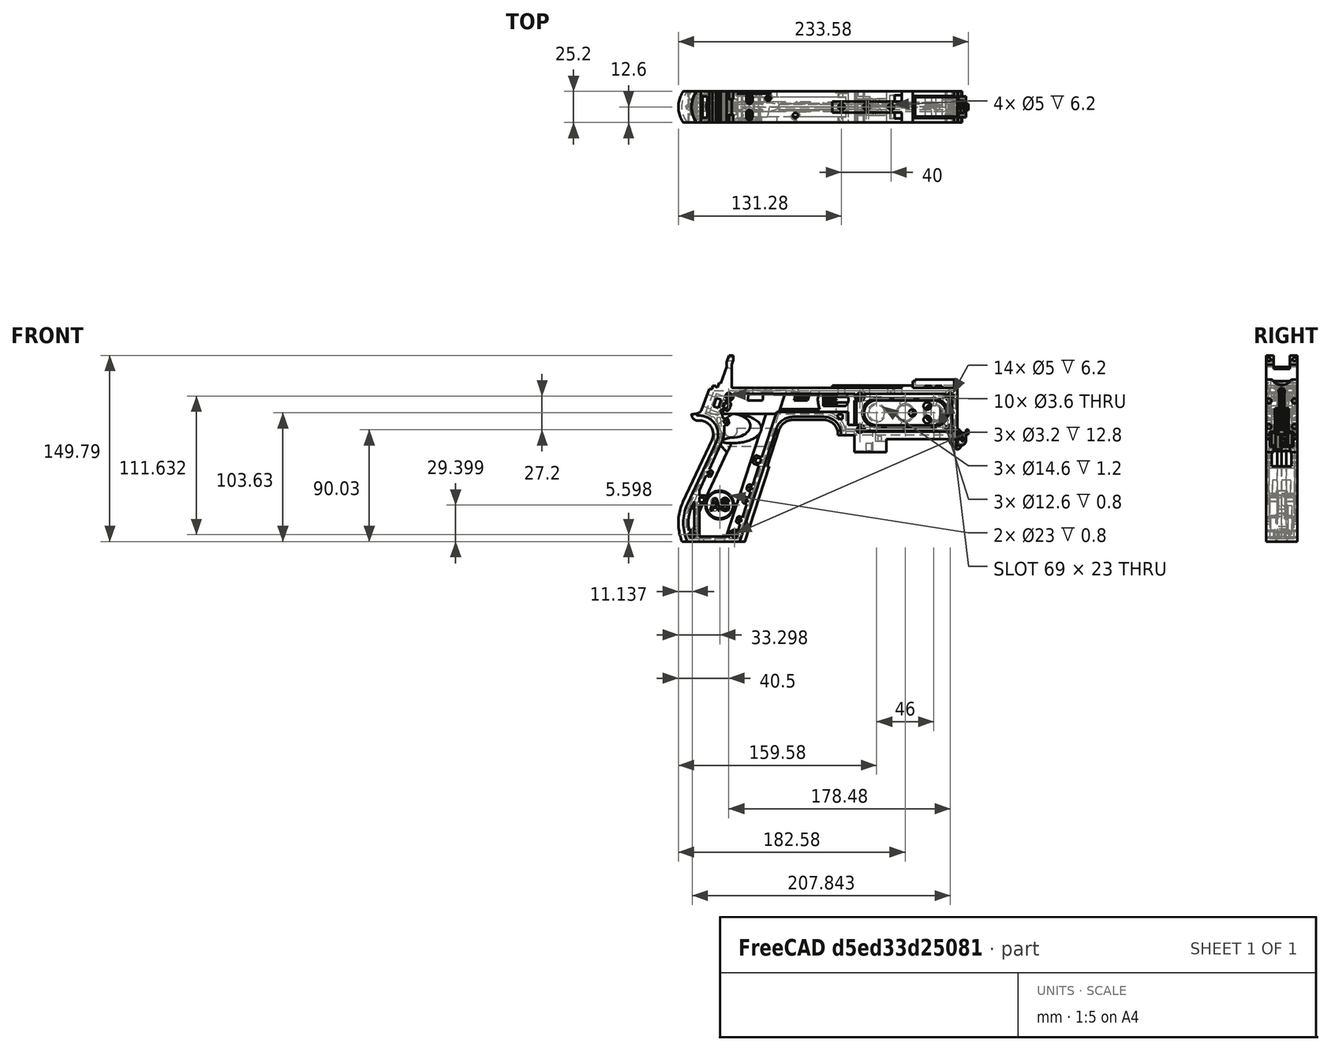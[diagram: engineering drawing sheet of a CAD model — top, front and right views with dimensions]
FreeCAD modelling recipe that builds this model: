
FCSTD DOCUMENT  (FreeCAD 1.0R39319 (Git))
Label: PICON-OF_ver_48
License: All rights reserved
LicenseURL: https://en.wikipedia.org/wiki/All_rights_reserved
objects: Sketcher::SketchObject×119, Part::Extrusion×62, Part::Cut×48, PartDesign::Pad×29, PartDesign::Pocket×18, PartDesign::Chamfer×15, PartDesign::Body×10, PartDesign::Fillet×6, Part::MultiFuse×4, Part::Part2DObjectPython×4, PartDesign::SubtractivePipe×4, PartDesign::SubtractiveLoft×4, PartDesign::Plane×2, PartDesign::SubShapeBinder×2, Part::Sweep×1, PartDesign::ShapeBinder×1, Mesh::Feature×1
note: 600 computed .brp shape members not serialized (recipe doc carries the construction recipe); baked Part::Feature solids carry a one-line shape summary decoded from their .brp

FEATURE [Sketcher::SketchObject] Sketch  label="corpo principale"
  ArcFitTolerance = 1e-06
  AttacherType = Attacher::AttachEngine3D
  AttachmentSupport = -> [XZ_Plane]
  FullyConstrained = true
  MakeInternals = false
  MapMode = 5
  Placement = pos=(0,0,0) rot=(1,0,0;1.5708rad)
  sketch-geometry (65):
    g0: LineSegment StartX=0 StartY=0 StartZ=0 EndX=-57.2 EndY=0 EndZ=0
    g1: LineSegment StartX=-57.2 StartY=0 StartZ=0 EndX=-57.2 EndY=-10.4 EndZ=0
    g2: LineSegment StartX=-57.2 StartY=-10.4 StartZ=0 EndX=-82.8 EndY=-10.4 EndZ=0
    g3: LineSegment StartX=-82.8 StartY=-10.4 StartZ=0 EndX=-82.8 EndY=3.2 EndZ=0
    g4: LineSegment StartX=-82.8 StartY=3.2 StartZ=0 EndX=-93.6 EndY=3.2 EndZ=0
    g5: LineSegment StartX=-93.6 StartY=3.2 StartZ=0 EndX=-93.6 EndY=4 EndZ=0
    g6: LineSegment StartX=-107.6 StartY=18 StartZ=0 EndX=-132.428 EndY=18 EndZ=0
    g7: LineSegment StartX=-145.743 StartY=8.32624 StartZ=0 EndX=-175.232 EndY=-82.4316 EndZ=0
    g8: LineSegment StartX=-175.232 StartY=-82.4316 StartZ=0 EndX=-217.232 EndY=-82.4316 EndZ=0
    g9: LineSegment StartX=-217.232 StartY=-52.1862 StartZ=0 EndX=-193.988 EndY=-2.33927 EndZ=0
    g10: LineSegment StartX=-206.196 StartY=23.0857 StartZ=0 EndX=-199.861 EndY=40.4914 EndZ=0
    g11: LineSegment StartX=-199.861 StartY=40.4914 StartZ=0 EndX=-197.061 EndY=40.4914 EndZ=0
    g12: LineSegment StartX=-197.061 StartY=40.4914 StartZ=0 EndX=-197.061 EndY=42.8914 EndZ=0
    g13: LineSegment StartX=-197.061 StartY=42.8914 StartZ=0 EndX=-194.261 EndY=42.8914 EndZ=0
    g14: LineSegment StartX=-194.261 StartY=42.8914 StartZ=0 EndX=-194.535 EndY=42.1397 EndZ=0
    g15: LineSegment StartX=-194.535 StartY=42.1397 StartZ=0 EndX=-193.031 EndY=41.5924 EndZ=0
    g16: LineSegment StartX=-193.031 StartY=41.5924 StartZ=0 EndX=-191.663 EndY=45.3512 EndZ=0
    g17: LineSegment StartX=-191.663 StartY=45.3512 StartZ=0 EndX=-190.536 EndY=44.9408 EndZ=0
    g18: LineSegment StartX=-190.536 StartY=44.9408 StartZ=0 EndX=-185.747 EndY=58.0965 EndZ=0
    g19: LineSegment StartX=-185.747 StartY=58.0965 StartZ=0 EndX=-185.747 EndY=62.0965 EndZ=0
    g20: LineSegment StartX=-185.747 StartY=62.0965 StartZ=0 EndX=-183.832 EndY=67.3588 EndZ=0
    g21: LineSegment StartX=-183.832 StartY=67.3588 StartZ=0 EndX=-180.232 EndY=67.3588 EndZ=0
    g22: LineSegment StartX=-180.232 StartY=67.3588 StartZ=0 EndX=-180.232 EndY=63.7588 EndZ=0
    g23: LineSegment StartX=-180.232 StartY=63.7588 StartZ=0 EndX=-181.6 EndY=60 EndZ=0
    g24: LineSegment StartX=-181.6 StartY=60 StartZ=0 EndX=-181.6 EndY=41.2 EndZ=0
    g25: LineSegment StartX=-181.6 StartY=41.2 StartZ=0 EndX=-100.8 EndY=41.2 EndZ=0
    g26: LineSegment StartX=-36 StartY=43.2 StartZ=0 EndX=-36 EndY=41.2 EndZ=0
    g27: LineSegment StartX=0 StartY=48 StartZ=0 EndX=0 EndY=0 EndZ=0
    g28: LineSegment StartX=-209.901 StartY=19.85 StartZ=0 EndX=-209.901 EndY=20.1 EndZ=0
    g29: LineSegment StartX=-208.001 StartY=22 StartZ=0 EndX=-207.747 EndY=22 EndZ=0
    g30: LineSegment StartX=-207.583 StartY=19 StartZ=0 EndX=-209.051 EndY=19 EndZ=0
    g31: ArcOfCircle CenterX=-208.001 CenterY=20.1 CenterZ=0 NormalX=0 NormalY=0 NormalZ=1 AngleXU=0 Radius=1.9 StartAngle=1.5708 EndAngle=3.14159
    g32: GeomPoint [constr] X=-209.901 Y=22 Z=0
    g33: ArcOfCircle CenterX=-209.051 CenterY=19.85 CenterZ=0 NormalX=0 NormalY=0 NormalZ=1 AngleXU=0 Radius=0.85 StartAngle=3.14159 EndAngle=4.71239
    g34: GeomPoint [constr] X=-209.901 Y=19 Z=0
    g35: ArcOfCircle CenterX=-207.747 CenterY=23.65 CenterZ=0 NormalX=0 NormalY=0 NormalZ=1 AngleXU=0 Radius=1.65 StartAngle=4.71239 EndAngle=5.93412
    g36: GeomPoint [constr] X=-206.591 Y=22 Z=0
    g37: LineSegment StartX=-4 StartY=6 StartZ=0 EndX=-4 EndY=36.4 EndZ=0
    g38: LineSegment StartX=-4 StartY=36.4 StartZ=0 EndX=-185.2 EndY=36.4 EndZ=0
    g39: LineSegment StartX=-185.2 StartY=36.4 StartZ=0 EndX=-190.441 EndY=22 EndZ=0
    g40: LineSegment StartX=-214.575 StartY=-78.4316 StartZ=0 EndX=-178.142 EndY=-78.4316 EndZ=0
    g41: LineSegment StartX=-178.142 StartY=-78.4316 StartZ=0 EndX=-145.51 EndY=22 EndZ=0
    g42: LineSegment StartX=-145.51 StartY=22 StartZ=0 EndX=-87.91 EndY=22 EndZ=0
    g43: LineSegment StartX=-87.91 StartY=22 StartZ=0 EndX=-87.91 EndY=11.6 EndZ=0
    g44: LineSegment StartX=-87.91 StartY=11.6 StartZ=0 EndX=-80.11 EndY=11.6 EndZ=0
    g45: LineSegment StartX=-80.11 StartY=11.6 StartZ=0 EndX=-80.11 EndY=6 EndZ=0
    g46: LineSegment StartX=-80.11 StartY=6 StartZ=0 EndX=-4 EndY=6 EndZ=0
    g47: LineSegment StartX=-190.363 StartY=-4.02975 StartZ=0 EndX=-213.607 EndY=-53.8767 EndZ=0
    g48: ArcOfCircle CenterX=-132.428 CenterY=4 CenterZ=0 NormalX=0 NormalY=0 NormalZ=1 AngleXU=0 Radius=14 StartAngle=1.5708 EndAngle=2.82743
    g49: GeomPoint [constr] X=-142.6 Y=18 Z=0
    g50: ArcOfCircle CenterX=-107.6 CenterY=4 CenterZ=0 NormalX=0 NormalY=0 NormalZ=1 AngleXU=0 Radius=14 StartAngle=0 EndAngle=1.5708
    g51: GeomPoint [constr] X=-93.6 Y=18 Z=0
    g52: ArcOfCircle CenterX=-184.801 CenterY=-67.3089 CenterZ=0 NormalX=0 NormalY=0 NormalZ=1 AngleXU=0 Radius=35.7833 StartAngle=2.70526 EndAngle=3.57792
    g53: ArcOfCircle CenterX=-207.583 CenterY=4 CenterZ=0 NormalX=0 NormalY=0 NormalZ=1 AngleXU=0 Radius=15 StartAngle=5.84685 EndAngle=7.85398
    g54: LineSegment [constr] StartX=-213.607 StartY=-53.8767 StartZ=0 EndX=-217.232 EndY=-52.1862 EndZ=0
    g55: ArcOfCircle CenterX=-184.801 CenterY=-67.3089 CenterZ=0 NormalX=0 NormalY=0 NormalZ=1 AngleXU=0 Radius=31.7833 StartAngle=2.70526 EndAngle=3.49911
    g56: ArcOfCircle CenterX=-218.095 CenterY=8.90192 CenterZ=0 NormalX=0 NormalY=0 NormalZ=1 AngleXU=0 Radius=30.5989 StartAngle=5.84685 EndAngle=6.72553
    g57: LineSegment StartX=-44.6 StartY=43.2 StartZ=0 EndX=-36 EndY=43.2 EndZ=0
    g58: LineSegment StartX=-100.8 StartY=41.2 StartZ=0 EndX=-44.6 EndY=41.2 EndZ=0
    g59: LineSegment StartX=-44.6 StartY=41.2 StartZ=0 EndX=-44.6 EndY=43.2 EndZ=0
    g60: LineSegment StartX=-2.4 StartY=48 StartZ=0 EndX=0 EndY=48 EndZ=0
    g61: LineSegment StartX=-36 StartY=41.2 StartZ=0 EndX=-2.4 EndY=41.2 EndZ=0
    g62: LineSegment StartX=-2.4 StartY=41.2 StartZ=0 EndX=-2.4 EndY=48 EndZ=0
    g63: LineSegment [constr] StartX=-181.6 StartY=36.4 StartZ=0 EndX=-152.209 EndY=36.4 EndZ=0
    g64: LineSegment [constr] StartX=-181.6 StartY=36.4 StartZ=0 EndX=-130.41 EndY=36.4 EndZ=0
  constraints (183):
    c: Coincident(g-1,g0)
    c: PointOnObject(g0,g-1)
    c: Coincident(g0,g1)
    c: Vertical(g1)
    c: Coincident(g1,g2)
    c: Horizontal(g2)
    c: Coincident(g2,g3)
    c: Vertical(g3)
    c: Coincident(g3,g4)
    c: Coincident(g4,g5)
    c: Vertical(g5)
    c: Horizontal(g6)
    c: Coincident(g7,g8)
    c: Horizontal(g8)
    c: Coincident(g10,g11)
    c: Horizontal(g11)
    c: Coincident(g11,g12)
    c: Vertical(g12)
    c: Coincident(g12,g13)
    c: Horizontal(g13)
    c: Coincident(g13,g14)
    c: Coincident(g14,g15)
    c: Coincident(g15,g16)
    c: Coincident(g16,g17)
    c: Coincident(g17,g18)
    c: Coincident(g18,g19)
    c: Vertical(g19)
    c: Coincident(g19,g20)
    c: Coincident(g20,g21)
    c: Horizontal(g21)
    c: Coincident(g21,g22)
    c: Vertical(g22)
    c: Coincident(g22,g23)
    c: Coincident(g23,g24)
    c: Vertical(g24)
    c: Coincident(g24,g25)
    c: Horizontal(g25)
    c: Coincident(g57,g26)
    c: Vertical(g26)
    c: Coincident(g26,g61)
    c: PointOnObject(g60,g-2)
    c: Coincident(g60,g27)
    c: Coincident(g27,g0)
    c: DistanceY(g27,g27) = 48
    c: DistanceY(g1,g1) = 10.4
    c: DistanceX(g0,g0) = 57.2
    c: DistanceX(g2,g2) = 25.6
    c: Horizontal(g4)
    c: DistanceY(g3,g3) = 13.6
    c: DistanceX(g4,g4) = 10.8
    c: DistanceY(g5,g51) = 14.8
    c: DistanceX(g49,g51) = 49
    c: Distance(g7,g49) = 105.6
    c: DistanceX(g61,g60) = 36
    c: DistanceX(g25,g25) = 80.8
    c: DistanceY(g24,g24) = 18.8
    c: DistanceY(g22,g22) = 3.6
    c: Distance(g23) = 4
    c: Angle(g-1,g23) = 1.22173
    c: DistanceX(g21,g21) = 3.6
    c: Distance(g20) = 5.6
    c: Angle(g-1,g20) = 1.22173
    c: DistanceY(g19,g19) = 4
    c: Distance(g18) = 14
    c: Angle(g-1,g18) = 1.22173
    c: Distance(g17) = 1.2
    c: Distance(g16) = 4
    c: Angle(g16) = 1.22173
    c: Perpendicular(g18,g17)
    c: Distance(g15) = 1.6
    c: Perpendicular(g16,g15)
    c: Distance(g14) = 0.8
    c: DistanceX(g13,g13) = 2.8
    c: Perpendicular(g15,g14)
    c: DistanceY(g12,g12) = 2.4
    c: DistanceX(g11,g11) = 2.8
    c: Distance(g9) = 55
    c: Angle(g9,g-1) = 2.00713
    c: Horizontal(g29)
    c: Vertical(g28)
    c: Horizontal(g30)
    c: PointOnObject(g32,g29)
    c: PointOnObject(g32,g28)
    c: Tangent(g29,g31) = 1.5708
    c: Tangent(g28,g31) = 1.5708
    c: PointOnObject(g34,g28)
    c: PointOnObject(g34,g30)
    c: Tangent(g28,g33) = 1.5708
    c: Tangent(g30,g33) = 1.5708
    c: PointOnObject(g36,g29)
    c: PointOnObject(g36,g10)
    c: Tangent(g29,g35) = -1.5708
    c: Tangent(g10,g35) = -1.5708
    c: Angle(g-1,g10) = 1.22173
    c: Radius(g35) = 1.65
    c: Vertical(g37)
    c: Coincident(g37,g38)
    c: Horizontal(g38)
    c: Coincident(g38,g39)
    c: Horizontal(g40)
    c: Coincident(g40,g41)
    c: Coincident(g41,g42)
    c: Horizontal(g42)
    c: Coincident(g42,g43)
    c: Vertical(g43)
    c: Coincident(g43,g44)
    c: Horizontal(g44)
    c: Coincident(g44,g45)
    c: Vertical(g45)
    c: Coincident(g45,g46)
    c: Coincident(g46,g37)
    c: Horizontal(g46)
    c: DistanceY(g0,g37) = 6
    c: DistanceX(g37,g0) = 4
    c: DistanceY(g37,g25) = 4.8
    c: DistanceX(g38,g38) = 181.2
    c: DistanceX(g42,g42) = 57.6
    c: DistanceY(g49,g41) = 4
    c: DistanceX(g41,g49) = 2.91
    c: DistanceY(g43,g43) = 10.4
    c: DistanceX(g44,g44) = 7.8
    c: DistanceY(g7,g40) = 4
    c: Distance(g47) = 55
    c: Angle(g-1,g39) = 1.22173
    c: PointOnObject(g49,g7)
    c: PointOnObject(g49,g6)
    c: Tangent(g7,g48) = -1.5708
    c: Tangent(g6,g48) = -1.5708
    c: PointOnObject(g51,g5)
    c: PointOnObject(g51,g6)
    c: Tangent(g5,g50) = -1.5708
    c: Tangent(g6,g50) = -1.5708
    c: Radius(g50) = 14
    c: Radius(g48) = 14
    c: DistanceX(g8,g8) = 42
    c: Angle(g7,g-1) = 1.88496
    c: Parallel(g41,g7)
    c: Parallel(g47,g9)
    c: Coincident(g52,g8)
    c: Tangent(g52,g9) = 1.5708
    c: DistanceX(g9,g8) = 0
    c: Tangent(g53,g9) = -1.5708
    c: Tangent(g53,g30) = -1.5708
    c: Diameter(g53) = 30
    c: DistanceY(g53,g0) = -4
    c: Coincident(g54,g47)
    c: Distance(g54) = 4
    c: Coincident(g54,g9)
    c: Coincident(g55,g40)
    c: Tangent(g55,g47) = -1.5708
    c: Coincident(g52,g55)
    c: Coincident(g56,g39)
    c: Tangent(g56,g47) = 1.5708
    c: Horizontal(g57)
    c: DistanceX(g57,g57) = 8.6
    c: Coincident(g58,g25)
    c: Horizontal(g58)
    c: Coincident(g59,g58)
    c: Vertical(g59)
    c: DistanceY(g58,g57) = 2
    c: DistanceX(g58,g58) = 56.2
    c: Coincident(g59,g57)
    c: DistanceY(g41,g36) = 0
    c: DistanceY(g36,g39) = 0
    c: DistanceY(g28,g28) = 0.25
    c: DistanceX(g30,g36) = 2.46
    c: DistanceX(g28,g29) = 1.9
    c: Coincident(g62,g60)
    c: Horizontal(g60)
    c: DistanceX(g62,g27) = 2.4
    c: Coincident(g61,g62)
    c: DistanceY(g26,g26) = 2
    c: Vertical(g62)
    c: DistanceY(g61,g60) = 6.8
    c: Horizontal(g61)
    c: Distance(g63) = 29.391
    c: PointOnObject(g63,g38)
    c: PointOnObject(g63,g38)
    c: Distance(g64) = 51.19
    c: PointOnObject(g64,g38)
    c: PointOnObject(g64,g38)
    c: DistanceX(g24,g63) = 0
    c: DistanceX(g24,g64) = 0
FEATURE [Part::Extrusion] Extrude  label="Extrude corpo principale"
  Base = -> Sketch
  Dir = (0,-1,2e-16)
  DirMode = 2
  FaceMakerClass = Part::FaceMakerBullseye
  FaceMakerMode = 3
  LengthFwd = 25.2
  LengthRev = 12.6
  Solid = true
  Symmetric = true
FEATURE [Sketcher::SketchObject] Sketch002  label="scavo grilletto"
  ArcFitTolerance = 1e-06
  AttachmentSupport = -> [XZ_Plane]
  ExternalGeometry = -> [Sketch]
  FullyConstrained = true
  MakeInternals = false
  MapMode = 5
  Placement = pos=(0,0,0) rot=(1,0,0;1.5708rad)
  sketch-geometry (4):
    g0: LineSegment StartX=-89.51 StartY=22 StartZ=0 EndX=-152.71 EndY=22 EndZ=0
    g1: LineSegment StartX=-152.71 StartY=22 StartZ=0 EndX=-167.006 EndY=-22 EndZ=0
    g2: LineSegment StartX=-167.006 StartY=-22 StartZ=0 EndX=-89.51 EndY=-22 EndZ=0
    g3: LineSegment StartX=-89.51 StartY=-22 StartZ=0 EndX=-89.51 EndY=22 EndZ=0
  constraints (12):
    c: Horizontal(g0)
    c: Coincident(g0,g1)
    c: Coincident(g1,g2)
    c: Horizontal(g2)
    c: Coincident(g2,g3)
    c: Coincident(g3,g0)
    c: Vertical(g3)
    c: Angle(g1,g0) = 1.88496
    c: DistanceY(g3,g3) = 44
    c: DistanceX(g0,g0) = 63.2
    c: DistanceX(g0,g-3) = 1.6
    c: DistanceY(g-3,g0) = 0
FEATURE [Sketcher::SketchObject] Sketch004  label="traiettoria arrotondamento impugnatura anteriore"
  ArcFitTolerance = 1e-06
  AttachmentSupport = -> [XZ_Plane]
  ExternalGeometry = -> [Sketch]
  FullyConstrained = true
  MakeInternals = false
  MapMode = 5
  Placement = pos=(0,0,0) rot=(1,0,0;1.5708rad)
  sketch-geometry (13):
    g0: LineSegment StartX=-175.232 StartY=-82.4316 StartZ=0 EndX=-145.743 EndY=8.32624 EndZ=0
    g1: LineSegment StartX=-93.6 StartY=3.2 StartZ=0 EndX=-93.6 EndY=4 EndZ=0
    g2: LineSegment StartX=-132.428 StartY=18 StartZ=0 EndX=-107.6 EndY=18 EndZ=0
    g3: ArcOfCircle CenterX=-132.428 CenterY=4 CenterZ=0 NormalX=0 NormalY=0 NormalZ=1 AngleXU=0 Radius=14 StartAngle=1.5708 EndAngle=2.82743
    g4: ArcOfCircle CenterX=-107.6 CenterY=4 CenterZ=0 NormalX=0 NormalY=0 NormalZ=1 AngleXU=0 Radius=14 StartAngle=0 EndAngle=1.5708
    g5: LineSegment StartX=-175.232 StartY=-82.4316 StartZ=0 EndX=-217.232 EndY=-82.4316 EndZ=0
    g6: LineSegment StartX=-217.232 StartY=-52.1862 StartZ=0 EndX=-193.988 EndY=-2.33927 EndZ=0
    g7: LineSegment StartX=-209.051 StartY=19 StartZ=0 EndX=-207.583 EndY=19 EndZ=0
    g8: LineSegment StartX=-209.901 StartY=20.1 StartZ=0 EndX=-209.901 EndY=19.85 EndZ=0
    g9: ArcOfCircle CenterX=-184.801 CenterY=-67.3089 CenterZ=0 NormalX=0 NormalY=0 NormalZ=1 AngleXU=0 Radius=35.7833 StartAngle=2.70526 EndAngle=3.57792
    g10: ArcOfCircle CenterX=-207.583 CenterY=4 CenterZ=0 NormalX=0 NormalY=0 NormalZ=1 AngleXU=0 Radius=15 StartAngle=5.84685 EndAngle=7.85398
    g11: ArcOfCircle CenterX=-209.051 CenterY=19.85 CenterZ=0 NormalX=0 NormalY=0 NormalZ=1 AngleXU=0 Radius=0.85 StartAngle=3.14159 EndAngle=4.71239
    g12: ArcOfCircle CenterX=-208.001 CenterY=20.1 CenterZ=0 NormalX=0 NormalY=0 NormalZ=1 AngleXU=0 Radius=1.9 StartAngle=1.5708 EndAngle=3.14159
  constraints (26):
    c: Coincident(g0,g-3)
    c: Coincident(g0,g-6)
    c: Coincident(g1,g-8)
    c: Coincident(g1,g-7)
    c: Coincident(g2,g-5)
    c: Coincident(g2,g-4)
    c: Coincident(g3,g2)
    c: Tangent(g3,g0) = 1.5708
    c: Coincident(g4,g1)
    c: Tangent(g4,g2) = 1.5708
    c: Coincident(g5,g0)
    c: Coincident(g5,g-9)
    c: Coincident(g6,g-12)
    c: Coincident(g6,g-11)
    c: Coincident(g7,g-15)
    c: Coincident(g7,g-14)
    c: Coincident(g8,g-16)
    c: Coincident(g8,g-17)
    c: Tangent(g9,g6) = 1.5708
    c: Coincident(g9,g5)
    c: Coincident(g10,g7)
    c: Tangent(g10,g6) = -1.5708
    c: Tangent(g11,g7) = -1.5708
    c: Coincident(g11,g8)
    c: Tangent(g12,g8) = -1.5708
    c: Coincident(g12,g-17)
FEATURE [PartDesign::Plane] DatumPlane  label="Piano per disegno arrotondamento impugnatura"
  AttachmentSupport = -> [Sketch]
  Length = 73.6581
  MapMode = 7
  Placement = pos=(-145.743,1.8e-15,8.32624) rot=(0.154555,0.154555,0.97582;1.59527rad)
  ResizeMode = 0
  Width = 303.511
FEATURE [Sketcher::SketchObject] Sketch005  label="forma arrotondamento impugnatura anteriore"
  ArcFitTolerance = 1e-06
  AttachmentSupport = -> [DatumPlane]
  FullyConstrained = true
  MakeInternals = false
  MapMode = 5
  Placement = pos=(-145.743,1.8e-15,8.32624) rot=(0.154555,0.154555,0.97582;1.59527rad)
  sketch-geometry (5):
    g0: GeomPoint [constr] X=0 Y=-4 Z=0
    g1: GeomPoint [constr] X=-12.6 Y=7.1e-15 Z=0
    g2: GeomPoint [constr] X=12.6 Y=4.97e-14 Z=0
    g3: LineSegment StartX=-12.6 StartY=7.1e-15 StartZ=0 EndX=12.6 EndY=4.97e-14 EndZ=0
    g4: ArcOfCircle CenterX=-3.88e-14 CenterY=17.845 CenterZ=0 NormalX=0 NormalY=0 NormalZ=1 AngleXU=0 Radius=21.845 StartAngle=4.09759 EndAngle=5.32718
  constraints (11):
    c: DistanceY(g0,g-1) = 4
    c: DistanceX(g-1,g0) = 0
    c: DistanceX(g1,g-1) = 12.6
    c: DistanceX(g-1,g2) = 12.6
    c: DistanceY(g-1,g2) = 0
    c: DistanceY(g-1,g1) = 0
    c: Coincident(g3,g1)
    c: Coincident(g3,g2)
    c: Coincident(g4,g1)
    c: Coincident(g4,g2)
    c: PointOnObject(g0,g4)
FEATURE [Part::Sweep] Sweep  label="Sweep impugnatura"
  Frenet = true
  Sections = -> [Sketch005]
  Solid = true
  Spine = -> Sketch [Edge32,Edge33,Edge34,Edge35,Edge36,Edge37,Edge38,Edge39,Edge40,Edge41,Edge42,Edge43,Edge44]
  Transition = 1
FEATURE [Sketcher::SketchObject] Sketch008  label="buchi e pulizie varie"
  ArcFitTolerance = 1e-06
  AttachmentSupport = -> [XZ_Plane]
  ExternalGeometry = -> [Sketch]
  FullyConstrained = true
  MakeInternals = false
  MapMode = 5
  Placement = pos=(0,0,0) rot=(1,0,0;1.5708rad)
  sketch-geometry (26):
    g0: LineSegment StartX=-96.278 StartY=20.155 StartZ=0 EndX=-92.278 EndY=20.155 EndZ=0
    g1: LineSegment StartX=-92.278 StartY=20.155 StartZ=0 EndX=-92.278 EndY=16.155 EndZ=0
    g2: LineSegment StartX=-92.278 StartY=16.155 StartZ=0 EndX=-96.278 EndY=16.155 EndZ=0
    g3: LineSegment StartX=-96.278 StartY=16.155 StartZ=0 EndX=-96.278 EndY=20.155 EndZ=0
    g4: LineSegment StartX=-222.232 StartY=-82.4316 StartZ=0 EndX=-170.232 EndY=-82.4316 EndZ=0
    g5: LineSegment StartX=-170.232 StartY=-82.4316 StartZ=0 EndX=-170.232 EndY=-86.4316 EndZ=0
    g6: LineSegment StartX=-170.232 StartY=-86.4316 StartZ=0 EndX=-222.232 EndY=-86.4316 EndZ=0
    g7: LineSegment StartX=-222.232 StartY=-86.4316 StartZ=0 EndX=-222.232 EndY=-82.4316 EndZ=0
    g8: LineSegment StartX=-213.901 StartY=20.1 StartZ=0 EndX=-213.901 EndY=26 EndZ=0
    g9: LineSegment StartX=-213.901 StartY=26 StartZ=0 EndX=-206.196 EndY=26 EndZ=0
    g10: LineSegment StartX=-17.4 StartY=42.8 StartZ=0 EndX=-12.4 EndY=42.8 EndZ=0
    g11: LineSegment StartX=-12.4 StartY=42.8 StartZ=0 EndX=-12.4 EndY=41.2 EndZ=0
    g12: LineSegment StartX=-12.4 StartY=41.2 StartZ=0 EndX=-17.4 EndY=41.2 EndZ=0
    g13: LineSegment StartX=-17.4 StartY=41.2 StartZ=0 EndX=-17.4 EndY=42.8 EndZ=0
    g14: LineSegment StartX=-25.9 StartY=42.8 StartZ=0 EndX=-20.9 EndY=42.8 EndZ=0
    g15: LineSegment StartX=-20.9 StartY=42.8 StartZ=0 EndX=-20.9 EndY=41.2 EndZ=0
    g16: LineSegment StartX=-20.9 StartY=41.2 StartZ=0 EndX=-25.9 EndY=41.2 EndZ=0
    g17: LineSegment StartX=-25.9 StartY=41.2 StartZ=0 EndX=-25.9 EndY=42.8 EndZ=0
    g18: GeomPoint [constr] X=-206.196 Y=23.0857 Z=0
    g19: GeomPoint [constr] X=-213.901 Y=20.1 Z=0
    g20: BSplineCurve PolesCount=4 KnotsCount=2 Degree=3 IsPeriodic=0
    g21-g24: Circle [constr] x4 (B-spline internal-alignment scaffolding for g20; pole/knot coordinates omitted)
    g25: LineSegment StartX=-206.196 StartY=26 StartZ=0 EndX=-206.196 EndY=23.0857 EndZ=0
  constraints (73):
    c: Horizontal(g0)
    c: Coincident(g1,g0)
    c: Vertical(g1)
    c: Coincident(g2,g1)
    c: Horizontal(g2)
    c: Coincident(g3,g2)
    c: Coincident(g3,g0)
    c: Vertical(g3)
    c: DistanceX(g0,g-4) = 4.368
    c: DistanceY(g0,g-4) = 1.845
    c: DistanceY(g1,g1) = 4
    c: DistanceX(g2,g2) = 4
    c: Horizontal(g4)
    c: Coincident(g5,g4)
    c: Vertical(g5)
    c: Coincident(g6,g5)
    c: Horizontal(g6)
    c: Coincident(g7,g6)
    c: Coincident(g7,g4)
    c: Vertical(g7)
    c: DistanceY(g7,g7) = 4
    c: DistanceX(g4,g-5) = 5
    c: DistanceX(g-5,g4) = 5
    c: DistanceY(g4,g-5) = 0
    c: Coincident(g9,g8)
    c: Parallel(g9,g-6)
    c: DistanceX(g8,g-8) = 4
    c: Horizontal(g10)
    c: Coincident(g11,g10)
    c: Vertical(g11)
    c: Coincident(g12,g11)
    c: Horizontal(g12)
    c: Coincident(g13,g12)
    c: Coincident(g13,g10)
    c: Vertical(g13)
    c: Horizontal(g14)
    c: Coincident(g15,g14)
    c: Vertical(g15)
    c: Coincident(g16,g15)
    c: Horizontal(g16)
    c: Coincident(g17,g16)
    c: Coincident(g17,g14)
    c: Vertical(g17)
    c: DistanceY(g11,g10) = 1.6
    c: DistanceX(g10,g10) = 5
    c: DistanceY(g15,g14) = 1.6
    c: DistanceX(g14,g14) = 5
    c: DistanceX(g15,g12) = 3.5
    c: DistanceX(g11,g-9) = 10
    c: DistanceY(g-9,g11) = 0
    c: DistanceY(g-9,g15) = 0
    c: Perpendicular(g8,g9)
    c: DistanceY(g-7,g9) = 4
    c: DistanceY(g8,g-8) = 0
    c: InternalAlignment(g18,g20)
    c: InternalAlignment(g19,g20)
    c: InternalAlignment(g21,g20)
    c: Weight(g21) = 1
    c: InternalAlignment(g22,g20)
    c: Equal(g22,g21)
    c: InternalAlignment(g23,g20)
    c: Equal(g23,g21)
    c: InternalAlignment(g24,g20)
    c: Equal(g24,g21)
    c: Coincident(g18,g-12)
    c: Coincident(g19,g8)
    c: Coincident(g25,g9)
    c: Coincident(g25,g20)
    c: Vertical(g25)
    c: DistanceY(g20,g23) = 0
    c: DistanceY(g22,g18) = 2.26
    c: DistanceX(g22,g18) = 0.93
    c: DistanceX(g20,g23) = 2.9
FEATURE [Part::Extrusion] Extrude004  label="Extrude Buchi e pulizie varie"
  Base = -> Sketch008
  Dir = (0,-1,2e-16)
  DirMode = 2
  FaceMakerClass = Part::FaceMakerBullseye
  FaceMakerMode = 3
  LengthFwd = 25.2
  LengthRev = 0
  Solid = true
  Symmetric = true
FEATURE [Sketcher::SketchObject] Sketch009  label="rinforzi"
  ArcFitTolerance = 1e-06
  AttachmentSupport = -> [XZ_Plane]
  ExternalGeometry = -> [Sketch]
  FullyConstrained = true
  MakeInternals = false
  MapMode = 5
  Placement = pos=(0,0,0) rot=(1,0,0;1.5708rad)
  sketch-geometry (9):
    g0: LineSegment StartX=-87.91 StartY=22 StartZ=0 EndX=-87.91 EndY=36.4 EndZ=0
    g1: LineSegment StartX=-87.91 StartY=36.4 StartZ=0 EndX=-97.91 EndY=36.4 EndZ=0
    g2: LineSegment StartX=-97.91 StartY=36.4 StartZ=0 EndX=-97.91 EndY=22 EndZ=0
    g3: LineSegment StartX=-97.91 StartY=22 StartZ=0 EndX=-87.91 EndY=22 EndZ=0
    g4: LineSegment StartX=-149.713 StartY=9.06563 StartZ=0 EndX=-154.586 EndY=-5.93437 EndZ=0
    g5: LineSegment StartX=-154.586 StartY=-5.93437 StartZ=0 EndX=-191.863 EndY=-5.93437 EndZ=0
    g6: LineSegment StartX=-191.863 StartY=-5.93437 StartZ=0 EndX=-191.863 EndY=9.06563 EndZ=0
    g7: LineSegment StartX=-191.863 StartY=9.06563 StartZ=0 EndX=-149.713 EndY=9.06563 EndZ=0
    g8: LineSegment [constr] StartX=-145.51 StartY=22 StartZ=0 EndX=-149.713 EndY=9.06563 EndZ=0
  constraints (25):
    c: Vertical(g0)
    c: Coincident(g1,g0)
    c: Horizontal(g1)
    c: Coincident(g2,g1)
    c: Vertical(g2)
    c: Coincident(g3,g2)
    c: Coincident(g3,g0)
    c: Horizontal(g3)
    c: Coincident(g0,g-4)
    c: DistanceX(g3,g3) = 10
    c: DistanceY(g0,g-3) = 0
    c: Coincident(g5,g4)
    c: Horizontal(g5)
    c: Coincident(g6,g5)
    c: Vertical(g6)
    c: Coincident(g7,g6)
    c: Coincident(g7,g4)
    c: Horizontal(g7)
    c: Distance(g8) = 13.6
    c: Parallel(g-6,g8)
    c: Coincident(g-6,g8)
    c: Parallel(g4,g-6)
    c: DistanceY(g4,g4) = 15
    c: Coincident(g4,g8)
    c: DistanceX(g-5,g5) = -1.5
FEATURE [Part::Extrusion] Extrude001  label="Extrude scavo grilletto"
  Base = -> Sketch002
  Dir = (0,-1,2e-16)
  DirMode = 2
  FaceMakerClass = Part::FaceMakerBullseye
  FaceMakerMode = 3
  LengthFwd = 16
  LengthRev = 0
  Solid = true
  Symmetric = true
FEATURE [Part::Extrusion] Extrude005  label="Extrude Rinforzi"
  Base = -> Sketch009
  Dir = (0,-1,2e-16)
  DirMode = 2
  FaceMakerClass = Part::FaceMakerBullseye
  FaceMakerMode = 3
  LengthFwd = 2
  LengthRev = 0
  Placement = pos=(0,12.6,0) rot=(0,0,1;0rad)
  Solid = true
  Symmetric = false
FEATURE [PartDesign::ShapeBinder] CopyCut
  TraceSupport = false
FEATURE [PartDesign::Plane] DatumPlane001
  AttachmentSupport = -> [CopyCut]
  Length = 283.944
  MapMode = 5
  Placement = pos=(0,12.6,0) rot=(0,0.707107,0.707107;3.14159rad)
  ResizeMode = 0
  Width = 188.15
FEATURE [Sketcher::SketchObject] Sketch010  label="buco neopixel"
  ArcFitTolerance = 1e-06
  AttachmentSupport = -> [XZ_Plane]
  ExternalGeometry = -> [Sketch]
  FullyConstrained = true
  MakeInternals = false
  MapMode = 5
  Placement = pos=(0,0,0) rot=(1,0,0;1.5708rad)
  sketch-geometry (5):
    g0: LineSegment [constr] StartX=-199.861 StartY=40.4914 StartZ=0 EndX=-201.368 EndY=36.3521 EndZ=0
    g1: LineSegment StartX=-201.368 StartY=36.3521 StartZ=0 EndX=-204.932 EndY=26.5605 EndZ=0
    g2: LineSegment StartX=-201.368 StartY=36.3521 StartZ=0 EndX=-180.2 EndY=28.6477 EndZ=0
    g3: LineSegment StartX=-180.2 StartY=28.6477 StartZ=0 EndX=-183.764 EndY=18.8561 EndZ=0
    g4: LineSegment StartX=-183.764 StartY=18.8561 StartZ=0 EndX=-204.932 EndY=26.5605 EndZ=0
  constraints (14):
    c: Parallel(g0,g-3)
    c: Distance(g0) = 4.405
    c: Coincident(g0,g-3)
    c: Coincident(g2,g1)
    c: Coincident(g3,g2)
    c: Coincident(g4,g3)
    c: Coincident(g4,g1)
    c: Parallel(g1,g-3)
    c: Distance(g1) = 10.42
    c: Coincident(g1,g0)
    c: Parallel(g2,g4)
    c: Perpendicular(g1,g2)
    c: DistanceX(g-4,g2) = 5
    c: Parallel(g3,g1)
FEATURE [Part::Extrusion] Extrude006  label="Extrude buco neopixel"
  Base = -> Sketch010
  Dir = (0,-1,2e-16)
  DirMode = 2
  FaceMakerClass = Part::FaceMakerBullseye
  FaceMakerMode = 3
  LengthFwd = 17.2
  LengthRev = 0
  Solid = true
  Symmetric = true
FEATURE [Sketcher::SketchObject] Sketch011  label="fermo grilletto"
  ArcFitTolerance = 1e-06
  AttachmentSupport = -> [XZ_Plane]
  ExternalGeometry = -> [Sketch]
  FullyConstrained = true
  MakeInternals = false
  MapMode = 5
  Placement = pos=(0,0,0) rot=(1,0,0;1.5708rad)
  sketch-geometry (18):
    g0: LineSegment [constr] StartX=-145.51 StartY=22 StartZ=0 EndX=-157.347 EndY=-14.4293 EndZ=0
    g1: LineSegment [constr] StartX=-157.347 StartY=-14.4293 StartZ=0 EndX=-157.841 EndY=-15.951 EndZ=0
    g2: LineSegment StartX=-161.151 StartY=-13.1932 StartZ=0 EndX=-155.825 EndY=-14.9237 EndZ=0
    g3: LineSegment StartX=-163.167 StartY=-14.2205 StartZ=0 EndX=-164.403 EndY=-18.0247 EndZ=0
    g4: LineSegment StartX=-163.376 StartY=-20.0408 StartZ=0 EndX=-158.05 EndY=-21.7713 EndZ=0
    g5: LineSegment StartX=-158.05 StartY=-21.7713 StartZ=0 EndX=-155.825 EndY=-14.9237 EndZ=0
    g6: LineSegment StartX=-161.645 StartY=-14.7149 StartZ=0 EndX=-157.841 EndY=-15.951 EndZ=0
    g7: LineSegment StartX=-157.841 StartY=-15.951 StartZ=0 EndX=-159.077 EndY=-19.7552 EndZ=0
    g8: LineSegment StartX=-159.077 StartY=-19.7552 StartZ=0 EndX=-162.881 EndY=-18.5191 EndZ=0
    g9: LineSegment StartX=-162.881 StartY=-18.5191 StartZ=0 EndX=-161.645 EndY=-14.7149 EndZ=0
    g10: LineSegment [constr] StartX=-161.645 StartY=-14.7149 StartZ=0 EndX=-161.151 EndY=-13.1932 EndZ=0
    g11: LineSegment [constr] StartX=-159.077 StartY=-19.7552 StartZ=0 EndX=-157.555 EndY=-20.2496 EndZ=0
    g12: LineSegment [constr] StartX=-159.077 StartY=-19.7552 StartZ=0 EndX=-159.572 EndY=-21.2769 EndZ=0
    g13: LineSegment [constr] StartX=-161.645 StartY=-14.7149 StartZ=0 EndX=-163.167 EndY=-14.2205 EndZ=0
    g14: ArcOfCircle CenterX=-161.645 CenterY=-14.7149 CenterZ=0 NormalX=0 NormalY=0 NormalZ=1 AngleXU=0 Radius=1.6 StartAngle=1.25664 EndAngle=2.82743
    g15: GeomPoint [constr] X=-162.673 Y=-12.6988 Z=0
    g16: ArcOfCircle CenterX=-162.881 CenterY=-18.5191 CenterZ=0 NormalX=0 NormalY=0 NormalZ=1 AngleXU=0 Radius=1.6 StartAngle=2.82743 EndAngle=4.39823
    g17: GeomPoint [constr] X=-164.897 Y=-19.5464 Z=0
  constraints (48):
    c: Parallel(g0,g-3)
    c: Distance(g0) = 38.304
    c: Coincident(g0,g-3)
    c: Parallel(g1,g-3)
    c: Distance(g1) = 1.6
    c: Coincident(g1,g0)
    c: Coincident(g5,g4)
    c: Coincident(g5,g2)
    c: Coincident(g7,g6)
    c: Coincident(g8,g7)
    c: Coincident(g9,g8)
    c: Coincident(g9,g6)
    c: Parallel(g7,g-3)
    c: Parallel(g9,g7)
    c: Perpendicular(g6,g7)
    c: Parallel(g6,g8)
    c: Distance(g6) = 4
    c: Distance(g9) = 4
    c: Parallel(g5,g7)
    c: Parallel(g9,g3)
    c: Parallel(g2,g6)
    c: Parallel(g4,g8)
    c: Parallel(g13,g6)
    c: Parallel(g10,g9)
    c: Parallel(g11,g8)
    c: Parallel(g12,g7)
    c: Distance(g10) = 1.6
    c: Distance(g13) = 1.6
    c: Distance(g12) = 1.6
    c: Distance(g11) = 1.6
    c: Coincident(g10,g6)
    c: Coincident(g13,g6)
    c: Coincident(g12,g7)
    c: Coincident(g11,g7)
    c: Distance(g10,g15) = 1.6
    c: Distance(g15,g13) = 1.6
    c: Distance(g4,g12) = 1.6
    c: Distance(g4,g11) = 1.6
    c: PointOnObject(g15,g2)
    c: Tangent(g3,g14) = -1.5708
    c: Tangent(g2,g14) = 1.5708
    c: PointOnObject(g17,g4)
    c: PointOnObject(g17,g3)
    c: Tangent(g4,g16) = -1.5708
    c: Tangent(g3,g16) = -1.5708
    c: Equal(g16,g14)
    c: Coincident(g16,g8)
    c: Coincident(g6,g1)
FEATURE [Part::Extrusion] Extrude007  label="Extrude fermo grilletto"
  Base = -> Sketch011
  Dir = (0,-1,2e-16)
  DirMode = 2
  FaceMakerClass = Part::FaceMakerBullseye
  FaceMakerMode = 3
  LengthFwd = 25.2
  LengthRev = 0
  Solid = true
  Symmetric = true
FEATURE [Sketcher::SketchObject] Sketch012  label="buco oled"
  ArcFitTolerance = 1e-06
  AttachmentSupport = -> [XZ_Plane]
  ExternalGeometry = -> [Sketch]
  FullyConstrained = true
  MakeInternals = false
  MapMode = 5
  Placement = pos=(0,0,0) rot=(1,0,0;1.5708rad)
  sketch-geometry (4):
    g0: LineSegment StartX=-185.747 StartY=58.0965 StartZ=0 EndX=-180.232 EndY=56.0891 EndZ=0
    g1: LineSegment StartX=-185.747 StartY=58.0965 StartZ=0 EndX=-185.747 EndY=67.3588 EndZ=0
    g2: LineSegment StartX=-185.747 StartY=67.3588 StartZ=0 EndX=-180.232 EndY=67.3588 EndZ=0
    g3: LineSegment StartX=-180.232 StartY=67.3588 StartZ=0 EndX=-180.232 EndY=56.0891 EndZ=0
  constraints (10):
    c: Coincident(g1,g0)
    c: Coincident(g2,g1)
    c: Coincident(g3,g2)
    c: Coincident(g3,g0)
    c: Parallel(g1,g-5)
    c: Perpendicular(g-3,g0)
    c: Parallel(g2,g-6)
    c: Parallel(g3,g-4)
    c: Coincident(g0,g-5)
    c: Coincident(g2,g-6)
FEATURE [Part::Extrusion] Extrude008  label="Extrude buco oled"
  Base = -> Sketch012
  Dir = (0,-1,2e-16)
  DirMode = 2
  FaceMakerClass = Part::FaceMakerBullseye
  FaceMakerMode = 3
  LengthFwd = 12.8
  LengthRev = 0
  Solid = true
  Symmetric = true
FEATURE [Sketcher::SketchObject] Sketch013  label="buco pompa"
  ArcFitTolerance = 1e-06
  AttachmentSupport = -> [XZ_Plane]
  ExternalGeometry = -> [Sketch]
  FullyConstrained = true
  MakeInternals = false
  MapMode = 5
  Placement = pos=(0,0,0) rot=(1,0,0;1.5708rad)
  sketch-geometry (8):
    g0: LineSegment StartX=-82.8 StartY=-10.4 StartZ=0 EndX=-82.8 EndY=-9.6 EndZ=0
    g1: LineSegment StartX=-82.8 StartY=-9.6 StartZ=0 EndX=-67.9 EndY=-9.6 EndZ=0
    g2: LineSegment StartX=-67.9 StartY=-9.6 StartZ=0 EndX=-67.9 EndY=6 EndZ=0
    g3: LineSegment StartX=-67.9 StartY=6 StartZ=0 EndX=-65.9 EndY=6 EndZ=0
    g4: LineSegment StartX=-65.9 StartY=6 StartZ=0 EndX=-65.9 EndY=-1.7 EndZ=0
    g5: LineSegment StartX=-65.9 StartY=-1.7 StartZ=0 EndX=-57.2 EndY=-1.7 EndZ=0
    g6: LineSegment StartX=-57.2 StartY=-1.7 StartZ=0 EndX=-57.2 EndY=-10.4 EndZ=0
    g7: LineSegment StartX=-57.2 StartY=-10.4 StartZ=0 EndX=-82.8 EndY=-10.4 EndZ=0
  constraints (22):
    c: Vertical(g0)
    c: Coincident(g1,g0)
    c: Horizontal(g1)
    c: Coincident(g2,g1)
    c: Vertical(g2)
    c: Coincident(g3,g2)
    c: Horizontal(g3)
    c: Coincident(g4,g3)
    c: Vertical(g4)
    c: Coincident(g5,g4)
    c: Horizontal(g5)
    c: Coincident(g6,g5)
    c: Vertical(g6)
    c: Coincident(g7,g6)
    c: Coincident(g7,g0)
    c: DistanceY(g0,g0) = 0.8
    c: DistanceY(g6,g6) = 8.7
    c: DistanceX(g1,g1) = 14.9
    c: DistanceX(g3,g3) = 2
    c: Coincident(g0,g-4)
    c: DistanceY(g2,g-6) = 0
    c: Coincident(g6,g-5)
FEATURE [Part::Extrusion] Extrude009  label="Extrude buco pompa"
  Base = -> Sketch013
  Dir = (0,-1,2e-16)
  DirMode = 2
  FaceMakerClass = Part::FaceMakerBullseye
  FaceMakerMode = 3
  LengthFwd = 13.2
  LengthRev = 0
  Solid = true
  Symmetric = true
FEATURE [Sketcher::SketchObject] Sketch014  label="buco frontale"
  ArcFitTolerance = 1e-06
  AttachmentSupport = -> [XZ_Plane]
  ExternalGeometry = -> [Sketch]
  FullyConstrained = true
  MakeInternals = false
  MapMode = 5
  Placement = pos=(0,0,0) rot=(1,0,0;1.5708rad)
  sketch-geometry (10):
    g0: LineSegment StartX=0 StartY=0 StartZ=0 EndX=0 EndY=24.671 EndZ=0
    g1: LineSegment StartX=0 StartY=24.671 StartZ=0 EndX=-4 EndY=24.671 EndZ=0
    g2: LineSegment StartX=-4 StartY=24.671 StartZ=0 EndX=-4 EndY=16 EndZ=0
    g3: LineSegment StartX=-4 StartY=16 StartZ=0 EndX=-2.4 EndY=16 EndZ=0
    g4: LineSegment StartX=-2.4 StartY=16 StartZ=0 EndX=-2.4 EndY=10 EndZ=0
    g5: LineSegment StartX=-2.4 StartY=10 StartZ=0 EndX=-12 EndY=10 EndZ=0
    g6: LineSegment StartX=-12 StartY=10 StartZ=0 EndX=-12 EndY=6 EndZ=0
    g7: LineSegment StartX=-12 StartY=6 StartZ=0 EndX=-2.4 EndY=6 EndZ=0
    g8: LineSegment StartX=-2.4 StartY=6 StartZ=0 EndX=-2.4 EndY=0 EndZ=0
    g9: LineSegment StartX=-2.4 StartY=0 StartZ=0 EndX=0 EndY=0 EndZ=0
  constraints (29):
    c: Vertical(g0)
    c: Coincident(g1,g0)
    c: Horizontal(g1)
    c: Coincident(g2,g1)
    c: Vertical(g2)
    c: Coincident(g3,g2)
    c: Horizontal(g3)
    c: Coincident(g4,g3)
    c: Vertical(g4)
    c: Coincident(g5,g4)
    c: Horizontal(g5)
    c: Coincident(g6,g5)
    c: Vertical(g6)
    c: Coincident(g7,g6)
    c: Coincident(g8,g7)
    c: Vertical(g8)
    c: Coincident(g9,g8)
    c: Coincident(g9,g0)
    c: Horizontal(g9)
    c: DistanceY(g0,g0) = 24.671
    c: Horizontal(g7)
    c: DistanceY(g6,g6) = 4
    c: DistanceY(g4,g4) = 6
    c: DistanceX(g9,g9) = 2.4
    c: Coincident(g0,g-1)
    c: DistanceY(g-3,g7) = 0
    c: DistanceX(g8,g4) = 0
    c: DistanceX(g-3,g1) = 0
    c: DistanceX(g6,g-3) = 8
FEATURE [Part::Extrusion] Extrude010  label="Extrude buco frontale"
  Base = -> Sketch014
  Dir = (0,-1,2e-16)
  DirMode = 2
  FaceMakerClass = Part::FaceMakerBullseye
  FaceMakerMode = 3
  LengthFwd = 11.2
  LengthRev = 0
  Solid = true
  Symmetric = true
FEATURE [Sketcher::SketchObject] Sketch015  label="guida rail"
  ArcFitTolerance = 1e-06
  AttachmentSupport = -> [XZ_Plane]
  ExternalGeometry = -> [Sketch]
  FullyConstrained = true
  MakeInternals = false
  MapMode = 5
  Placement = pos=(0,0,0) rot=(1,0,0;1.5708rad)
  sketch-geometry (4):
    g0: LineSegment StartX=-100.8 StartY=43.2 StartZ=0 EndX=-44.6 EndY=43.2 EndZ=0
    g1: LineSegment StartX=-44.6 StartY=43.2 StartZ=0 EndX=-44.6 EndY=41.2 EndZ=0
    g2: LineSegment StartX=-44.6 StartY=41.2 StartZ=0 EndX=-100.8 EndY=41.2 EndZ=0
    g3: LineSegment StartX=-100.8 StartY=41.2 StartZ=0 EndX=-100.8 EndY=43.2 EndZ=0
  constraints (9):
    c: Horizontal(g0)
    c: Coincident(g1,g0)
    c: Coincident(g2,g1)
    c: Coincident(g3,g2)
    c: Coincident(g3,g0)
    c: Vertical(g3)
    c: Coincident(g2,g-3)
    c: Coincident(g1,g-3)
    c: Coincident(g0,g-4)
FEATURE [Part::Extrusion] Extrude011  label="Extrude guida rail"
  Base = -> Sketch015
  Dir = (0,-1,2e-16)
  DirMode = 2
  FaceMakerClass = Part::FaceMakerBullseye
  FaceMakerMode = 3
  LengthFwd = 9
  LengthRev = 0
  Solid = true
  Symmetric = true
FEATURE [Sketcher::SketchObject] Sketch016  label="guide per coperture laterali"
  ArcFitTolerance = 1e-06
  AttachmentSupport = -> [XZ_Plane]
  ExternalGeometry = -> [Sketch]
  FullyConstrained = true
  MakeInternals = false
  MapMode = 5
  Placement = pos=(0,0,0) rot=(1,0,0;1.5708rad)
  sketch-geometry (14):
    g0: Circle CenterX=-5.6 CenterY=7.6 CenterZ=0 NormalX=0 NormalY=0 NormalZ=1 AngleXU=0 Radius=1.6
    g1: Circle CenterX=-5.6 CenterY=7.6 CenterZ=0 NormalX=0 NormalY=0 NormalZ=1 AngleXU=0 Radius=4
    g2: Circle CenterX=-5.6 CenterY=34.8 CenterZ=0 NormalX=0 NormalY=0 NormalZ=1 AngleXU=0 Radius=1.6
    g3: Circle CenterX=-5.6 CenterY=34.8 CenterZ=0 NormalX=0 NormalY=0 NormalZ=1 AngleXU=0 Radius=4
    g4: Circle CenterX=-184.08 CenterY=34.8 CenterZ=0 NormalX=0 NormalY=0 NormalZ=1 AngleXU=0 Radius=1.6
    g5: Circle CenterX=-184.08 CenterY=34.8 CenterZ=0 NormalX=0 NormalY=0 NormalZ=1 AngleXU=0 Radius=4
    g6: Circle CenterX=-179.305 CenterY=-76.8316 CenterZ=0 NormalX=0 NormalY=0 NormalZ=1 AngleXU=0 Radius=1.6
    g7: Circle CenterX=-179.305 CenterY=-76.8316 CenterZ=0 NormalX=0 NormalY=0 NormalZ=1 AngleXU=0 Radius=4
    g8: Circle CenterX=-213.443 CenterY=-76.8316 CenterZ=0 NormalX=0 NormalY=0 NormalZ=1 AngleXU=0 Radius=1.6
    g9: Circle CenterX=-213.443 CenterY=-76.8316 CenterZ=0 NormalX=0 NormalY=0 NormalZ=1 AngleXU=0 Radius=4
    g10: Circle CenterX=-78.51 CenterY=7.6 CenterZ=0 NormalX=0 NormalY=0 NormalZ=1 AngleXU=0 Radius=1.6
    g11: Circle CenterX=-78.51 CenterY=7.6 CenterZ=0 NormalX=0 NormalY=0 NormalZ=1 AngleXU=0 Radius=4
    g12: Circle CenterX=-78.51 CenterY=34.8 CenterZ=0 NormalX=0 NormalY=0 NormalZ=1 AngleXU=0 Radius=1.6
    g13: Circle CenterX=-78.51 CenterY=34.8 CenterZ=0 NormalX=0 NormalY=0 NormalZ=1 AngleXU=0 Radius=4
  constraints (35):
    c: Diameter(g0) = 3.2
    c: Diameter(g1) = 8
    c: Coincident(g0,g1)
    c: Diameter(g2) = 3.2
    c: Diameter(g3) = 8
    c: Coincident(g3,g2)
    c: Tangent(g2,g-7)
    c: Diameter(g4) = 3.2
    c: Diameter(g5) = 8
    c: Coincident(g5,g4)
    c: Tangent(g4,g-7)
    c: Tangent(g4,g-8)
    c: Diameter(g6) = 3.2
    c: Diameter(g7) = 8
    c: Coincident(g7,g6)
    c: Tangent(g6,g-9)
    c: Tangent(g6,g-10)
    c: Diameter(g8) = 3.2
    c: Diameter(g9) = 8
    c: Coincident(g9,g8)
    c: Tangent(g8,g-10)
    c: Tangent(g8,g-11)
    c: Diameter(g10) = 3.2
    c: Diameter(g11) = 8
    c: Diameter(g12) = 3.2
    c: Diameter(g13) = 8
    c: Coincident(g12,g13)
    c: Coincident(g10,g11)
    c: Tangent(g12,g-7)
    c: DistanceX(g12,g10) = 0
    c: Tangent(g2,g-6)
    c: Tangent(g0,g-6)
    c: Tangent(g0,g-3)
    c: Tangent(g10,g-3)
    c: Tangent(g10,g-4)
FEATURE [Part::Extrusion] Extrude012  label="extrude guide per coperture laterali"
  Base = -> Sketch016
  Dir = (0,-1,2e-16)
  DirMode = 2
  FaceMakerClass = Part::FaceMakerBullseye
  FaceMakerMode = 3
  LengthFwd = 25.2
  LengthRev = 0
  Solid = true
  Symmetric = true
FEATURE [Sketcher::SketchObject] Sketch017  label="supporto CAM"
  ArcFitTolerance = 1e-06
  AttachmentSupport = -> [XZ_Plane]
  ExternalGeometry = -> [Sketch]
  FullyConstrained = true
  MakeInternals = false
  MapMode = 5
  Placement = pos=(0,0,0) rot=(1,0,0;1.5708rad)
  sketch-geometry (6):
    g0: LineSegment StartX=-2.4 StartY=48 StartZ=0 EndX=-2.4 EndY=41.2 EndZ=0
    g1: LineSegment StartX=-2.4 StartY=48 StartZ=0 EndX=-34 EndY=48 EndZ=0
    g2: LineSegment StartX=-34 StartY=48 StartZ=0 EndX=-34 EndY=46.72 EndZ=0
    g3: LineSegment StartX=-34 StartY=46.72 StartZ=0 EndX=-36 EndY=46.72 EndZ=0
    g4: LineSegment StartX=-36 StartY=46.72 StartZ=0 EndX=-36 EndY=41.2 EndZ=0
    g5: LineSegment StartX=-36 StartY=41.2 StartZ=0 EndX=-2.4 EndY=41.2 EndZ=0
  constraints (15):
    c: Coincident(g1,g0)
    c: Horizontal(g1)
    c: Coincident(g2,g1)
    c: Vertical(g2)
    c: Coincident(g3,g2)
    c: Horizontal(g3)
    c: Coincident(g4,g3)
    c: Coincident(g5,g4)
    c: DistanceX(g1,g0) = 31.6
    c: Coincident(g5,g0)
    c: Vertical(g4)
    c: DistanceY(g2,g1) = 1.28
    c: Coincident(g0,g-3)
    c: Coincident(g0,g-3)
    c: Coincident(g4,g-4)
FEATURE [Part::Extrusion] Extrude013  label="Extrude supporto CAM"
  Base = -> Sketch017
  Dir = (0,-1,2e-16)
  DirMode = 2
  FaceMakerClass = Part::FaceMakerBullseye
  FaceMakerMode = 3
  LengthFwd = 17.8
  LengthRev = 0
  Solid = true
  Symmetric = true
FEATURE [Sketcher::SketchObject] Sketch018  label="Scavo CAM"
  ArcFitTolerance = 1e-06
  AttachmentSupport = -> [YZ_Plane]
  ExternalGeometry = -> [Sketch]
  FullyConstrained = true
  MakeInternals = false
  MapMode = 5
  Placement = pos=(0,0,0) rot=(0.57735,0.57735,0.57735;2.0944rad)
  sketch-geometry (4):
    g0: LineSegment StartX=-7.73 StartY=48 StartZ=0 EndX=7.73 EndY=48 EndZ=0
    g1: LineSegment [constr] StartX=1.07e-14 StartY=48 StartZ=0 EndX=0 EndY=43.5155 EndZ=0
    g2: ArcOfCircle CenterX=9e-15 CenterY=52.42 CenterZ=0 NormalX=0 NormalY=0 NormalZ=1 AngleXU=0 Radius=8.90445 StartAngle=3.66102 EndAngle=5.76376
    g3: Circle [constr] CenterX=9e-15 CenterY=52.42 CenterZ=0 NormalX=0 NormalY=0 NormalZ=1 AngleXU=0 Radius=8.9
  constraints (13):
    c: Horizontal(g0)
    c: DistanceY(g-3,g0) = 0
    c: DistanceX(g0,g0) = 15.46
    c: DistanceX(g0,g-3) = 7.73
    c: DistanceX(g-3) = 0
    c: Coincident(g1,g-3)
    c: PointOnObject(g1,g-2)
    c: Coincident(g2,g0)
    c: Coincident(g2,g0)
    c: PointOnObject(g1,g2)
    c: Diameter(g3) = 17.8
    c: DistanceY(g1,g3) = 4.42
    c: Coincident(g2,g3)
FEATURE [Part::Extrusion] Extrude014  label="Extrude Scavo CAM"
  Base = -> Sketch018
  Dir = (1,0,0)
  DirMode = 2
  FaceMakerClass = Part::FaceMakerBullseye
  FaceMakerMode = 3
  LengthFwd = -34
  LengthRev = 0
  Solid = true
  Symmetric = false
FEATURE [Sketcher::SketchObject] Sketch019  label="scavo rumble"
  ArcFitTolerance = 1e-06
  AttachmentSupport = -> [XZ_Plane]
  ExternalGeometry = -> [Sketch]
  FullyConstrained = true
  MakeInternals = false
  MapMode = 5
  Placement = pos=(0,0,0) rot=(1,0,0;1.5708rad)
  sketch-geometry (6):
    g0: LineSegment StartX=-163.771 StartY=-21.9058 StartZ=0 EndX=-158.636 EndY=-23.5745 EndZ=0
    g1: LineSegment StartX=-158.636 StartY=-23.5745 StartZ=0 EndX=-165.743 EndY=-45.4488 EndZ=0
    g2: LineSegment StartX=-165.743 StartY=-45.4488 StartZ=0 EndX=-170.879 EndY=-43.7801 EndZ=0
    g3: LineSegment StartX=-170.879 StartY=-43.7801 StartZ=0 EndX=-163.771 EndY=-21.9058 EndZ=0
    g4: LineSegment [constr] StartX=-145.51 StartY=22 StartZ=0 EndX=-160.157 EndY=-23.0801 EndZ=0
    g5: LineSegment [constr] StartX=-158.636 StartY=-23.5745 StartZ=0 EndX=-160.157 EndY=-23.0801 EndZ=0
  constraints (17):
    c: Coincident(g1,g0)
    c: Coincident(g2,g1)
    c: Coincident(g3,g2)
    c: Coincident(g3,g0)
    c: Parallel(g3,g-3)
    c: Parallel(g3,g1)
    c: Perpendicular(g3,g0)
    c: Perpendicular(g2,g3)
    c: Distance(g2,g0) = 23
    c: Parallel(g4,g-3)
    c: Distance(g4) = 47.4
    c: Coincident(g4,g-3)
    c: Parallel(g5,g0)
    c: Distance(g5) = 1.6
    c: Coincident(g5,g0)
    c: Distance(g5,g0) = 3.8
    c: Coincident(g5,g4)
FEATURE [Part::Extrusion] Extrude015  label="scavo rumble001"
  Base = -> Sketch019
  Dir = (0,-1,2e-16)
  DirMode = 2
  FaceMakerClass = Part::FaceMakerBullseye
  FaceMakerMode = 3
  LengthFwd = 21
  LengthRev = 0
  Solid = true
  Symmetric = true
FEATURE [Sketcher::SketchObject] Sketch020  label="fermo rumble"
  ArcFitTolerance = 1e-06
  AttachmentSupport = -> [XZ_Plane]
  ExternalGeometry = -> [Sketch019,Sketch]
  FullyConstrained = true
  MakeInternals = false
  MapMode = 5
  Placement = pos=(0,0,0) rot=(1,0,0;1.5708rad)
  sketch-geometry (16):
    g0: LineSegment [constr] StartX=-165.905 StartY=-40.7697 StartZ=0 EndX=-167.265 EndY=-44.9544 EndZ=0
    g1: LineSegment [constr] StartX=-167.265 StartY=-44.9544 StartZ=0 EndX=-165.743 EndY=-45.4488 EndZ=0
    g2: LineSegment StartX=-167.318 StartY=-37.9976 StartZ=0 EndX=-165.225 EndY=-38.6774 EndZ=0
    g3: LineSegment StartX=-165.225 StartY=-38.6774 StartZ=0 EndX=-165.905 EndY=-40.7697 EndZ=0
    g4: LineSegment StartX=-165.905 StartY=-40.7697 StartZ=0 EndX=-167.997 EndY=-40.0899 EndZ=0
    g5: LineSegment StartX=-167.997 StartY=-40.0899 StartZ=0 EndX=-167.318 EndY=-37.9976 EndZ=0
    g6: LineSegment StartX=-166.823 StartY=-36.4759 StartZ=0 EndX=-163.399 EndY=-37.5883 EndZ=0
    g7: LineSegment StartX=-163.399 StartY=-37.5883 StartZ=0 EndX=-165.006 EndY=-42.5338 EndZ=0
    g8: LineSegment StartX=-165.006 StartY=-42.5338 StartZ=0 EndX=-168.43 EndY=-41.4214 EndZ=0
    g9: LineSegment StartX=-169.457 StartY=-39.4053 StartZ=0 EndX=-168.839 EndY=-37.5031 EndZ=0
    g10: LineSegment [constr] StartX=-168.839 StartY=-37.5031 StartZ=0 EndX=-168.345 EndY=-35.9815 EndZ=0
    g11: LineSegment [constr] StartX=-168.345 StartY=-35.9815 StartZ=0 EndX=-166.823 EndY=-36.4759 EndZ=0
    g12: ArcOfCircle CenterX=-167.936 CenterY=-39.8997 CenterZ=0 NormalX=0 NormalY=0 NormalZ=1 AngleXU=0 Radius=1.6 StartAngle=2.82743 EndAngle=4.39823
    g13: GeomPoint [constr] X=-169.952 Y=-40.9269 Z=0
    g14: ArcOfCircle CenterX=-167.318 CenterY=-37.9976 CenterZ=0 NormalX=0 NormalY=0 NormalZ=1 AngleXU=0 Radius=1.6 StartAngle=1.25664 EndAngle=2.82743
    g15: GeomPoint [constr] X=-168.345 Y=-35.9815 Z=0
  constraints (42):
    c: Parallel(g0,g-4)
    c: Distance(g0) = 4.4
    c: Coincident(g1,g0)
    c: Perpendicular(g0,g1)
    c: Distance(g1) = 1.6
    c: Coincident(g1,g-5)
    c: Coincident(g3,g2)
    c: Coincident(g4,g3)
    c: Coincident(g5,g4)
    c: Coincident(g5,g2)
    c: Parallel(g3,g-4)
    c: Parallel(g3,g5)
    c: Perpendicular(g2,g3)
    c: Parallel(g4,g2)
    c: Distance(g2) = 2.2
    c: Distance(g3) = 2.2
    c: Coincident(g7,g6)
    c: Coincident(g8,g7)
    c: Parallel(g7,g-4)
    c: Parallel(g7,g9)
    c: Perpendicular(g6,g7)
    c: Parallel(g6,g8)
    c: Distance(g6,g15) = 5.2
    c: Distance(g7) = 5.2
    c: Coincident(g11,g10)
    c: Parallel(g10,g9)
    c: Parallel(g11,g6)
    c: Distance(g10) = 1.6
    c: Distance(g11) = 1.6
    c: Coincident(g10,g15)
    c: Distance(g11,g2) = 1.6
    c: Distance(g2,g10) = 1.6
    c: PointOnObject(g13,g8)
    c: PointOnObject(g13,g9)
    c: Tangent(g8,g12) = 1.5708
    c: Tangent(g9,g12) = 1.5708
    c: PointOnObject(g15,g9)
    c: Tangent(g6,g14) = 1.5708
    c: Tangent(g9,g14) = 1.5708
    c: Equal(g12,g14)
    c: Coincident(g6,g11)
    c: Coincident(g3,g0)
FEATURE [Part::Extrusion] Extrude016  label="Extrude fermo rumble"
  Base = -> Sketch020
  Dir = (0,-1,2e-16)
  DirMode = 2
  FaceMakerClass = Part::FaceMakerBullseye
  FaceMakerMode = 3
  LengthFwd = 25.2
  LengthRev = 0
  Solid = true
  Symmetric = true
FEATURE [Sketcher::SketchObject] Sketch021  label="perno fermo rumble001"
  ArcFitTolerance = 1e-06
  AttachmentSupport = -> [XZ_Plane001]
  FullyConstrained = true
  MakeInternals = false
  MapMode = 5
  Placement = pos=(0,0,0) rot=(1,0,0;1.5708rad)
  sketch-geometry (16):
    g0: LineSegment StartX=0 StartY=0.45 StartZ=0 EndX=0 EndY=1.55 EndZ=0
    g1: LineSegment StartX=0.45 StartY=2 StartZ=0 EndX=1.55 EndY=2 EndZ=0
    g2: LineSegment StartX=2 StartY=1.55 StartZ=0 EndX=2 EndY=0.45 EndZ=0
    g3: LineSegment StartX=1.55 StartY=0 StartZ=0 EndX=0.45 EndY=0 EndZ=0
    g4: ArcOfCircle [constr] CenterX=0.45 CenterY=1.55 CenterZ=0 NormalX=0 NormalY=0 NormalZ=1 AngleXU=0 Radius=0.45 StartAngle=1.5708 EndAngle=3.14159
    g5: GeomPoint [constr] X=0 Y=2 Z=0
    g6: LineSegment StartX=0.45 StartY=2 StartZ=0 EndX=0 EndY=1.55 EndZ=0
    g7: ArcOfCircle [constr] CenterX=1.55 CenterY=1.55 CenterZ=0 NormalX=0 NormalY=0 NormalZ=1 AngleXU=0 Radius=0.45 StartAngle=0 EndAngle=1.5708
    g8: GeomPoint [constr] X=2 Y=2 Z=0
    g9: LineSegment StartX=2 StartY=1.55 StartZ=0 EndX=1.55 EndY=2 EndZ=0
    g10: ArcOfCircle [constr] CenterX=1.55 CenterY=0.45 CenterZ=0 NormalX=0 NormalY=0 NormalZ=1 AngleXU=0 Radius=0.45 StartAngle=4.71239 EndAngle=6.28319
    g11: GeomPoint [constr] X=2 Y=0 Z=0
    g12: LineSegment StartX=1.55 StartY=0 StartZ=0 EndX=2 EndY=0.45 EndZ=0
    g13: ArcOfCircle [constr] CenterX=0.45 CenterY=0.45 CenterZ=0 NormalX=0 NormalY=0 NormalZ=1 AngleXU=0 Radius=0.45 StartAngle=3.14159 EndAngle=4.71239
    g14: GeomPoint [constr] X=0 Y=0 Z=0
    g15: LineSegment StartX=0 StartY=0.45 StartZ=0 EndX=0.45 EndY=0 EndZ=0
  constraints (35):
    c: Coincident(g14,g-1)
    c: PointOnObject(g5,g-2)
    c: Horizontal(g1)
    c: Vertical(g2)
    c: Horizontal(g3)
    c: DistanceX(g5,g8) = 2
    c: DistanceY(g11,g8) = 2
    c: PointOnObject(g5,g0)
    c: PointOnObject(g5,g1)
    c: Tangent(g0,g4) = 1.5708
    c: Tangent(g1,g4) = 1.5708
    c: Coincident(g6,g0)
    c: Coincident(g6,g1)
    c: PointOnObject(g8,g2)
    c: PointOnObject(g8,g1)
    c: Tangent(g2,g7) = 1.5708
    c: Tangent(g1,g7) = 1.5708
    c: Coincident(g9,g2)
    c: Coincident(g9,g1)
    c: PointOnObject(g11,g2)
    c: PointOnObject(g11,g3)
    c: Tangent(g2,g10) = 1.5708
    c: Tangent(g3,g10) = 1.5708
    c: Coincident(g12,g2)
    c: Coincident(g12,g3)
    c: PointOnObject(g14,g0)
    c: PointOnObject(g14,g3)
    c: Tangent(g0,g13) = 1.5708
    c: Tangent(g3,g13) = 1.5708
    c: Coincident(g15,g0)
    c: Coincident(g15,g3)
    c: Equal(g6,g9)
    c: Equal(g9,g12)
    c: Equal(g12,g15)
    c: DistanceX(g14,g3) = 0.45
FEATURE [Sketcher::SketchObject] Sketch022  label="fori per M3x5(OD)x6(L)"
  ArcFitTolerance = 1e-06
  AttachmentSupport = -> [XZ_Plane]
  ExternalGeometry = -> [Sketch016]
  FullyConstrained = true
  MakeInternals = false
  MapMode = 5
  Placement = pos=(0,0,0) rot=(1,0,0;1.5708rad)
  sketch-geometry (7):
    g0: Circle CenterX=-5.6 CenterY=34.8 CenterZ=0 NormalX=0 NormalY=0 NormalZ=1 AngleXU=0 Radius=2.5
    g1: Circle CenterX=-5.6 CenterY=7.6 CenterZ=0 NormalX=0 NormalY=0 NormalZ=1 AngleXU=0 Radius=2.5
    g2: Circle CenterX=-78.51 CenterY=34.8 CenterZ=0 NormalX=0 NormalY=0 NormalZ=1 AngleXU=0 Radius=2.5
    g3: Circle CenterX=-78.51 CenterY=7.6 CenterZ=0 NormalX=0 NormalY=0 NormalZ=1 AngleXU=0 Radius=2.5
    g4: Circle CenterX=-184.08 CenterY=34.8 CenterZ=0 NormalX=0 NormalY=0 NormalZ=1 AngleXU=0 Radius=2.5
    g5: Circle CenterX=-179.305 CenterY=-76.8316 CenterZ=0 NormalX=0 NormalY=0 NormalZ=1 AngleXU=0 Radius=2.5
    g6: Circle CenterX=-213.443 CenterY=-76.8316 CenterZ=0 NormalX=0 NormalY=0 NormalZ=1 AngleXU=0 Radius=2.5
  constraints (14):
    c: Diameter(g0) = 5
    c: Diameter(g1) = 5
    c: Diameter(g2) = 5
    c: Diameter(g3) = 5
    c: Diameter(g4) = 5
    c: Diameter(g5) = 5
    c: Diameter(g6) = 5
    c: Coincident(g0,g-8)
    c: Coincident(g1,g-9)
    c: Coincident(g2,g-6)
    c: Coincident(g3,g-7)
    c: Coincident(g4,g-5)
    c: Coincident(g5,g-4)
    c: Coincident(g6,g-3)
FEATURE [Part::Extrusion] Extrude018  label="Extrude fori M3x5x6 - dx"
  Base = -> Sketch022
  Dir = (0,-1,2e-16)
  DirMode = 2
  FaceMakerClass = Part::FaceMakerBullseye
  FaceMakerMode = 3
  LengthFwd = 6.2
  LengthRev = 0
  Placement = pos=(0,-9.5,0) rot=(0,0,1;0rad)
  Solid = true
  Symmetric = true
FEATURE [Part::Extrusion] Extrude019  label="Extrude fori M3x5x6 - sx"
  Base = -> Sketch022
  Dir = (0,-1,2e-16)
  DirMode = 2
  FaceMakerClass = Part::FaceMakerBullseye
  FaceMakerMode = 3
  LengthFwd = 6.2
  LengthRev = 0
  Placement = pos=(0,9.5,0) rot=(0,0,1;0rad)
  Solid = true
  Symmetric = true
FEATURE [Sketcher::SketchObject] Sketch023  label="foro anteriore M3x5x6"
  ArcFitTolerance = 1e-06
  AttachmentSupport = -> [YZ_Plane]
  FullyConstrained = true
  MakeInternals = false
  MapMode = 5
  Placement = pos=(0,0,0) rot=(0.57735,0.57735,0.57735;2.0944rad)
  sketch-geometry (2):
    g0: LineSegment [constr] StartX=0 StartY=0 StartZ=0 EndX=0 EndY=38.6 EndZ=0
    g1: Circle CenterX=0 CenterY=38.6 CenterZ=0 NormalX=0 NormalY=0 NormalZ=1 AngleXU=0 Radius=2.5
  constraints (5):
    c: Coincident(g0,g-1)
    c: PointOnObject(g0,g-2)
    c: DistanceY(g0,g0) = 38.6
    c: Diameter(g1) = 5
    c: Coincident(g1,g0)
FEATURE [Part::Extrusion] Extrude020  label="Extrude foro anteriore M3x5x6"
  Base = -> Sketch023
  Dir = (1,0,0)
  DirMode = 2
  FaceMakerClass = Part::FaceMakerBullseye
  FaceMakerMode = 3
  LengthFwd = -6.2
  LengthRev = 0
  Solid = true
  Symmetric = false
FEATURE [Sketcher::SketchObject] Sketch024  label="fori per viti frontale"
  ArcFitTolerance = 1e-06
  AttachmentSupport = -> [YZ_Plane]
  FullyConstrained = true
  MakeInternals = false
  MapMode = 5
  Placement = pos=(0,0,0) rot=(0.57735,0.57735,0.57735;2.0944rad)
  sketch-geometry (9):
    g0: LineSegment [constr] StartX=-10.3 StartY=30.721 StartZ=0 EndX=10.3 EndY=30.721 EndZ=0
    g1: LineSegment [constr] StartX=10.3 StartY=30.721 StartZ=0 EndX=10.3 EndY=10.121 EndZ=0
    g2: LineSegment [constr] StartX=10.3 StartY=10.121 StartZ=0 EndX=-10.3 EndY=10.121 EndZ=0
    g3: LineSegment [constr] StartX=-10.3 StartY=10.121 StartZ=0 EndX=-10.3 EndY=30.721 EndZ=0
    g4: LineSegment [constr] StartX=0 StartY=0 StartZ=0 EndX=0 EndY=10.121 EndZ=0
    g5: Circle CenterX=-10.3 CenterY=30.721 CenterZ=0 NormalX=0 NormalY=0 NormalZ=1 AngleXU=0 Radius=2
    g6: Circle CenterX=10.3 CenterY=30.721 CenterZ=0 NormalX=0 NormalY=0 NormalZ=1 AngleXU=0 Radius=2
    g7: Circle CenterX=-10.3 CenterY=10.121 CenterZ=0 NormalX=0 NormalY=0 NormalZ=1 AngleXU=0 Radius=2
    g8: Circle CenterX=10.3 CenterY=10.121 CenterZ=0 NormalX=0 NormalY=0 NormalZ=1 AngleXU=0 Radius=2
  constraints (22):
    c: Horizontal(g0)
    c: Coincident(g1,g0)
    c: Vertical(g1)
    c: Coincident(g2,g1)
    c: Horizontal(g2)
    c: Coincident(g3,g2)
    c: Coincident(g3,g0)
    c: Vertical(g3)
    c: DistanceX(g0,g0) = 20.6
    c: DistanceY(g3,g3) = 20.6
    c: Coincident(g4,g-1)
    c: PointOnObject(g4,g-2)
    c: DistanceY(g4,g4) = 10.121
    c: Symmetric(g2,g2,g4)
    c: Diameter(g5) = 4
    c: Diameter(g6) = 4
    c: Diameter(g7) = 4
    c: Diameter(g8) = 4
    c: Coincident(g5,g0)
    c: Coincident(g6,g0)
    c: Coincident(g7,g2)
    c: Coincident(g8,g1)
FEATURE [Part::Extrusion] Extrude021  label="Extrude fori per viti frontale"
  Base = -> Sketch024
  Dir = (1,0,0)
  DirMode = 2
  FaceMakerClass = Part::FaceMakerBullseye
  FaceMakerMode = 3
  LengthFwd = -2.4
  LengthRev = 0
  Solid = true
  Symmetric = false
FEATURE [Sketcher::SketchObject] Sketch025  label="foro per filo CAM"
  ArcFitTolerance = 1e-06
  AttachmentSupport = -> [XZ_Plane]
  ExternalGeometry = -> [Sketch]
  FullyConstrained = true
  MakeInternals = false
  MapMode = 5
  Placement = pos=(0,0,0) rot=(1,0,0;1.5708rad)
  sketch-geometry (4):
    g0: LineSegment StartX=-44.6 StartY=41.2 StartZ=0 EndX=-44.6 EndY=36.4 EndZ=0
    g1: LineSegment StartX=-44.6 StartY=36.4 StartZ=0 EndX=-54.6 EndY=36.4 EndZ=0
    g2: LineSegment StartX=-54.6 StartY=36.4 StartZ=0 EndX=-50.4 EndY=41.2 EndZ=0
    g3: LineSegment StartX=-50.4 StartY=41.2 StartZ=0 EndX=-44.6 EndY=41.2 EndZ=0
  constraints (11):
    c: Vertical(g0)
    c: Coincident(g1,g0)
    c: Horizontal(g1)
    c: Coincident(g2,g1)
    c: Coincident(g3,g2)
    c: Coincident(g3,g0)
    c: Horizontal(g3)
    c: Coincident(g0,g-3)
    c: DistanceY(g0,g-4) = 0
    c: DistanceX(g3,g3) = 5.8
    c: DistanceX(g1,g1) = 10
FEATURE [Part::Extrusion] Extrude022  label="Extrude foro per filo CAM dx"
  Base = -> Sketch025
  Dir = (0,-1,2e-16)
  DirMode = 2
  FaceMakerClass = Part::FaceMakerBullseye
  FaceMakerMode = 3
  LengthFwd = 4.9
  LengthRev = 0
  Placement = pos=(0,6.95,0) rot=(0,0,1;0rad)
  Solid = true
  Symmetric = true
FEATURE [Part::Extrusion] Extrude023  label="Extrude foro per filo CAM sx"
  Base = -> Sketch025
  Dir = (0,-1,2e-16)
  DirMode = 2
  FaceMakerClass = Part::FaceMakerBullseye
  FaceMakerMode = 3
  LengthFwd = 4.9
  LengthRev = 0
  Placement = pos=(0,-6.95,0) rot=(0,0,1;0rad)
  Solid = true
  Symmetric = true
FEATURE [Sketcher::SketchObject] Sketch026  label="foro sotto anteriore M3x5x6"
  ArcFitTolerance = 1e-06
  AttachmentSupport = -> [XY_Plane]
  FullyConstrained = true
  MakeInternals = false
  MapMode = 5
  sketch-geometry (2):
    g0: LineSegment [constr] StartX=0 StartY=0 StartZ=0 EndX=-16.5 EndY=0 EndZ=0
    g1: Circle CenterX=-16.5 CenterY=0 CenterZ=0 NormalX=0 NormalY=0 NormalZ=1 AngleXU=0 Radius=2.5
  constraints (5):
    c: Distance(g0) = 16.5
    c: Coincident(g0,g-1)
    c: PointOnObject(g0,g-1)
    c: Diameter(g1) = 5
    c: Coincident(g0,g1)
FEATURE [Sketcher::SketchObject] Sketch027  label="foro sotto posteriore M3x5x6"
  ArcFitTolerance = 1e-06
  AttachmentSupport = -> [XY_Plane]
  ExternalGeometry = -> [Sketch]
  FullyConstrained = true
  MakeInternals = false
  MapMode = 5
  sketch-geometry (2):
    g0: LineSegment [constr] StartX=-82.8 StartY=2e-16 StartZ=0 EndX=-71.3 EndY=2e-16 EndZ=0
    g1: Circle CenterX=-71.3 CenterY=2e-16 CenterZ=0 NormalX=0 NormalY=0 NormalZ=1 AngleXU=0 Radius=2.5
  constraints (5):
    c: Distance(g0) = 11.5
    c: Coincident(g0,g-3)
    c: PointOnObject(g0,g-3)
    c: Diameter(g1) = 5
    c: Coincident(g1,g0)
FEATURE [Sketcher::SketchObject] Sketch029  label="fori sotto impugnatura"
  ArcFitTolerance = 1e-06
  AttachmentSupport = -> [XY_Plane]
  ExternalGeometry = -> [Sketch]
  FullyConstrained = true
  MakeInternals = false
  MapMode = 5
  sketch-geometry (15):
    g0: LineSegment [constr] StartX=-175.232 StartY=-1.83e-14 StartZ=0 EndX=-191.232 EndY=0 EndZ=0
    g1: Circle CenterX=-191.232 CenterY=0 CenterZ=0 NormalX=0 NormalY=0 NormalZ=1 AngleXU=0 Radius=3.95
    g2: LineSegment [constr] StartX=-175.232 StartY=-1.83e-14 StartZ=0 EndX=-204.275 EndY=0 EndZ=0
    g3: LineSegment StartX=-204.275 StartY=3.525 StartZ=0 EndX=-204.275 EndY=-3.525 EndZ=0
    g4: LineSegment StartX=-205.4 StartY=-4.65 StartZ=0 EndX=-206.65 EndY=-4.65 EndZ=0
    g5: LineSegment StartX=-207.775 StartY=-3.525 StartZ=0 EndX=-207.775 EndY=3.525 EndZ=0
    g6: LineSegment StartX=-206.65 StartY=4.65 StartZ=0 EndX=-205.4 EndY=4.65 EndZ=0
    g7: ArcOfCircle CenterX=-206.65 CenterY=3.525 CenterZ=0 NormalX=0 NormalY=0 NormalZ=1 AngleXU=0 Radius=1.125 StartAngle=1.5708 EndAngle=3.14159
    g8: GeomPoint [constr] X=-207.775 Y=4.65 Z=0
    g9: ArcOfCircle CenterX=-205.4 CenterY=3.525 CenterZ=0 NormalX=0 NormalY=0 NormalZ=1 AngleXU=0 Radius=1.125 StartAngle=0 EndAngle=1.5708
    g10: GeomPoint [constr] X=-204.275 Y=4.65 Z=0
    g11: ArcOfCircle CenterX=-205.4 CenterY=-3.525 CenterZ=0 NormalX=0 NormalY=0 NormalZ=1 AngleXU=0 Radius=1.125 StartAngle=4.71239 EndAngle=6.28319
    g12: GeomPoint [constr] X=-204.275 Y=-4.65 Z=0
    g13: ArcOfCircle CenterX=-206.65 CenterY=-3.525 CenterZ=0 NormalX=0 NormalY=0 NormalZ=1 AngleXU=0 Radius=1.125 StartAngle=3.14159 EndAngle=4.71239
    g14: GeomPoint [constr] X=-207.775 Y=-4.65 Z=0
  constraints (35):
    c: Distance(g0) = 16
    c: Coincident(g0,g-3)
    c: PointOnObject(g0,g-1)
    c: Diameter(g1) = 7.9
    c: Coincident(g1,g0)
    c: Coincident(g2,g0)
    c: PointOnObject(g2,g-1)
    c: Vertical(g3)
    c: Horizontal(g4)
    c: Vertical(g5)
    c: Horizontal(g6)
    c: DistanceY(g12,g10) = 9.3
    c: DistanceX(g8,g10) = 3.5
    c: Symmetric(g10,g12,g2)
    c: PointOnObject(g8,g5)
    c: PointOnObject(g8,g6)
    c: Tangent(g5,g7) = 1.5708
    c: Tangent(g6,g7) = 1.5708
    c: PointOnObject(g10,g3)
    c: PointOnObject(g10,g6)
    c: Tangent(g3,g9) = 1.5708
    c: Tangent(g6,g9) = 1.5708
    c: PointOnObject(g12,g3)
    c: PointOnObject(g12,g4)
    c: Tangent(g3,g11) = 1.5708
    c: Tangent(g4,g11) = 1.5708
    c: PointOnObject(g14,g4)
    c: PointOnObject(g14,g5)
    c: Tangent(g4,g13) = 1.5708
    c: Tangent(g5,g13) = 1.5708
    c: Equal(g7,g9)
    c: Equal(g9,g11)
    c: Equal(g11,g13)
    c: DistanceX(g6,g6) = 1.25
    c: DistanceX(g-5,g5) = 6.8
FEATURE [Sketcher::SketchObject] Sketch030  label="fori superiori per solenoide e oled"
  ArcFitTolerance = 1e-06
  AttachmentSupport = -> [XY_Plane]
  ExternalGeometry = -> [Sketch]
  FullyConstrained = true
  MakeInternals = false
  MapMode = 5
  sketch-geometry (33):
    g0: LineSegment [constr] StartX=-181.6 StartY=1.12e-14 StartZ=0 EndX=-169.91 EndY=0 EndZ=0
    g1: LineSegment [constr] StartX=-169.91 StartY=0 StartZ=0 EndX=-169.91 EndY=-2.6 EndZ=0
    g2: LineSegment [constr] StartX=-169.91 StartY=0 StartZ=0 EndX=-169.91 EndY=2.6 EndZ=0
    g3: LineSegment StartX=-169.91 StartY=4.975 StartZ=0 EndX=-169.91 EndY=8.225 EndZ=0
    g4: LineSegment StartX=-167.535 StartY=10.6 StartZ=0 EndX=-167.285 EndY=10.6 EndZ=0
    g5: LineSegment StartX=-164.91 StartY=8.225 StartZ=0 EndX=-164.91 EndY=4.975 EndZ=0
    g6: LineSegment StartX=-167.285 StartY=2.6 StartZ=0 EndX=-167.535 EndY=2.6 EndZ=0
    g7: LineSegment StartX=-169.91 StartY=-4.975 StartZ=0 EndX=-169.91 EndY=-8.225 EndZ=0
    g8: LineSegment StartX=-167.535 StartY=-10.6 StartZ=0 EndX=-167.285 EndY=-10.6 EndZ=0
    g9: LineSegment StartX=-164.91 StartY=-8.225 StartZ=0 EndX=-164.91 EndY=-4.975 EndZ=0
    g10: LineSegment StartX=-167.285 StartY=-2.6 StartZ=0 EndX=-167.535 EndY=-2.6 EndZ=0
    g11: ArcOfCircle CenterX=-167.535 CenterY=8.225 CenterZ=0 NormalX=0 NormalY=0 NormalZ=1 AngleXU=0 Radius=2.375 StartAngle=1.5708 EndAngle=3.14159
    g12: GeomPoint [constr] X=-169.91 Y=10.6 Z=0
    g13: ArcOfCircle CenterX=-167.285 CenterY=8.225 CenterZ=0 NormalX=0 NormalY=0 NormalZ=1 AngleXU=0 Radius=2.375 StartAngle=0 EndAngle=1.5708
    g14: GeomPoint [constr] X=-164.91 Y=10.6 Z=0
    g15: ArcOfCircle CenterX=-167.285 CenterY=4.975 CenterZ=0 NormalX=0 NormalY=0 NormalZ=1 AngleXU=0 Radius=2.375 StartAngle=4.71239 EndAngle=6.28319
    g16: GeomPoint [constr] X=-164.91 Y=2.6 Z=0
    g17: ArcOfCircle CenterX=-167.535 CenterY=4.975 CenterZ=0 NormalX=0 NormalY=0 NormalZ=1 AngleXU=0 Radius=2.375 StartAngle=3.14159 EndAngle=4.71239
    g18: GeomPoint [constr] X=-169.91 Y=2.6 Z=0
    g19: ArcOfCircle CenterX=-167.535 CenterY=-4.975 CenterZ=0 NormalX=0 NormalY=0 NormalZ=1 AngleXU=0 Radius=2.375 StartAngle=1.5708 EndAngle=3.14159
    g20: GeomPoint [constr] X=-169.91 Y=-2.6 Z=0
    g21: ArcOfCircle CenterX=-167.285 CenterY=-4.975 CenterZ=0 NormalX=0 NormalY=0 NormalZ=1 AngleXU=0 Radius=2.375 StartAngle=0 EndAngle=1.5708
    g22: GeomPoint [constr] X=-164.91 Y=-2.6 Z=0
    g23: ArcOfCircle CenterX=-167.285 CenterY=-8.225 CenterZ=0 NormalX=0 NormalY=0 NormalZ=1 AngleXU=0 Radius=2.375 StartAngle=4.71239 EndAngle=6.28319
    g24: GeomPoint [constr] X=-164.91 Y=-10.6 Z=0
    g25: ArcOfCircle CenterX=-167.535 CenterY=-8.225 CenterZ=0 NormalX=0 NormalY=0 NormalZ=1 AngleXU=0 Radius=2.375 StartAngle=3.14159 EndAngle=4.71239
    g26: GeomPoint [constr] X=-169.91 Y=-10.6 Z=0
    g27: LineSegment [constr] StartX=-181.6 StartY=1.12e-14 StartZ=0 EndX=-152.209 EndY=0 EndZ=0
    g28: LineSegment [constr] StartX=-181.6 StartY=1.12e-14 StartZ=0 EndX=-130.41 EndY=0 EndZ=0
    g29: LineSegment [constr] StartX=-152.209 StartY=0 StartZ=0 EndX=-152.209 EndY=6.95 EndZ=0
    g30: LineSegment [constr] StartX=-130.41 StartY=0 StartZ=0 EndX=-130.41 EndY=-6.95 EndZ=0
    g31: Circle CenterX=-152.209 CenterY=6.95 CenterZ=0 NormalX=0 NormalY=0 NormalZ=1 AngleXU=0 Radius=2.1
    g32: Circle CenterX=-130.41 CenterY=-6.95 CenterZ=0 NormalX=0 NormalY=0 NormalZ=1 AngleXU=0 Radius=2.1
  constraints (79):
    c: Distance(g0) = 11.69
    c: PointOnObject(g0,g-1)
    c: Coincident(g-4,g0)
    c: Distance(g1) = 2.6
    c: Coincident(g1,g0)
    c: Vertical(g1)
    c: Distance(g2) = 2.6
    c: Coincident(g2,g0)
    c: Vertical(g2)
    c: Distance(g18,g12) = 8
    c: Coincident(g18,g2)
    c: Vertical(g3)
    c: Distance(g14,g12) = 5
    c: Horizontal(g4)
    c: Distance(g16,g14) = 8
    c: Vertical(g5)
    c: Distance(g26,g20) = 8
    c: Coincident(g20,g1)
    c: Vertical(g7)
    c: Distance(g26,g24) = 5
    c: Horizontal(g8)
    c: Distance(g24,g22) = 8
    c: Vertical(g9)
    c: PointOnObject(g12,g3)
    c: PointOnObject(g12,g4)
    c: Tangent(g3,g11) = 1.5708
    c: Tangent(g4,g11) = 1.5708
    c: PointOnObject(g14,g5)
    c: PointOnObject(g14,g4)
    c: Tangent(g5,g13) = 1.5708
    c: Tangent(g4,g13) = 1.5708
    c: PointOnObject(g16,g5)
    c: PointOnObject(g16,g6)
    c: Tangent(g5,g15) = 1.5708
    c: Tangent(g6,g15) = 1.5708
    c: PointOnObject(g18,g3)
    c: PointOnObject(g18,g6)
    c: Tangent(g3,g17) = 1.5708
    c: Tangent(g6,g17) = 1.5708
    c: Equal(g11,g13)
    c: Equal(g13,g15)
    c: Equal(g15,g17)
    c: DistanceX(g4,g4) = 0.25
    c: PointOnObject(g20,g7)
    c: PointOnObject(g20,g10)
    c: Tangent(g7,g19) = -1.5708
    c: Tangent(g10,g19) = -1.5708
    c: PointOnObject(g22,g9)
    c: PointOnObject(g22,g10)
    c: Tangent(g9,g21) = -1.5708
    c: Tangent(g10,g21) = -1.5708
    c: PointOnObject(g24,g9)
    c: PointOnObject(g24,g8)
    c: Tangent(g9,g23) = -1.5708
    c: Tangent(g8,g23) = -1.5708
    c: PointOnObject(g26,g8)
    c: PointOnObject(g26,g7)
    c: Tangent(g8,g25) = -1.5708
    c: Tangent(g7,g25) = -1.5708
    c: Equal(g19,g21)
    c: Equal(g21,g23)
    c: Equal(g23,g25)
    c: DistanceX(g10,g10) = 0.25
    c: Distance(g27) = 29.391
    c: Coincident(g27,g0)
    c: PointOnObject(g27,g-1)
    c: Distance(g28) = 51.19
    c: Coincident(g28,g0)
    c: PointOnObject(g28,g-1)
    c: Distance(g29) = 6.95
    c: Coincident(g29,g27)
    c: Vertical(g29)
    c: Distance(g30) = 6.95
    c: Coincident(g30,g28)
    c: Vertical(g30)
    c: Diameter(g31) = 4.2
    c: Diameter(g32) = 4.2
    c: Coincident(g32,g30)
    c: Coincident(g31,g29)
FEATURE [Sketcher::SketchObject] Sketch031  label="fori inferiori switch pompa"
  ArcFitTolerance = 1e-06
  AttachmentSupport = -> [XY_Plane]
  ExternalGeometry = -> [Sketch]
  FullyConstrained = true
  MakeInternals = false
  MapMode = 5
  sketch-geometry (4):
    g0: LineSegment [constr] StartX=-57.2 StartY=1.9e-15 StartZ=0 EndX=-62.45 EndY=1.9e-15 EndZ=0
    g1: LineSegment [constr] StartX=-62.45 StartY=3.25 StartZ=0 EndX=-62.45 EndY=-3.25 EndZ=0
    g2: Circle CenterX=-62.45 CenterY=3.25 CenterZ=0 NormalX=0 NormalY=0 NormalZ=1 AngleXU=0 Radius=1.6
    g3: Circle CenterX=-62.45 CenterY=-3.25 CenterZ=0 NormalX=0 NormalY=0 NormalZ=1 AngleXU=0 Radius=1.6
  constraints (10):
    c: Distance(g0) = 5.25
    c: Coincident(g0,g-3)
    c: PointOnObject(g0,g-3)
    c: Vertical(g1)
    c: DistanceY(g1,g1) = 6.5
    c: Symmetric(g1,g1,g0)
    c: Diameter(g2) = 3.2
    c: Diameter(g3) = 3.2
    c: Coincident(g2,g1)
    c: Coincident(g3,g1)
FEATURE [Sketcher::SketchObject] Sketch032  label="spazio per PILA 18650"
  ArcFitTolerance = 1e-06
  AttachmentSupport = -> [XY_Plane]
  ExternalGeometry = -> [Sketch]
  FullyConstrained = true
  MakeInternals = false
  MapMode = 5
  sketch-geometry (2):
    g0: LineSegment [constr] StartX=-178.142 StartY=-1.74e-14 StartZ=0 EndX=-191.142 EndY=-1.83e-14 EndZ=0
    g1: Circle CenterX=-191.142 CenterY=-1.83e-14 CenterZ=0 NormalX=0 NormalY=0 NormalZ=1 AngleXU=0 Radius=10.5
  constraints (5):
    c: Distance(g0) = 13
    c: Coincident(g0,g-3)
    c: PointOnObject(g0,g-4)
    c: Diameter(g1) = 21
    c: Coincident(g1,g0)
FEATURE [Part::Extrusion] Extrude030  label="Extrude spazio per PILA 18650"
  Base = -> Sketch032
  Dir = (0,0,1)
  DirLink = -> Sketch [Edge45]
  DirMode = 2
  FaceMakerClass = Part::FaceMakerBullseye
  FaceMakerMode = 3
  LengthFwd = 76
  LengthRev = 0
  Placement = pos=(6,0,-72) rot=(0,0,1;0rad)
  Solid = true
  Symmetric = false
FEATURE [Sketcher::SketchObject] Sketch033  label="fermo per scheda micro"
  ArcFitTolerance = 1e-06
  AttachmentSupport = -> [XZ_Plane]
  ExternalGeometry = -> [Sketch]
  FullyConstrained = true
  MakeInternals = false
  MapMode = 5
  Placement = pos=(0,0,0) rot=(1,0,0;1.5708rad)
  sketch-geometry (12):
    g0: LineSegment StartX=-11.6 StartY=6 StartZ=0 EndX=-4 EndY=6 EndZ=0
    g1: LineSegment StartX=-4 StartY=6 StartZ=0 EndX=-4 EndY=36.4 EndZ=0
    g2: LineSegment StartX=-4 StartY=36.4 StartZ=0 EndX=-11.6 EndY=36.4 EndZ=0
    g3: LineSegment StartX=-11.6 StartY=36.4 StartZ=0 EndX=-11.6 EndY=6 EndZ=0
    g4: LineSegment StartX=-80.11 StartY=11.6 StartZ=0 EndX=-70.51 EndY=11.6 EndZ=0
    g5: LineSegment StartX=-70.51 StartY=11.6 StartZ=0 EndX=-70.51 EndY=6 EndZ=0
    g6: LineSegment StartX=-70.51 StartY=6 StartZ=0 EndX=-80.11 EndY=6 EndZ=0
    g7: LineSegment StartX=-80.11 StartY=6 StartZ=0 EndX=-80.11 EndY=11.6 EndZ=0
    g8: LineSegment StartX=-78.51 StartY=36.4 StartZ=0 EndX=-70.51 EndY=36.4 EndZ=0
    g9: LineSegment StartX=-70.51 StartY=36.4 StartZ=0 EndX=-70.51 EndY=30.8 EndZ=0
    g10: LineSegment StartX=-70.51 StartY=30.8 StartZ=0 EndX=-78.51 EndY=30.8 EndZ=0
    g11: LineSegment StartX=-78.51 StartY=30.8 StartZ=0 EndX=-78.51 EndY=36.4 EndZ=0
  constraints (33):
    c: Horizontal(g0)
    c: Coincident(g1,g0)
    c: Coincident(g2,g1)
    c: Horizontal(g2)
    c: Coincident(g3,g2)
    c: Coincident(g3,g0)
    c: Vertical(g3)
    c: DistanceX(g2,g2) = 7.6
    c: Coincident(g1,g-3)
    c: Coincident(g0,g-3)
    c: Horizontal(g4)
    c: Coincident(g5,g4)
    c: Vertical(g5)
    c: Coincident(g6,g5)
    c: Horizontal(g6)
    c: Coincident(g7,g6)
    c: Coincident(g7,g4)
    c: Vertical(g7)
    c: DistanceY(g5,g5) = 5.6
    c: DistanceX(g4,g4) = 9.6
    c: Coincident(g9,g8)
    c: Vertical(g9)
    c: Coincident(g10,g9)
    c: Horizontal(g10)
    c: Coincident(g11,g10)
    c: Coincident(g11,g8)
    c: Vertical(g11)
    c: DistanceY(g9,g9) = 5.6
    c: DistanceX(g10,g10) = 8
    c: Coincident(g4,g-4)
    c: DistanceX(g4,g10) = 1.6
    c: Horizontal(g8)
    c: DistanceY(g8,g1) = 0
FEATURE [Sketcher::SketchObject] Sketch034  label="buchi guida rail"
  ArcFitTolerance = 1e-06
  AttachmentSupport = -> [XY_Plane]
  ExternalGeometry = -> [Sketch]
  FullyConstrained = true
  MakeInternals = false
  MapMode = 5
  sketch-geometry (6):
    g0: LineSegment [constr] StartX=-100.8 StartY=9.1e-15 StartZ=0 EndX=-93.3 EndY=0 EndZ=0
    g1: LineSegment [constr] StartX=-93.3 StartY=0 StartZ=0 EndX=-73.3 EndY=0 EndZ=0
    g2: LineSegment [constr] StartX=-73.3 StartY=0 StartZ=0 EndX=-53.3 EndY=0 EndZ=0
    g3: Circle CenterX=-93.3 CenterY=0 CenterZ=0 NormalX=0 NormalY=0 NormalZ=1 AngleXU=0 Radius=2.5
    g4: Circle CenterX=-73.3 CenterY=0 CenterZ=0 NormalX=0 NormalY=0 NormalZ=1 AngleXU=0 Radius=2.5
    g5: Circle CenterX=-53.3 CenterY=0 CenterZ=0 NormalX=0 NormalY=0 NormalZ=1 AngleXU=0 Radius=2.5
  constraints (15):
    c: Distance(g0) = 7.5
    c: Coincident(g0,g-3)
    c: PointOnObject(g0,g-1)
    c: Distance(g1) = 20
    c: Coincident(g1,g0)
    c: PointOnObject(g1,g-1)
    c: Distance(g2) = 20
    c: Coincident(g2,g1)
    c: PointOnObject(g2,g-1)
    c: Diameter(g3) = 5
    c: Diameter(g4) = 5
    c: Diameter(g5) = 5
    c: Coincident(g3,g0)
    c: Coincident(g4,g1)
    c: Coincident(g5,g2)
FEATURE [Part::Extrusion] Extrude032  label="Extrude buchi guida rail"
  Base = -> Sketch034
  Dir = (0,0,1)
  DirMode = 2
  FaceMakerClass = Part::FaceMakerBullseye
  FaceMakerMode = 3
  LengthFwd = -6.2
  LengthRev = 0
  Placement = pos=(0,0,43.2) rot=(0,0,1;0rad)
  Solid = true
  Symmetric = false
FEATURE [Part::Extrusion] Extrude033  label="Extrude fori superiori per solenoide e oled001"
  Base = -> Sketch030
  Dir = (0,0,1)
  DirMode = 2
  FaceMakerClass = Part::FaceMakerBullseye
  FaceMakerMode = 3
  LengthFwd = -4.8
  LengthRev = 0
  Placement = pos=(0,0,41.2) rot=(0,0,1;0rad)
  Solid = true
  Symmetric = false
FEATURE [Part::Extrusion] Extrude034  label="Extrude fori sotto impugnatura001"
  Base = -> Sketch029
  Dir = (0,0,1)
  DirMode = 2
  FaceMakerClass = Part::FaceMakerBullseye
  FaceMakerMode = 3
  LengthFwd = 5
  LengthRev = 0
  Placement = pos=(0,0,-83) rot=(0,0,1;0rad)
  Solid = true
  Symmetric = false
FEATURE [Part::Extrusion] Extrude035  label="Extrude fori inferiori switch pompa001"
  Base = -> Sketch031
  Dir = (0,0,1)
  DirMode = 2
  FaceMakerClass = Part::FaceMakerBullseye
  FaceMakerMode = 3
  LengthFwd = 4
  LengthRev = 0
  Placement = pos=(0,0,-1.7) rot=(0,0,1;0rad)
  Solid = true
  Symmetric = false
FEATURE [Part::Extrusion] Extrude036  label="Extrude foro sotto posteriore M3x5x007"
  Base = -> Sketch027
  Dir = (0,0,1)
  DirMode = 2
  FaceMakerClass = Part::FaceMakerBullseye
  FaceMakerMode = 3
  LengthFwd = 6.2
  LengthRev = 0
  Placement = pos=(0,0,-9.6) rot=(0,0,1;0rad)
  Solid = true
  Symmetric = false
FEATURE [Part::Extrusion] Extrude037  label="Extrude foro sotto anteriore M3x5x007"
  Base = -> Sketch026
  Dir = (0,0,1)
  DirMode = 2
  FaceMakerClass = Part::FaceMakerBullseye
  FaceMakerMode = 3
  LengthFwd = 6.2
  LengthRev = 0
  Solid = true
  Symmetric = false
FEATURE [Sketcher::SketchObject] Sketch035  label="foro per fissaggio micro"
  ArcFitTolerance = 1e-06
  AttachmentSupport = -> [XZ_Plane]
  ExternalGeometry = -> [Sketch,Sketch033]
  FullyConstrained = true
  MakeInternals = false
  MapMode = 5
  Placement = pos=(0,0,0) rot=(1,0,0;1.5708rad)
  sketch-geometry (3):
    g0: Circle CenterX=-7.8 CenterY=21.2 CenterZ=0 NormalX=0 NormalY=0 NormalZ=1 AngleXU=0 Radius=1.6
    g1: GeomPoint [constr] X=-4 Y=21.2 Z=0
    g2: LineSegment [constr] StartX=-4 StartY=21.2 StartZ=0 EndX=-11.6 EndY=21.2 EndZ=0
  constraints (6):
    c: Diameter(g0) = 3.2
    c: Symmetric(g-3,g-3,g1)
    c: Coincident(g2,g1)
    c: Horizontal(g2)
    c: DistanceX(g-4,g2) = 0
    c: Symmetric(g2,g1,g0)
FEATURE [Part::Extrusion] Extrude038  label="Extrude foro per fissaggio micro"
  Base = -> Sketch035
  Dir = (0,-1,2e-16)
  DirMode = 2
  FaceMakerClass = Part::FaceMakerBullseye
  FaceMakerMode = 3
  LengthFwd = 3
  LengthRev = 0
  Placement = pos=(0,8.6,0) rot=(0,0,1;0rad)
  Solid = true
  Symmetric = false
FEATURE [Sketcher::SketchObject] Sketch036  label="supporto per alimentatore"
  ArcFitTolerance = 1e-06
  AttachmentSupport = -> [XZ_Plane]
  ExternalGeometry = -> [Sketch,Sketch016,Sketch022]
  FullyConstrained = true
  MakeInternals = false
  MapMode = 5
  Placement = pos=(0,0,0) rot=(1,0,0;1.5708rad)
  sketch-geometry (5):
    g0: LineSegment StartX=-211.843 StartY=-50.0944 StartZ=0 EndX=-211.843 EndY=-80.4316 EndZ=0
    g1: LineSegment StartX=-211.843 StartY=-50.0944 StartZ=0 EndX=-207.775 EndY=-41.3701 EndZ=0
    g2: LineSegment [constr] StartX=-209.443 StartY=-50.0944 StartZ=0 EndX=-209.443 EndY=-80.4316 EndZ=0
    g3: LineSegment StartX=-207.775 StartY=-41.3701 StartZ=0 EndX=-207.775 EndY=-80.4316 EndZ=0
    g4: LineSegment StartX=-211.843 StartY=-80.4316 StartZ=0 EndX=-207.775 EndY=-80.4316 EndZ=0
  constraints (15):
    c: Vertical(g0)
    c: Coincident(g1,g0)
    c: Vertical(g2)
    c: Tangent(g2,g-5)
    c: Coincident(g3,g1)
    c: Vertical(g3)
    c: DistanceY(g-3,g3) = -2
    c: Tangent(g1,g-8)
    c: DistanceY(g-3,g0) = -2
    c: Coincident(g4,g0)
    c: Coincident(g4,g3)
    c: Tangent(g0,g-6)
    c: DistanceY(g-3,g2) = -2
    c: DistanceY(g2,g0) = 0
    c: DistanceX(g-3,g3) = 6.8
FEATURE [Part::Extrusion] Extrude039  label="Extrude039 supporto alimentatore"
  Base = -> Sketch036
  Dir = (0,-1,2e-16)
  DirMode = 2
  FaceMakerClass = Part::FaceMakerBullseye
  FaceMakerMode = 3
  LengthFwd = 25.2
  LengthRev = 0
  Solid = true
  Symmetric = true
FEATURE [Sketcher::SketchObject] Sketch037  label="scavo per alimentatore"
  ArcFitTolerance = 1e-06
  AttachmentSupport = -> [XZ_Plane]
  ExternalGeometry = -> [Sketch036]
  FullyConstrained = true
  MakeInternals = false
  MapMode = 5
  Placement = pos=(0,0,0) rot=(1,0,0;1.5708rad)
  sketch-geometry (4):
    g0: LineSegment StartX=-209.575 StartY=-50.4316 StartZ=0 EndX=-209.575 EndY=-80.4316 EndZ=0
    g1: LineSegment StartX=-209.575 StartY=-50.4316 StartZ=0 EndX=-207.775 EndY=-50.4316 EndZ=0
    g2: LineSegment StartX=-207.775 StartY=-50.4316 StartZ=0 EndX=-207.775 EndY=-80.4316 EndZ=0
    g3: LineSegment StartX=-207.775 StartY=-80.4316 StartZ=0 EndX=-209.575 EndY=-80.4316 EndZ=0
  constraints (11):
    c: Vertical(g0)
    c: Coincident(g1,g0)
    c: Horizontal(g1)
    c: Coincident(g2,g1)
    c: Vertical(g2)
    c: Coincident(g3,g2)
    c: Coincident(g3,g0)
    c: Horizontal(g3)
    c: DistanceX(g1,g1) = 1.8
    c: Coincident(g2,g-3)
    c: DistanceY(g2,g2) = 30
FEATURE [Part::Extrusion] Extrude040  label="Extrude040 scavo alimentatore"
  Base = -> Sketch037
  Dir = (0,-1,2e-16)
  DirMode = 2
  FaceMakerClass = Part::FaceMakerBullseye
  FaceMakerMode = 3
  LengthFwd = 19.5
  LengthRev = 0
  Solid = true
  Symmetric = true
FEATURE [Part::Extrusion] Extrude031  label="Extrude fermo per scheda micro"
  Base = -> Sketch033
  Dir = (0,-1,2e-16)
  DirMode = 2
  FaceMakerClass = Part::FaceMakerBullseye
  FaceMakerMode = 3
  LengthFwd = 3
  LengthRev = 0
  Placement = pos=(0,8.6,0) rot=(0,0,1;0rad)
  Solid = true
  Symmetric = false
FEATURE [Sketcher::SketchObject] Sketch038  label="scavo driver solenoide"
  ArcFitTolerance = 1e-06
  AttachmentSupport = -> [XZ_Plane]
  ExternalGeometry = -> [Sketch,Sketch036]
  FullyConstrained = true
  MakeInternals = false
  MapMode = 5
  Placement = pos=(0,0,0) rot=(1,0,0;1.5708rad)
  sketch-geometry (7):
    g0: LineSegment StartX=-192.222 StartY=-8.0175 StartZ=0 EndX=-194.941 EndY=-6.74965 EndZ=0
    g1: LineSegment StartX=-194.941 StartY=-6.74965 StartZ=0 EndX=-212.269 EndY=-43.9083 EndZ=0
    g2: LineSegment StartX=-192.222 StartY=-8.0175 StartZ=0 EndX=-188.779 EndY=-9.62345 EndZ=0
    g3: LineSegment StartX=-188.779 StartY=-9.62345 StartZ=0 EndX=-205.357 EndY=-45.1761 EndZ=0
    g4: LineSegment StartX=-205.357 StartY=-45.1761 StartZ=0 EndX=-209.55 EndY=-45.1761 EndZ=0
    g5: LineSegment [constr] StartX=-212.269 StartY=-43.9083 StartZ=0 EndX=-209.55 EndY=-45.1761 EndZ=0
    g6: LineSegment StartX=-212.269 StartY=-43.9083 StartZ=0 EndX=-209.55 EndY=-45.1761 EndZ=0
  constraints (20):
    c: Coincident(g1,g0)
    c: Coincident(g3,g2)
    c: Coincident(g4,g3)
    c: Distance(g2) = 3.8
    c: Distance(g1) = 41
    c: Coincident(g5,g1)
    c: Distance(g5) = 3
    c: Perpendicular(g5,g-3)
    c: Parallel(g1,g-3)
    c: Perpendicular(g1,g0)
    c: Distance(g0) = 3
    c: Coincident(g6,g1)
    c: Parallel(g3,g-3)
    c: Perpendicular(g2,g3)
    c: Coincident(g2,g0)
    c: Perpendicular(g-4,g4)
    c: PointOnObject(g5,g-3)
    c: Distance(g-3,g5) = 9.6
    c: Coincident(g4,g5)
    c: Coincident(g6,g4)
FEATURE [Part::Extrusion] Extrude041  label="Extrude scavo driver solenoide"
  Base = -> Sketch038
  Dir = (0,-1,2e-16)
  DirMode = 2
  FaceMakerClass = Part::FaceMakerBullseye
  FaceMakerMode = 3
  LengthFwd = 20.6
  LengthRev = 0
  Solid = true
  Symmetric = true
FEATURE [Sketcher::SketchObject] Sketch039  label="scavo per cavo usb per micro"
  ArcFitTolerance = 1e-06
  AttachmentSupport = -> [XZ_Plane]
  ExternalGeometry = -> [Sketch,Sketch016]
  FullyConstrained = true
  MakeInternals = false
  MapMode = 5
  Placement = pos=(0,0,0) rot=(1,0,0;1.5708rad)
  sketch-geometry (4):
    g0: LineSegment StartX=-82.51 StartY=36.4 StartZ=0 EndX=-74.51 EndY=36.4 EndZ=0
    g1: LineSegment StartX=-74.51 StartY=36.4 StartZ=0 EndX=-74.51 EndY=30.8 EndZ=0
    g2: LineSegment StartX=-74.51 StartY=30.8 StartZ=0 EndX=-82.51 EndY=30.8 EndZ=0
    g3: LineSegment StartX=-82.51 StartY=30.8 StartZ=0 EndX=-82.51 EndY=36.4 EndZ=0
  constraints (11):
    c: Coincident(g1,g0)
    c: Vertical(g1)
    c: Coincident(g2,g1)
    c: Horizontal(g2)
    c: Coincident(g3,g2)
    c: Coincident(g3,g0)
    c: Vertical(g3)
    c: Tangent(g0,g-3)
    c: Tangent(g2,g-4)
    c: Tangent(g3,g-4)
    c: Tangent(g1,g-4)
FEATURE [Part::Extrusion] Extrude042  label="Extrude scavo per cavo usb per micro"
  Base = -> Sketch039
  Dir = (0,-1,2e-16)
  DirMode = 2
  FaceMakerClass = Part::FaceMakerBullseye
  FaceMakerMode = 3
  LengthFwd = 11.2
  LengthRev = 0
  Solid = true
  Symmetric = true
FEATURE [Sketcher::SketchObject] Sketch040  label="scavo saldature alimentatore connettore 5v"
  ArcFitTolerance = 1e-06
  AttachmentSupport = -> [XZ_Plane]
  ExternalGeometry = -> [Sketch037]
  FullyConstrained = true
  MakeInternals = false
  MapMode = 5
  Placement = pos=(0,0,0) rot=(1,0,0;1.5708rad)
  sketch-geometry (4):
    g0: LineSegment StartX=-211.175 StartY=-52.4316 StartZ=0 EndX=-211.175 EndY=-56.4316 EndZ=0
    g1: LineSegment StartX=-211.175 StartY=-52.4316 StartZ=0 EndX=-209.575 EndY=-52.4316 EndZ=0
    g2: LineSegment StartX=-209.575 StartY=-52.4316 StartZ=0 EndX=-209.575 EndY=-56.4316 EndZ=0
    g3: LineSegment StartX=-209.575 StartY=-56.4316 StartZ=0 EndX=-211.175 EndY=-56.4316 EndZ=0
  constraints (11):
    c: Vertical(g0)
    c: Coincident(g1,g0)
    c: Horizontal(g1)
    c: Coincident(g2,g1)
    c: Coincident(g3,g2)
    c: Coincident(g3,g0)
    c: Horizontal(g3)
    c: DistanceX(g1,g1) = 1.6
    c: DistanceY(g2,g2) = 4
    c: Tangent(g2,g-3)
    c: DistanceY(g1,g-3) = 2
FEATURE [Part::Extrusion] Extrude043  label="Extrude scavo saldature alimentatore connettore 5v"
  Base = -> Sketch040
  Dir = (0,-1,2e-16)
  DirMode = 2
  FaceMakerClass = Part::FaceMakerBullseye
  FaceMakerMode = 3
  LengthFwd = 8
  LengthRev = 0
  Solid = true
  Symmetric = true
FEATURE [Sketcher::SketchObject] Sketch041  label="scavo saldature alimentatore connettore 5v verticali"
  ArcFitTolerance = 1e-06
  AttachmentSupport = -> [XZ_Plane]
  ExternalGeometry = -> [Sketch037]
  FullyConstrained = true
  MakeInternals = false
  MapMode = 5
  Placement = pos=(0,0,0) rot=(1,0,0;1.5708rad)
  sketch-geometry (4):
    g0: LineSegment StartX=-211.175 StartY=-53.6316 StartZ=0 EndX=-209.575 EndY=-53.6316 EndZ=0
    g1: LineSegment StartX=-209.575 StartY=-53.6316 StartZ=0 EndX=-209.575 EndY=-76.6316 EndZ=0
    g2: LineSegment StartX=-209.575 StartY=-76.6316 StartZ=0 EndX=-211.175 EndY=-76.6316 EndZ=0
    g3: LineSegment StartX=-211.175 StartY=-76.6316 StartZ=0 EndX=-211.175 EndY=-53.6316 EndZ=0
  constraints (11):
    c: Horizontal(g0)
    c: Coincident(g1,g0)
    c: Coincident(g2,g1)
    c: Horizontal(g2)
    c: Coincident(g3,g2)
    c: Coincident(g3,g0)
    c: Vertical(g3)
    c: DistanceY(g3,g3) = 23
    c: DistanceX(g0,g0) = 1.6
    c: Tangent(g1,g-3)
    c: DistanceY(g0,g-3) = 3.2
FEATURE [Part::Extrusion] Extrude044  label="Extrude scavo saldature alimentatore connettore 5v verticali"
  Base = -> Sketch041
  Dir = (0,-1,2e-16)
  DirMode = 2
  FaceMakerClass = Part::FaceMakerBullseye
  FaceMakerMode = 3
  LengthFwd = 3.2
  LengthRev = 0
  Placement = pos=(0,8.3,0) rot=(0,0,1;0rad)
  Solid = true
  Symmetric = false
FEATURE [Sketcher::SketchObject] Sketch042  label="fermi per driver solenoide e alimentatore"
  ArcFitTolerance = 1e-06
  AttachmentSupport = -> [XZ_Plane]
  ExternalGeometry = -> [Sketch036,Sketch037,Sketch,Sketch038]
  FullyConstrained = true
  MakeInternals = false
  MapMode = 5
  Placement = pos=(0,0,0) rot=(1,0,0;1.5708rad)
  sketch-geometry (27):
    g0: LineSegment StartX=-200.506 StartY=-25.7811 StartZ=0 EndX=-201.436 EndY=-27.775 EndZ=0
    g1: LineSegment StartX=-201.436 StartY=-27.775 StartZ=0 EndX=-199.442 EndY=-28.7048 EndZ=0
    g2: LineSegment StartX=-199.442 StartY=-28.7048 StartZ=0 EndX=-198.512 EndY=-26.7109 EndZ=0
    g3: LineSegment StartX=-198.512 StartY=-26.7109 StartZ=0 EndX=-200.506 EndY=-25.7811 EndZ=0
    g4: LineSegment StartX=-201.28 StartY=-23.6549 StartZ=0 EndX=-203.562 EndY=-28.5489 EndZ=0
    g5: LineSegment StartX=-203.562 StartY=-28.5489 StartZ=0 EndX=-200.118 EndY=-30.1549 EndZ=0
    g6: LineSegment StartX=-197.992 StartY=-29.381 StartZ=0 EndX=-197.062 EndY=-27.3871 EndZ=0
    g7: LineSegment StartX=-197.836 StartY=-25.2608 StartZ=0 EndX=-201.28 EndY=-23.6549 EndZ=0
    g8: LineSegment [constr] StartX=-198.668 StartY=-30.8311 StartZ=0 EndX=-197.992 EndY=-29.381 EndZ=0
    g9: LineSegment [constr] StartX=-198.668 StartY=-30.8311 StartZ=0 EndX=-200.118 EndY=-30.1549 EndZ=0
    g10: ArcOfCircle CenterX=-198.512 CenterY=-26.7109 CenterZ=0 NormalX=0 NormalY=0 NormalZ=1 AngleXU=0 Radius=1.6 StartAngle=5.84685 EndAngle=7.41765
    g11: GeomPoint [constr] X=-196.386 Y=-25.937 Z=0
    g12: ArcOfCircle CenterX=-199.442 CenterY=-28.7048 CenterZ=0 NormalX=0 NormalY=0 NormalZ=1 AngleXU=0 Radius=1.6 StartAngle=4.27606 EndAngle=5.84685
    g13: GeomPoint [constr] X=-198.668 Y=-30.8311 Z=0
    g14: LineSegment StartX=-207.775 StartY=-46.8316 StartZ=0 EndX=-207.775 EndY=-50.8316 EndZ=0
    g15: LineSegment StartX=-207.775 StartY=-46.8316 StartZ=0 EndX=-203.775 EndY=-46.8316 EndZ=0
    g16: LineSegment StartX=-203.775 StartY=-46.8316 StartZ=0 EndX=-203.775 EndY=-50.8316 EndZ=0
    g17: LineSegment StartX=-207.775 StartY=-50.8316 StartZ=0 EndX=-203.775 EndY=-50.8316 EndZ=0
    g18: LineSegment StartX=-209.375 StartY=-52.4316 StartZ=0 EndX=-203.775 EndY=-52.4316 EndZ=0
    g19: LineSegment StartX=-202.175 StartY=-50.8316 StartZ=0 EndX=-202.175 EndY=-46.8316 EndZ=0
    g20: LineSegment StartX=-203.775 StartY=-45.2316 StartZ=0 EndX=-209.375 EndY=-45.2316 EndZ=0
    g21: LineSegment StartX=-209.375 StartY=-45.2316 StartZ=0 EndX=-209.375 EndY=-52.4316 EndZ=0
    g22: ArcOfCircle CenterX=-203.775 CenterY=-46.8316 CenterZ=0 NormalX=0 NormalY=0 NormalZ=1 AngleXU=0 Radius=1.6 StartAngle=1.8e-15 EndAngle=1.5708
    g23: GeomPoint [constr] X=-202.175 Y=-45.2316 Z=0
    g24: ArcOfCircle CenterX=-203.775 CenterY=-50.8316 CenterZ=0 NormalX=0 NormalY=0 NormalZ=1 AngleXU=0 Radius=1.6 StartAngle=4.71239 EndAngle=6.28319
    g25: GeomPoint [constr] X=-202.175 Y=-52.4316 Z=0
    g26: LineSegment [constr] StartX=-207.775 StartY=-50.4316 StartZ=0 EndX=-207.775 EndY=-50.8316 EndZ=0
  constraints (69):
    c: Coincident(g1,g0)
    c: Coincident(g2,g1)
    c: Coincident(g3,g2)
    c: Coincident(g3,g0)
    c: Parallel(g0,g2)
    c: Perpendicular(g3,g0)
    c: Perpendicular(g1,g0)
    c: Coincident(g5,g4)
    c: Coincident(g7,g4)
    c: Distance(g3) = 2.2
    c: Distance(g2) = 2.2
    c: Parallel(g6,g2)
    c: Parallel(g6,g4)
    c: Perpendicular(g5,g6)
    c: Perpendicular(g7,g6)
    c: Distance(g13,g11) = 5.4
    c: Distance(g5,g13) = 5.4
    c: Coincident(g9,g8)
    c: Distance(g8) = 1.6
    c: Distance(g9) = 1.6
    c: Perpendicular(g9,g8)
    c: Parallel(g8,g6)
    c: Coincident(g8,g13)
    c: Distance(g8,g1) = 1.6
    c: Distance(g9,g1) = 1.6
    c: Tangent(g0,g-5)
    c: Distance(g0,g-6) = 19.2
    c: PointOnObject(g11,g7)
    c: PointOnObject(g11,g6)
    c: Tangent(g7,g10) = -1.5708
    c: Tangent(g6,g10) = -1.5708
    c: PointOnObject(g13,g5)
    c: Tangent(g5,g12) = -1.5708
    c: Tangent(g6,g12) = -1.5708
    c: Equal(g10,g12)
    c: Coincident(g10,g2)
    c: Vertical(g14)
    c: Coincident(g15,g14)
    c: Horizontal(g15)
    c: Coincident(g16,g15)
    c: Vertical(g16)
    c: Coincident(g17,g14)
    c: Coincident(g17,g16)
    c: Horizontal(g17)
    c: Distance(g16) = 4
    c: Distance(g15) = 4
    c: Horizontal(g18)
    c: Vertical(g19)
    c: Horizontal(g20)
    c: Coincident(g21,g20)
    c: Coincident(g21,g18)
    c: Vertical(g21)
    c: Distance(g20,g23) = 7.2
    c: Distance(g25,g23) = 7.2
    c: DistanceY(g18,g14) = 1.6
    c: DistanceX(g18,g14) = 1.6
    c: PointOnObject(g23,g20)
    c: PointOnObject(g23,g19)
    c: Tangent(g20,g22) = -1.5708
    c: Tangent(g19,g22) = -1.5708
    c: PointOnObject(g25,g19)
    c: Tangent(g18,g24) = -1.5708
    c: Tangent(g19,g24) = -1.5708
    c: Equal(g22,g24)
    c: Coincident(g22,g15)
    c: Vertical(g26)
    c: Distance(g26) = 0.4
    c: Coincident(g26,g-4)
    c: Coincident(g14,g26)
FEATURE [Part::Extrusion] Extrude045  label="Extrude fermi per driver solenoide e alimentatore"
  Base = -> Sketch042
  Dir = (0,-1,2e-16)
  DirMode = 2
  FaceMakerClass = Part::FaceMakerBullseye
  FaceMakerMode = 3
  LengthFwd = 25.2
  LengthRev = 0
  Solid = true
  Symmetric = true
FEATURE [Sketcher::SketchObject] Sketch043  label="scavo pulizia fermo alimentatore"
  ArcFitTolerance = 1e-06
  AttachmentSupport = -> [XZ_Plane]
  ExternalGeometry = -> [Sketch042,Sketch036,Sketch037]
  FullyConstrained = true
  MakeInternals = false
  MapMode = 5
  Placement = pos=(0,0,0) rot=(1,0,0;1.5708rad)
  sketch-geometry (6):
    g0: LineSegment StartX=-209.375 StartY=-52.4316 StartZ=0 EndX=-209.375 EndY=-50.4316 EndZ=0
    g1: LineSegment StartX=-209.375 StartY=-50.4316 StartZ=0 EndX=-207.775 EndY=-50.4316 EndZ=0
    g2: LineSegment StartX=-207.775 StartY=-50.4316 StartZ=0 EndX=-207.775 EndY=-45.2316 EndZ=0
    g3: LineSegment StartX=-207.775 StartY=-45.2316 StartZ=0 EndX=-202.175 EndY=-45.2316 EndZ=0
    g4: LineSegment StartX=-202.175 StartY=-45.2316 StartZ=0 EndX=-202.175 EndY=-52.4316 EndZ=0
    g5: LineSegment StartX=-202.175 StartY=-52.4316 StartZ=0 EndX=-209.375 EndY=-52.4316 EndZ=0
  constraints (13):
    c: Vertical(g0)
    c: Coincident(g1,g0)
    c: Coincident(g2,g1)
    c: Coincident(g3,g2)
    c: Coincident(g4,g3)
    c: Coincident(g5,g4)
    c: Coincident(g5,g0)
    c: Horizontal(g5)
    c: Coincident(g0,g-6)
    c: Tangent(g1,g-8)
    c: Tangent(g2,g-4)
    c: Tangent(g3,g-7)
    c: Tangent(g4,g-3)
FEATURE [Part::Extrusion] Extrude046  label="Extrude scavo pulizia fermo alimentatore"
  Base = -> Sketch043
  Dir = (0,-1,2e-16)
  DirMode = 2
  FaceMakerClass = Part::FaceMakerBullseye
  FaceMakerMode = 3
  LengthFwd = 19.5
  LengthRev = 0
  Solid = true
  Symmetric = true
FEATURE [Sketcher::SketchObject] Sketch044  label="buchini per fissaggio oled"
  ArcFitTolerance = 1e-06
  AttachmentSupport = -> [YZ_Plane]
  ExternalGeometry = -> [Sketch]
  FullyConstrained = true
  MakeInternals = false
  MapMode = 5
  Placement = pos=(0,0,0) rot=(0.57735,0.57735,0.57735;2.0944rad)
  sketch-geometry (5):
    g0: LineSegment [constr] StartX=1.5e-14 StartY=67.3588 StartZ=0 EndX=0 EndY=64.3588 EndZ=0
    g1: LineSegment [constr] StartX=0 StartY=64.3588 StartZ=0 EndX=10.4 EndY=64.3588 EndZ=0
    g2: LineSegment [constr] StartX=0 StartY=64.3588 StartZ=0 EndX=-10.4 EndY=64.3588 EndZ=0
    g3: Circle CenterX=10.4 CenterY=64.3588 CenterZ=0 NormalX=0 NormalY=0 NormalZ=1 AngleXU=0 Radius=1.5
    g4: Circle CenterX=-10.4 CenterY=64.3588 CenterZ=0 NormalX=0 NormalY=0 NormalZ=1 AngleXU=0 Radius=1.5
  constraints (13):
    c: Distance(g0) = 3
    c: PointOnObject(g0,g-2)
    c: Coincident(g1,g0)
    c: Horizontal(g1)
    c: Coincident(g2,g0)
    c: Horizontal(g2)
    c: DistanceX(g1,g1) = 10.4
    c: Coincident(g3,g1)
    c: Diameter(g4) = 3
    c: Coincident(g4,g2)
    c: Coincident(g0,g-7)
    c: Equal(g1,g2)
    c: Equal(g4,g3)
FEATURE [Part::Extrusion] Extrude047  label="Extrude buchini per fissaggio oled"
  Base = -> Sketch044
  Dir = (1,0,0)
  DirMode = 2
  FaceMakerClass = Part::FaceMakerBullseye
  FaceMakerMode = 3
  LengthFwd = 10
  LengthRev = 0
  Placement = pos=(-186,0,0) rot=(0,0,1;0rad)
  Solid = true
  Symmetric = false
FEATURE [Sketcher::SketchObject] Sketch046  label="scavo 5x5 neopixel"
  ArcFitTolerance = 1e-06
  AttachmentSupport = -> [YZ_Plane002]
  FullyConstrained = true
  MakeInternals = false
  MapMode = 5
  Placement = pos=(0,0,0) rot=(0.57735,0.57735,0.57735;2.0944rad)
  sketch-geometry (4):
    g0: LineSegment StartX=-2.7 StartY=2.7 StartZ=0 EndX=2.7 EndY=2.7 EndZ=0
    g1: LineSegment StartX=2.7 StartY=2.7 StartZ=0 EndX=2.7 EndY=-2.7 EndZ=0
    g2: LineSegment StartX=2.7 StartY=-2.7 StartZ=0 EndX=-2.7 EndY=-2.7 EndZ=0
    g3: LineSegment StartX=-2.7 StartY=-2.7 StartZ=0 EndX=-2.7 EndY=2.7 EndZ=0
  constraints (11):
    c: Horizontal(g0)
    c: Coincident(g1,g0)
    c: Vertical(g1)
    c: Coincident(g2,g1)
    c: Horizontal(g2)
    c: Coincident(g3,g2)
    c: Coincident(g3,g0)
    c: Vertical(g3)
    c: DistanceX(g0,g0) = 5.4
    c: DistanceY(g1,g1) = 5.4
    c: Symmetric(g0,g1,g-1)
FEATURE [Sketcher::SketchObject] Sketch047  label="scavo 10x10 neopixel corpo"
  ArcFitTolerance = 1e-06
  AttachmentOffset = pos=(0,0,1) rot=(0,0,1;0rad)
  AttachmentSupport = -> [YZ_Plane002]
  FullyConstrained = true
  MakeInternals = false
  MapMode = 5
  Placement = pos=(1,0,0) rot=(0.57735,0.57735,0.57735;2.0944rad)
  sketch-geometry (4):
    g0: LineSegment StartX=-5 StartY=5.1 StartZ=0 EndX=5 EndY=5.1 EndZ=0
    g1: LineSegment StartX=5 StartY=5.1 StartZ=0 EndX=5 EndY=-5.1 EndZ=0
    g2: LineSegment StartX=5 StartY=-5.1 StartZ=0 EndX=-5 EndY=-5.1 EndZ=0
    g3: LineSegment StartX=-5 StartY=-5.1 StartZ=0 EndX=-5 EndY=5.1 EndZ=0
  constraints (11):
    c: Horizontal(g0)
    c: Coincident(g1,g0)
    c: Vertical(g1)
    c: Coincident(g2,g1)
    c: Horizontal(g2)
    c: Coincident(g3,g2)
    c: Coincident(g3,g0)
    c: Vertical(g3)
    c: DistanceX(g0,g0) = 10
    c: DistanceY(g1,g1) = 10.2
    c: Symmetric(g0,g2,g-1)
FEATURE [Sketcher::SketchObject] Sketch048  label="buco per perno blocco neopixel"
  ArcFitTolerance = 1e-06
  AttachmentSupport = -> [XZ_Plane002]
  FullyConstrained = true
  MakeInternals = false
  MapMode = 5
  Placement = pos=(0,0,0) rot=(1,0,0;1.5708rad)
  sketch-geometry (4):
    g0: LineSegment StartX=3 StartY=1.2 StartZ=0 EndX=3 EndY=-1.2 EndZ=0
    g1: LineSegment StartX=3 StartY=-1.2 StartZ=0 EndX=5.4 EndY=-1.2 EndZ=0
    g2: LineSegment StartX=5.4 StartY=-1.2 StartZ=0 EndX=5.4 EndY=1.2 EndZ=0
    g3: LineSegment StartX=5.4 StartY=1.2 StartZ=0 EndX=3 EndY=1.2 EndZ=0
  constraints (11):
    c: Coincident(g1,g0)
    c: Horizontal(g1)
    c: Coincident(g2,g1)
    c: Vertical(g2)
    c: Coincident(g3,g2)
    c: Coincident(g3,g0)
    c: Horizontal(g3)
    c: DistanceX(g1,g1) = 2.4
    c: DistanceY(g2,g2) = 2.4
    c: Symmetric(g0,g0,g-1)
    c: DistanceX(g-1,g0) = 3
FEATURE [Sketcher::SketchObject] Sketch045  label="blocco principale per neopixel"
  ArcFitTolerance = 1e-06
  AttachmentSupport = -> [XZ_Plane002]
  ExternalGeometry = -> [Sketch048]
  FullyConstrained = true
  MakeInternals = false
  MapMode = 5
  Placement = pos=(0,0,0) rot=(1,0,0;1.5708rad)
  sketch-geometry (6):
    g0: LineSegment StartX=0 StartY=5.1 StartZ=0 EndX=0 EndY=-5.1 EndZ=0
    g1: LineSegment StartX=0 StartY=-5.1 StartZ=0 EndX=3 EndY=-5.1 EndZ=0
    g2: LineSegment StartX=7 StartY=-1.1 StartZ=0 EndX=7 EndY=5.1 EndZ=0
    g3: LineSegment StartX=7 StartY=5.1 StartZ=0 EndX=0 EndY=5.1 EndZ=0
    g4: ArcOfCircle CenterX=3 CenterY=-1.1 CenterZ=0 NormalX=0 NormalY=0 NormalZ=1 AngleXU=0 Radius=4 StartAngle=4.71239 EndAngle=6.28319
    g5: GeomPoint [constr] X=7 Y=-5.1 Z=0
  constraints (15):
    c: Vertical(g0)
    c: Coincident(g1,g0)
    c: Horizontal(g1)
    c: Vertical(g2)
    c: Coincident(g3,g2)
    c: Coincident(g3,g0)
    c: Horizontal(g3)
    c: DistanceY(g0,g0) = 10.2
    c: Symmetric(g0,g0,g-1)
    c: DistanceX(g3,g3) = 7
    c: PointOnObject(g5,g2)
    c: PointOnObject(g5,g1)
    c: Tangent(g2,g4) = -1.5708
    c: Tangent(g1,g4) = -1.5708
    c: DistanceX(g-3,g1) = 0
FEATURE [Sketcher::SketchObject] Sketch049  label="rinforzi esterni per corpo neopoixel"
  ArcFitTolerance = 1e-06
  AttachmentSupport = -> [XZ_Plane002]
  ExternalGeometry = -> [Sketch045]
  FullyConstrained = true
  MakeInternals = false
  MapMode = 5
  Placement = pos=(0,0,0) rot=(1,0,0;1.5708rad)
  sketch-geometry (8):
    g0: LineSegment StartX=1 StartY=-4.1 StartZ=0 EndX=2 EndY=-4.1 EndZ=0
    g1: LineSegment StartX=2 StartY=-4.1 StartZ=0 EndX=2 EndY=-5.1 EndZ=0
    g2: LineSegment StartX=2 StartY=-5.1 StartZ=0 EndX=1 EndY=-5.1 EndZ=0
    g3: LineSegment StartX=1 StartY=-5.1 StartZ=0 EndX=1 EndY=-4.1 EndZ=0
    g4: LineSegment StartX=1 StartY=5.1 StartZ=0 EndX=2 EndY=5.1 EndZ=0
    g5: LineSegment StartX=2 StartY=5.1 StartZ=0 EndX=2 EndY=4.1 EndZ=0
    g6: LineSegment StartX=2 StartY=4.1 StartZ=0 EndX=1 EndY=4.1 EndZ=0
    g7: LineSegment StartX=1 StartY=4.1 StartZ=0 EndX=1 EndY=5.1 EndZ=0
  constraints (24):
    c: Horizontal(g0)
    c: Coincident(g1,g0)
    c: Vertical(g1)
    c: Coincident(g2,g1)
    c: Horizontal(g2)
    c: Coincident(g3,g2)
    c: Coincident(g3,g0)
    c: Vertical(g3)
    c: Horizontal(g4)
    c: Coincident(g5,g4)
    c: Vertical(g5)
    c: Coincident(g6,g5)
    c: Horizontal(g6)
    c: Coincident(g7,g6)
    c: Coincident(g7,g4)
    c: Vertical(g7)
    c: DistanceX(g4,g4) = 1
    c: DistanceY(g5,g5) = 1
    c: DistanceX(g0,g0) = 1
    c: DistanceY(g1,g1) = 1
    c: DistanceX(g-3,g4) = 1
    c: DistanceY(g-3,g4) = 0
    c: DistanceX(g-4,g2) = 1
    c: DistanceY(g2,g-4) = 0
FEATURE [Sketcher::SketchObject] Sketch052  label="scavo saldature driver solenoide"
  ArcFitTolerance = 1e-06
  AttachmentSupport = -> [XZ_Plane]
  ExternalGeometry = -> [Sketch038]
  FullyConstrained = true
  MakeInternals = false
  MapMode = 5
  Placement = pos=(0,0,0) rot=(1,0,0;1.5708rad)
  sketch-geometry (4):
    g0: LineSegment StartX=-195.304 StartY=-6.5806 StartZ=0 EndX=-196.994 EndY=-10.2058 EndZ=0
    g1: LineSegment StartX=-196.994 StartY=-10.2058 StartZ=0 EndX=-196.632 EndY=-10.3749 EndZ=0
    g2: LineSegment StartX=-196.632 StartY=-10.3749 StartZ=0 EndX=-194.941 EndY=-6.74965 EndZ=0
    g3: LineSegment StartX=-194.941 StartY=-6.74965 StartZ=0 EndX=-195.304 EndY=-6.5806 EndZ=0
  constraints (11):
    c: Coincident(g1,g0)
    c: Coincident(g2,g1)
    c: Coincident(g3,g2)
    c: Coincident(g3,g0)
    c: Parallel(g2,g0)
    c: Perpendicular(g2,g3)
    c: Perpendicular(g1,g2,g1) = 1.5708
    c: Parallel(g2,g-3)
    c: Distance(g2) = 4
    c: Distance(g3) = 0.4
    c: Coincident(g2,g-3)
FEATURE [Part::Extrusion] Extrude055  label="Extrude scavo saldature driver solenoide"
  Base = -> Sketch052
  Dir = (0,-1,2e-16)
  DirMode = 2
  FaceMakerClass = Part::FaceMakerBullseye
  FaceMakerMode = 3
  LengthFwd = 6
  LengthRev = 0
  Solid = true
  Symmetric = true
FEATURE [Sketcher::SketchObject] Sketch053  label="scavo saldature rumble"
  ArcFitTolerance = 1e-06
  AttachmentSupport = -> [XZ_Plane]
  ExternalGeometry = -> [Sketch019]
  FullyConstrained = true
  MakeInternals = false
  MapMode = 5
  Placement = pos=(0,0,0) rot=(1,0,0;1.5708rad)
  sketch-geometry (4):
    g0: LineSegment StartX=-164.507 StartY=-41.6446 StartZ=0 EndX=-165.743 EndY=-45.4488 EndZ=0
    g1: LineSegment StartX=-165.743 StartY=-45.4488 StartZ=0 EndX=-164.602 EndY=-45.8196 EndZ=0
    g2: LineSegment StartX=-164.602 StartY=-45.8196 StartZ=0 EndX=-163.366 EndY=-42.0154 EndZ=0
    g3: LineSegment StartX=-163.366 StartY=-42.0154 StartZ=0 EndX=-164.507 EndY=-41.6446 EndZ=0
  constraints (11):
    c: Coincident(g1,g0)
    c: Coincident(g2,g1)
    c: Coincident(g3,g2)
    c: Coincident(g3,g0)
    c: Parallel(g0,g2)
    c: Perpendicular(g3,g0)
    c: Perpendicular(g1,g0)
    c: Parallel(g0,g-3)
    c: Distance(g0) = 4
    c: Distance(g1) = 1.2
    c: Coincident(g0,g-3)
FEATURE [Part::Extrusion] Extrude056  label="Extrude scavo saldature rumble"
  Base = -> Sketch053
  Dir = (0,-1,2e-16)
  DirMode = 2
  FaceMakerClass = Part::FaceMakerBullseye
  FaceMakerMode = 3
  LengthFwd = 8.4
  LengthRev = 0
  Solid = true
  Symmetric = true
FEATURE [Sketcher::SketchObject] Sketch054  label="scavo saldature alimentatore connettore USB"
  ArcFitTolerance = 1e-06
  AttachmentSupport = -> [XZ_Plane]
  ExternalGeometry = -> [Sketch037]
  FullyConstrained = true
  MakeInternals = false
  MapMode = 5
  Placement = pos=(0,0,0) rot=(1,0,0;1.5708rad)
  sketch-geometry (4):
    g0: LineSegment StartX=-209.575 StartY=-80.4316 StartZ=0 EndX=-210.375 EndY=-80.4316 EndZ=0
    g1: LineSegment StartX=-210.375 StartY=-80.4316 StartZ=0 EndX=-210.375 EndY=-72.4316 EndZ=0
    g2: LineSegment StartX=-210.375 StartY=-72.4316 StartZ=0 EndX=-209.575 EndY=-72.4316 EndZ=0
    g3: LineSegment StartX=-209.575 StartY=-72.4316 StartZ=0 EndX=-209.575 EndY=-80.4316 EndZ=0
  constraints (11):
    c: Horizontal(g0)
    c: Coincident(g1,g0)
    c: Vertical(g1)
    c: Coincident(g2,g1)
    c: Horizontal(g2)
    c: Coincident(g3,g2)
    c: Coincident(g3,g0)
    c: Vertical(g3)
    c: DistanceX(g0,g0) = 0.8
    c: DistanceY(g3,g3) = 8
    c: Coincident(g0,g-4)
FEATURE [Part::Extrusion] Extrude057  label="Extrude scavo saldature alimentatore connettore USB"
  Base = -> Sketch054
  Dir = (0,-1,2e-16)
  DirMode = 2
  FaceMakerClass = Part::FaceMakerBullseye
  FaceMakerMode = 3
  LengthFwd = 11
  LengthRev = 0
  Solid = true
  Symmetric = true
FEATURE [Sketcher::SketchObject] Sketch055  label="buco interno per micro switch"
  ArcFitTolerance = 1e-06
  AttachmentSupport = -> [XZ_Plane]
  ExternalGeometry = -> [Sketch]
  FullyConstrained = true
  MakeInternals = false
  MapMode = 5
  Placement = pos=(0,0,0) rot=(1,0,0;1.5708rad)
  sketch-geometry (11):
    g0: LineSegment [constr] StartX=-194.483 StartY=34.2854 StartZ=0 EndX=-196.022 EndY=30.0568 EndZ=0
    g1: LineSegment [constr] StartX=-196.022 StartY=30.0568 StartZ=0 EndX=-197.561 EndY=25.8282 EndZ=0
    g2: LineSegment [constr] StartX=-196.022 StartY=30.0568 StartZ=0 EndX=-194.143 EndY=29.3727 EndZ=0
    g3: LineSegment [constr] StartX=-196.022 StartY=30.0568 StartZ=0 EndX=-197.902 EndY=30.7408 EndZ=0
    g4: LineSegment StartX=-196.362 StartY=34.9694 StartZ=0 EndX=-192.604 EndY=33.6014 EndZ=0
    g5: LineSegment StartX=-199.441 StartY=26.5122 StartZ=0 EndX=-195.682 EndY=25.1441 EndZ=0
    g6: LineSegment StartX=-192.604 StartY=33.6014 StartZ=0 EndX=-195.682 EndY=25.1441 EndZ=0
    g7: LineSegment StartX=-196.362 StartY=34.9694 StartZ=0 EndX=-199.441 EndY=26.5122 EndZ=0
    g8: GeomPoint [constr] X=-187.821 Y=29.2 Z=0
    g9: LineSegment [constr] StartX=-188.505 StartY=27.3206 StartZ=0 EndX=-196.022 EndY=30.0568 EndZ=0
    g10: LineSegment [constr] StartX=-187.821 StartY=29.2 StartZ=0 EndX=-188.505 EndY=27.3206 EndZ=0
  constraints (27):
    c: Coincident(g2,g0)
    c: Parallel(g0,g-3)
    c: Tangent(g1,g0) = -1.5708
    c: Perpendicular(g0,g2)
    c: Tangent(g2,g3)
    c: Distance(g0,g1) = 9
    c: Equal(g0,g1)
    c: Distance(g3,g2) = 4
    c: Equal(g2,g3)
    c: Parallel(g3,g4)
    c: Symmetric(g4,g4,g0)
    c: Parallel(g6,g1)
    c: Parallel(g7,g1)
    c: Symmetric(g6,g6,g2)
    c: Symmetric(g5,g5,g1)
    c: Symmetric(g7,g7,g3)
    c: Coincident(g7,g4)
    c: Coincident(g6,g4)
    c: Coincident(g5,g6)
    c: Symmetric(g-3,g-3,g8)
    c: Perpendicular(g-3,g9)
    c: Distance(g9) = 8
    c: Coincident(g3,g9)
    c: Coincident(g10,g8)
    c: Parallel(g10,g-3)
    c: Distance(g10) = 2
    c: Coincident(g10,g9)
FEATURE [Sketcher::SketchObject] Sketch056  label="buco esterno per micro switch"
  ArcFitTolerance = 1e-06
  AttachmentSupport = -> [XZ_Plane]
  ExternalGeometry = -> [Sketch055]
  FullyConstrained = true
  MakeInternals = false
  MapMode = 5
  Placement = pos=(0,0,0) rot=(1,0,0;1.5708rad)
  sketch-geometry (17):
    g0: GeomPoint [constr] X=-194.143 Y=29.3727 Z=0
    g1: GeomPoint [constr] X=-194.483 Y=34.2854 Z=0
    g2: GeomPoint [constr] X=-197.902 Y=30.7408 Z=0
    g3: GeomPoint [constr] X=-197.561 Y=25.8282 Z=0
    g4: GeomPoint [constr] X=-196.022 Y=30.0568 Z=0
    g5: LineSegment [constr] StartX=-194.483 StartY=34.2854 StartZ=0 EndX=-196.022 EndY=30.0568 EndZ=0
    g6: LineSegment [constr] StartX=-196.022 StartY=30.0568 StartZ=0 EndX=-197.561 EndY=25.8282 EndZ=0
    g7: LineSegment [constr] StartX=-197.902 StartY=30.7408 StartZ=0 EndX=-196.022 EndY=30.0568 EndZ=0
    g8: LineSegment [constr] StartX=-196.022 StartY=30.0568 StartZ=0 EndX=-194.143 EndY=29.3727 EndZ=0
    g9: LineSegment [constr] StartX=-195.338 StartY=31.9362 StartZ=0 EndX=-196.022 EndY=30.0568 EndZ=0
    g10: LineSegment [constr] StartX=-196.022 StartY=30.0568 StartZ=0 EndX=-196.706 EndY=28.1774 EndZ=0
    g11: LineSegment [constr] StartX=-196.022 StartY=30.0568 StartZ=0 EndX=-196.821 EndY=30.3475 EndZ=0
    g12: LineSegment [constr] StartX=-196.022 StartY=30.0568 StartZ=0 EndX=-195.223 EndY=29.7661 EndZ=0
    g13: LineSegment StartX=-194.539 StartY=31.6454 StartZ=0 EndX=-195.907 EndY=27.8867 EndZ=0
    g14: LineSegment StartX=-196.137 StartY=32.2269 StartZ=0 EndX=-197.505 EndY=28.4681 EndZ=0
    g15: LineSegment StartX=-196.137 StartY=32.2269 StartZ=0 EndX=-194.539 EndY=31.6454 EndZ=0
    g16: LineSegment StartX=-197.505 StartY=28.4681 StartZ=0 EndX=-195.907 EndY=27.8867 EndZ=0
  constraints (34):
    c: Symmetric(g-5,g-5,g1)
    c: Symmetric(g-5,g-6,g0)
    c: Symmetric(g-6,g-6,g3)
    c: Symmetric(g-5,g-6,g2)
    c: Coincident(g5,g1)
    c: Coincident(g5,g4)
    c: Coincident(g6,g4)
    c: Coincident(g6,g3)
    c: Equal(g5,g6)
    c: Coincident(g7,g2)
    c: Coincident(g7,g4)
    c: Coincident(g8,g4)
    c: Coincident(g8,g0)
    c: Equal(g7,g8)
    c: Coincident(g11,g9)
    c: Coincident(g12,g9)
    c: Tangent(g10,g9) = -1.5708
    c: Perpendicular(g11,g9)
    c: Parallel(g9,g-4)
    c: Equal(g9,g10)
    c: Parallel(g12,g11)
    c: Equal(g11,g12)
    c: Distance(g11,g12) = 1.7
    c: Distance(g9,g10) = 4
    c: Symmetric(g13,g13,g12)
    c: Parallel(g13,g9)
    c: Symmetric(g14,g14,g11)
    c: Symmetric(g15,g15,g9)
    c: Parallel(g15,g11)
    c: Symmetric(g16,g16,g10)
    c: Coincident(g16,g14)
    c: Coincident(g15,g14)
    c: Coincident(g13,g15)
    c: Coincident(g9,g4)
FEATURE [Sketcher::SketchObject] Sketch057  label="buco interno per SWITCH"
  ArcFitTolerance = 1e-06
  AttachmentSupport = -> [XZ_Plane]
  ExternalGeometry = -> [Sketch]
  FullyConstrained = true
  MakeInternals = false
  MapMode = 5
  Placement = pos=(0,0,0) rot=(1,0,0;1.5708rad)
  sketch-geometry (10):
    g0: GeomPoint [constr] X=-187.821 Y=29.2 Z=0
    g1: LineSegment [constr] StartX=-188.505 StartY=27.3206 StartZ=0 EndX=-193.203 EndY=29.0307 EndZ=0
    g2: LineSegment [constr] StartX=-190.809 StartY=35.6086 StartZ=0 EndX=-195.597 EndY=22.4529 EndZ=0
    g3: GeomPoint [constr] X=-193.203 Y=29.0307 Z=0
    g4: LineSegment [constr] StartX=-196.492 StartY=30.2278 StartZ=0 EndX=-189.914 EndY=27.8336 EndZ=0
    g5: LineSegment StartX=-194.098 StartY=36.8056 StartZ=0 EndX=-187.52 EndY=34.4115 EndZ=0
    g6: LineSegment StartX=-194.098 StartY=36.8056 StartZ=0 EndX=-198.886 EndY=23.6499 EndZ=0
    g7: LineSegment StartX=-187.52 StartY=34.4115 StartZ=0 EndX=-192.308 EndY=21.2558 EndZ=0
    g8: LineSegment StartX=-198.886 StartY=23.6499 StartZ=0 EndX=-192.308 EndY=21.2558 EndZ=0
    g9: LineSegment [constr] StartX=-187.821 StartY=29.2 StartZ=0 EndX=-188.505 EndY=27.3206 EndZ=0
  constraints (23):
    c: Symmetric(g-3,g-3,g0)
    c: Perpendicular(g1,g-3)
    c: Parallel(g2,g-3)
    c: Symmetric(g2,g2,g3)
    c: Perpendicular(g2,g4)
    c: Symmetric(g4,g4,g3)
    c: Distance(g2) = 14
    c: Distance(g4) = 7
    c: Distance(g1) = 5
    c: Parallel(g5,g4)
    c: Parallel(g7,g2)
    c: Symmetric(g5,g5,g2)
    c: Symmetric(g6,g6,g4)
    c: Symmetric(g7,g7,g4)
    c: Symmetric(g8,g8,g2)
    c: Coincident(g6,g5)
    c: Coincident(g7,g5)
    c: Coincident(g8,g7)
    c: Coincident(g3,g1)
    c: Coincident(g9,g0)
    c: Parallel(g9,g-3)
    c: Distance(g9) = 2
    c: Coincident(g1,g9)
FEATURE [Sketcher::SketchObject] Sketch058  label="buco esterno per SWITCH"
  ArcFitTolerance = 1e-06
  AttachmentSupport = -> [XZ_Plane]
  ExternalGeometry = -> [Sketch057]
  FullyConstrained = true
  MakeInternals = false
  MapMode = 5
  Placement = pos=(0,0,0) rot=(1,0,0;1.5708rad)
  sketch-geometry (12):
    g0: GeomPoint [constr] X=-190.809 Y=35.6086 Z=0
    g1: GeomPoint [constr] X=-196.492 Y=30.2278 Z=0
    g2: GeomPoint [constr] X=-189.914 Y=27.8336 Z=0
    g3: GeomPoint [constr] X=-195.597 Y=22.4529 Z=0
    g4: GeomPoint [constr] X=-193.203 Y=29.0307 Z=0
    g5: LineSegment [constr] StartX=-192.006 StartY=32.3196 StartZ=0 EndX=-194.4 EndY=25.7418 EndZ=0
    g6: GeomPoint [constr] X=-193.203 Y=29.0307 Z=0
    g7: LineSegment [constr] StartX=-195.082 StartY=29.7148 StartZ=0 EndX=-191.324 EndY=28.3467 EndZ=0
    g8: LineSegment StartX=-193.885 StartY=33.0037 StartZ=0 EndX=-190.127 EndY=31.6356 EndZ=0
    g9: LineSegment StartX=-190.127 StartY=31.6356 StartZ=0 EndX=-192.521 EndY=25.0578 EndZ=0
    g10: LineSegment StartX=-196.28 StartY=26.4258 StartZ=0 EndX=-192.521 EndY=25.0578 EndZ=0
    g11: LineSegment StartX=-193.885 StartY=33.0037 StartZ=0 EndX=-196.28 EndY=26.4258 EndZ=0
  constraints (21):
    c: Symmetric(g-6,g-6,g3)
    c: Symmetric(g-4,g-6,g2)
    c: Symmetric(g-5,g-4,g0)
    c: Symmetric(g-5,g-6,g1)
    c: Symmetric(g1,g2,g4)
    c: Parallel(g5,g-4)
    c: Symmetric(g5,g5,g6)
    c: Perpendicular(g7,g5)
    c: Symmetric(g7,g7,g6)
    c: Distance(g5) = 7
    c: Distance(g7) = 4
    c: Parallel(g8,g7)
    c: Parallel(g11,g5)
    c: Symmetric(g8,g8,g5)
    c: Symmetric(g9,g9,g7)
    c: Symmetric(g10,g10,g5)
    c: Symmetric(g11,g11,g7)
    c: Coincident(g11,g8)
    c: Coincident(g9,g8)
    c: Coincident(g9,g10)
    c: Coincident(g6,g4)
FEATURE [Part::Extrusion] Extrude060  label="Extrude buco interno per SWITCH destro"
  Base = -> Sketch057
  Dir = (0,-1,2e-16)
  DirMode = 2
  FaceMakerClass = Part::FaceMakerBullseye
  FaceMakerMode = 3
  LengthFwd = 13.2
  LengthRev = 0
  Placement = pos=(0,2.6,0) rot=(0,0,1;0rad)
  Solid = true
  Symmetric = false
FEATURE [Part::Extrusion] Extrude061  label="Extrude buco esterno per SWITCH destro"
  Base = -> Sketch058
  Dir = (0,-1,2e-16)
  DirMode = 2
  FaceMakerClass = Part::FaceMakerBullseye
  FaceMakerMode = 3
  LengthFwd = 2
  LengthRev = 0
  Placement = pos=(0,-10.6,0) rot=(0,0,1;0rad)
  Solid = true
  Symmetric = false
FEATURE [Sketcher::SketchObject] Sketch059  label="buco per spazio introduzione SWITCH"
  ArcFitTolerance = 1e-06
  AttachmentSupport = -> [XZ_Plane]
  ExternalGeometry = -> [Sketch057,Sketch010]
  FullyConstrained = true
  MakeInternals = false
  MapMode = 5
  Placement = pos=(0,0,0) rot=(1,0,0;1.5708rad)
  sketch-geometry (8):
    g0: LineSegment [constr] StartX=-201.368 StartY=36.3521 StartZ=0 EndX=-195.094 EndY=34.0687 EndZ=0
    g1: LineSegment [constr] StartX=-194.098 StartY=36.8056 StartZ=0 EndX=-195.094 EndY=34.0687 EndZ=0
    g2: LineSegment StartX=-198.658 StartY=24.2771 StartZ=0 EndX=-199.654 EndY=21.5401 EndZ=0
    g3: LineSegment StartX=-199.654 StartY=21.5401 StartZ=0 EndX=-181.196 EndY=14.822 EndZ=0
    g4: LineSegment StartX=-181.196 StartY=14.822 StartZ=0 EndX=-180.2 EndY=17.559 EndZ=0
    g5: LineSegment StartX=-180.2 StartY=17.559 StartZ=0 EndX=-198.658 EndY=24.2771 EndZ=0
    g6: LineSegment [constr] StartX=-204.932 StartY=26.5605 StartZ=0 EndX=-198.658 EndY=24.2771 EndZ=0
    g7: LineSegment [constr] StartX=-198.658 StartY=24.2771 StartZ=0 EndX=-199.654 EndY=21.5401 EndZ=0
  constraints (20):
    c: Parallel(g1,g-3)
    c: Parallel(g0,g-4)
    c: Coincident(g0,g-4)
    c: Coincident(g1,g-3)
    c: Coincident(g0,g1)
    c: Coincident(g3,g2)
    c: Coincident(g4,g3)
    c: Coincident(g5,g4)
    c: Coincident(g5,g2)
    c: Parallel(g5,g-5)
    c: Parallel(g3,g-5)
    c: Parallel(g4,g-6)
    c: DistanceX(g-6,g4) = 0
    c: Coincident(g6,g-5)
    c: Equal(g6,g0)
    c: Coincident(g7,g6)
    c: Equal(g7,g1)
    c: Tangent(g7,g-3)
    c: Coincident(g2,g6)
    c: Coincident(g2,g7)
FEATURE [Part::Extrusion] Extrude062  label="Extrude buco per spazio introduzione SWITCH"
  Base = -> Sketch059
  Dir = (0,-1,2e-16)
  DirMode = 2
  FaceMakerClass = Part::FaceMakerBullseye
  FaceMakerMode = 3
  LengthFwd = 13.2
  LengthRev = 0
  Solid = true
  Symmetric = true
FEATURE [Part::Extrusion] Extrude063  label="Extrude buco interno per SWITCH sinistro"
  Base = -> Sketch057
  Dir = (0,-1,2e-16)
  DirMode = 2
  FaceMakerClass = Part::FaceMakerBullseye
  FaceMakerMode = 3
  LengthFwd = 13.2
  LengthRev = 0
  Placement = pos=(0,10.6,0) rot=(0,0,1;0rad)
  Solid = true
  Symmetric = false
FEATURE [Part::Extrusion] Extrude064  label="Extrude buco esterno per SWITCH sinistro"
  Base = -> Sketch058
  Dir = (0,-1,2e-16)
  DirMode = 2
  FaceMakerClass = Part::FaceMakerBullseye
  FaceMakerMode = 3
  LengthFwd = 2
  LengthRev = 0
  Placement = pos=(0,12.6,0) rot=(0,0,1;0rad)
  Solid = true
  Symmetric = false
FEATURE [Sketcher::SketchObject] Sketch061  label="struttura esterna blocco switch"
  ArcFitTolerance = 1e-06
  AttachmentSupport = -> [XZ_Plane003]
  FullyConstrained = true
  MakeInternals = false
  MapMode = 5
  Placement = pos=(0,0,0) rot=(1,0,0;1.5708rad)
  sketch-geometry (5):
    g0: LineSegment StartX=-1 StartY=-5.1 StartZ=0 EndX=1 EndY=-5.1 EndZ=0
    g1: LineSegment StartX=1 StartY=-5.1 StartZ=0 EndX=1 EndY=5.1 EndZ=0
    g2: LineSegment StartX=1 StartY=5.1 StartZ=0 EndX=-1 EndY=5.1 EndZ=0
    g3: LineSegment StartX=-1 StartY=5.1 StartZ=0 EndX=-1 EndY=-5.1 EndZ=0
    g4: GeomPoint [constr] X=0 Y=0 Z=0
  constraints (12):
    c: Coincident(g0,g1)
    c: Coincident(g1,g2)
    c: Coincident(g2,g3)
    c: Coincident(g3,g0)
    c: Horizontal(g0)
    c: Horizontal(g2)
    c: Vertical(g1)
    c: Vertical(g3)
    c: Symmetric(g2,g0,g4)
    c: Distance(g1,g3) = 2
    c: Distance(g0,g2) = 10.2
    c: Coincident(g4,g-1)
FEATURE [Sketcher::SketchObject] Sketch062  label="struttura interna blocco switch"
  ArcFitTolerance = 1e-06
  AttachmentSupport = -> [XZ_Plane003]
  ExternalGeometry = -> [Sketch061]
  FullyConstrained = true
  MakeInternals = false
  MapMode = 5
  Placement = pos=(0,0,0) rot=(1,0,0;1.5708rad)
  sketch-geometry (5):
    g0: LineSegment StartX=-1 StartY=3.1 StartZ=0 EndX=-1 EndY=-3.1 EndZ=0
    g1: LineSegment StartX=-1 StartY=-3.1 StartZ=0 EndX=1 EndY=-3.1 EndZ=0
    g2: LineSegment StartX=1 StartY=-3.1 StartZ=0 EndX=1 EndY=3.1 EndZ=0
    g3: LineSegment StartX=1 StartY=3.1 StartZ=0 EndX=-1 EndY=3.1 EndZ=0
    g4: GeomPoint [constr] X=0 Y=0 Z=0
  constraints (12):
    c: Coincident(g0,g1)
    c: Coincident(g1,g2)
    c: Coincident(g2,g3)
    c: Coincident(g3,g0)
    c: Vertical(g0)
    c: Vertical(g2)
    c: Horizontal(g1)
    c: Horizontal(g3)
    c: Symmetric(g2,g0,g4)
    c: Coincident(g4,g-1)
    c: Distance(g0) = 6.2
    c: Equal(g3,g-3)
FEATURE [Sketcher::SketchObject] Sketch063  label="blocchi tra switch"
  ArcFitTolerance = 1e-06
  AttachmentSupport = -> [XZ_Plane003]
  ExternalGeometry = -> [Sketch061,Sketch062]
  FullyConstrained = true
  MakeInternals = false
  MapMode = 5
  Placement = pos=(0,0,0) rot=(1,0,0;1.5708rad)
  sketch-geometry (8):
    g0: LineSegment StartX=-3 StartY=5.1 StartZ=0 EndX=-1 EndY=5.1 EndZ=0
    g1: LineSegment StartX=-1 StartY=5.1 StartZ=0 EndX=-1 EndY=3.1 EndZ=0
    g2: LineSegment StartX=-1 StartY=3.1 StartZ=0 EndX=-3 EndY=3.1 EndZ=0
    g3: LineSegment StartX=-3 StartY=3.1 StartZ=0 EndX=-3 EndY=5.1 EndZ=0
    g4: LineSegment StartX=-3 StartY=-3.1 StartZ=0 EndX=-1 EndY=-3.1 EndZ=0
    g5: LineSegment StartX=-1 StartY=-3.1 StartZ=0 EndX=-1 EndY=-5.1 EndZ=0
    g6: LineSegment StartX=-1 StartY=-5.1 StartZ=0 EndX=-3 EndY=-5.1 EndZ=0
    g7: LineSegment StartX=-3 StartY=-5.1 StartZ=0 EndX=-3 EndY=-3.1 EndZ=0
  constraints (20):
    c: Horizontal(g0)
    c: Coincident(g1,g0)
    c: Coincident(g2,g1)
    c: Horizontal(g2)
    c: Coincident(g3,g2)
    c: Coincident(g3,g0)
    c: Vertical(g3)
    c: Horizontal(g4)
    c: Coincident(g5,g4)
    c: Coincident(g6,g5)
    c: Horizontal(g6)
    c: Coincident(g7,g6)
    c: Coincident(g7,g4)
    c: Vertical(g7)
    c: Coincident(g0,g-4)
    c: Coincident(g1,g-5)
    c: Coincident(g4,g-6)
    c: Coincident(g5,g-7)
    c: Distance(g0) = 2
    c: Distance(g4) = 2
FEATURE [Sketcher::SketchObject] Sketch066  label="piano per rampino"
  ArcFitTolerance = 1e-06
  AttachmentSupport = -> [XZ_Plane002]
  ExternalGeometry = -> [Sketch045]
  FullyConstrained = true
  MakeInternals = false
  MapMode = 5
  Placement = pos=(0,0,0) rot=(1,0,0;1.5708rad)
  sketch-geometry (4):
    g0: LineSegment StartX=5.4 StartY=5.1 StartZ=0 EndX=5.4 EndY=3.9 EndZ=0
    g1: LineSegment StartX=5.4 StartY=3.9 StartZ=0 EndX=7 EndY=3.9 EndZ=0
    g2: LineSegment StartX=7 StartY=3.9 StartZ=0 EndX=7 EndY=5.1 EndZ=0
    g3: LineSegment StartX=7 StartY=5.1 StartZ=0 EndX=5.4 EndY=5.1 EndZ=0
  constraints (11):
    c: Coincident(g0,g1)
    c: Coincident(g1,g2)
    c: Coincident(g2,g3)
    c: Coincident(g3,g0)
    c: Vertical(g0)
    c: Vertical(g2)
    c: Horizontal(g1)
    c: Horizontal(g3)
    c: Distance(g0,g2) = 1.6
    c: Distance(g1,g3) = 1.2
    c: Coincident(g2,g-3)
FEATURE [Sketcher::SketchObject] Sketch064  label="rampini_per_serraggio_struttura"
  ArcFitTolerance = 1e-06
  AttachmentSupport = -> [XZ_Plane002]
  ExternalGeometry = -> [Sketch066,Sketch045]
  FullyConstrained = true
  MakeInternals = false
  MapMode = 5
  Placement = pos=(0,0,0) rot=(1,0,0;1.5708rad)
  sketch-geometry (7):
    g0: LineSegment StartX=7 StartY=5.1 StartZ=0 EndX=7 EndY=3.9 EndZ=0
    g1: LineSegment StartX=7 StartY=3.9 StartZ=0 EndX=9 EndY=3.9 EndZ=0
    g2: LineSegment StartX=7 StartY=5.1 StartZ=0 EndX=7 EndY=5.1 EndZ=0
    g3: LineSegment StartX=7 StartY=5.1 StartZ=0 EndX=7 EndY=7.5 EndZ=0
    g4: LineSegment StartX=9 StartY=5.1 StartZ=0 EndX=9 EndY=3.9 EndZ=0
    g5: LineSegment StartX=7 StartY=7.5 StartZ=0 EndX=9 EndY=7.5 EndZ=0
    g6: LineSegment StartX=9 StartY=7.5 StartZ=0 EndX=9 EndY=5.1 EndZ=0
  constraints (20):
    c: Vertical(g0)
    c: Coincident(g1,g0)
    c: Horizontal(g1)
    c: Coincident(g2,g0)
    c: Horizontal(g2)
    c: Coincident(g3,g2)
    c: Vertical(g3)
    c: Coincident(g5,g3)
    c: Coincident(g4,g6)
    c: Coincident(g4,g1)
    c: Vertical(g4)
    c: Coincident(g0,g-3)
    c: DistanceY(g-4,g3) = 2.4
    c: DistanceX(g1,g1) = 2
    c: DistanceY(g2,g6) = 0
    c: DistanceX(g2,g2) = 0
    c: DistanceY(g0,g0) = 1.2
    c: Coincident(g5,g6)
    c: Horizontal(g5)
    c: Vertical(g6)
FEATURE [Sketcher::SketchObject] Sketch067  label="perno per blocco switch"
  ArcFitTolerance = 1e-06
  AttachmentSupport = -> [XZ_Plane]
  ExternalGeometry = -> [Sketch,Sketch010]
  FullyConstrained = true
  MakeInternals = false
  MapMode = 5
  Placement = pos=(0,0,0) rot=(1,0,0;1.5708rad)
  sketch-geometry (14):
    g0: LineSegment StartX=-191.073 StartY=24.9429 StartZ=0 EndX=-185.81 EndY=23.0276 EndZ=0
    g1: LineSegment StartX=-183.76 StartY=23.9839 StartZ=0 EndX=-182.392 EndY=27.7427 EndZ=0
    g2: LineSegment StartX=-183.348 StartY=29.7934 StartZ=0 EndX=-188.61 EndY=31.7087 EndZ=0
    g3: LineSegment StartX=-188.61 StartY=31.7087 StartZ=0 EndX=-191.073 EndY=24.9429 EndZ=0
    g4: GeomPoint [constr] X=-186.459 Y=27.0946 Z=0
    g5: LineSegment StartX=-189.022 StartY=25.8992 StartZ=0 EndX=-185.263 EndY=24.5311 EndZ=0
    g6: LineSegment StartX=-185.263 StartY=24.5311 StartZ=0 EndX=-183.895 EndY=28.2899 EndZ=0
    g7: LineSegment StartX=-183.895 StartY=28.2899 StartZ=0 EndX=-187.654 EndY=29.658 EndZ=0
    g8: LineSegment StartX=-187.654 StartY=29.658 StartZ=0 EndX=-189.022 EndY=25.8992 EndZ=0
    g9: GeomPoint [constr] X=-186.459 Y=27.0946 Z=0
    g10: ArcOfCircle CenterX=-185.263 CenterY=24.5311 CenterZ=0 NormalX=0 NormalY=0 NormalZ=1 AngleXU=0 Radius=1.6 StartAngle=4.36332 EndAngle=5.93412
    g11: GeomPoint [constr] X=-184.307 Y=22.4804 Z=0
    g12: ArcOfCircle CenterX=-183.895 CenterY=28.2899 CenterZ=0 NormalX=0 NormalY=0 NormalZ=1 AngleXU=0 Radius=1.6 StartAngle=5.93412 EndAngle=7.50492
    g13: GeomPoint [constr] X=-181.844 Y=29.2462 Z=0
  constraints (30):
    c: Coincident(g2,g3)
    c: Coincident(g3,g0)
    c: Symmetric(g13,g0,g4)
    c: Distance(g11,g3) = 7.2
    c: Distance(g0,g2) = 7.2
    c: Parallel(g3,g1)
    c: Parallel(g2,g0)
    c: Perpendicular(g2,g3)
    c: Coincident(g5,g6)
    c: Coincident(g6,g7)
    c: Coincident(g7,g8)
    c: Coincident(g8,g5)
    c: Symmetric(g7,g5,g9)
    c: Distance(g6,g8) = 4
    c: Distance(g5,g7) = 4
    c: Coincident(g9,g4)
    c: Parallel(g8,g6)
    c: Parallel(g7,g5)
    c: Perpendicular(g7,g8)
    c: Tangent(g8,g-3)
    c: Tangent(g2,g-4)
    c: PointOnObject(g11,g1)
    c: PointOnObject(g11,g0)
    c: Tangent(g1,g10) = -1.5708
    c: Tangent(g0,g10) = -1.5708
    c: PointOnObject(g13,g1)
    c: Tangent(g1,g12) = -1.5708
    c: Tangent(g2,g12) = -1.5708
    c: Equal(g10,g12)
    c: Coincident(g10,g5)
FEATURE [Part::Extrusion] Extrude072  label="Extrude perno per blocco switch"
  Base = -> Sketch067
  Dir = (0,-1,2e-16)
  DirMode = 2
  FaceMakerClass = Part::FaceMakerBullseye
  FaceMakerMode = 3
  LengthFwd = 25.2
  LengthRev = 0
  Solid = true
  Symmetric = true
FEATURE [Part::MultiFuse] Fusion
  Refine = true
  Shapes = -> [Extrude,Sweep,Extrude007,Extrude011,Extrude005,Extrude012,Extrude013,Extrude016,Extrude031,Extrude039,Extrude045,Extrude072]
FEATURE [Part::Cut] Cut
  Base = -> Fusion
  Refine = true
  Tool = -> Extrude001
FEATURE [Part::Cut] Cut001
  Base = -> Cut
  Refine = true
  Tool = -> Extrude004
FEATURE [Part::Cut] Cut002
  Base = -> Cut001
  Refine = true
  Tool = -> Extrude006
FEATURE [Part::Cut] Cut003
  Base = -> Cut002
  Refine = true
  Tool = -> Extrude008
FEATURE [Part::Cut] Cut004
  Base = -> Cut003
  Refine = true
  Tool = -> Extrude009
FEATURE [Part::Cut] Cut005
  Base = -> Cut004
  Refine = true
  Tool = -> Extrude010
FEATURE [Part::Cut] Cut006
  Base = -> Cut005
  Refine = true
  Tool = -> Extrude014
FEATURE [Part::Cut] Cut007
  Base = -> Cut006
  Refine = true
  Tool = -> Extrude015
FEATURE [Part::Cut] Cut008
  Base = -> Cut007
  Refine = true
  Tool = -> Extrude018
FEATURE [Part::Cut] Cut009
  Base = -> Cut008
  Refine = true
  Tool = -> Extrude019
FEATURE [Part::Cut] Cut010
  Base = -> Cut009
  Refine = true
  Tool = -> Extrude020
FEATURE [Part::Cut] Cut011
  Base = -> Cut010
  Refine = true
  Tool = -> Extrude021
FEATURE [Part::Cut] Cut012
  Base = -> Cut011
  Refine = true
  Tool = -> Extrude022
FEATURE [Part::Cut] Cut013
  Base = -> Cut012
  Refine = true
  Tool = -> Extrude023
FEATURE [Part::Cut] Cut014
  Base = -> Cut013
  Refine = true
  Tool = -> Extrude032
FEATURE [Part::Cut] Cut015
  Base = -> Cut014
  Refine = true
  Tool = -> Extrude033
FEATURE [Part::Cut] Cut016
  Base = -> Cut015
  Refine = true
  Tool = -> Extrude034
FEATURE [Part::Cut] Cut017
  Base = -> Cut016
  Refine = true
  Tool = -> Extrude035
FEATURE [Part::Cut] Cut018
  Base = -> Cut017
  Refine = true
  Tool = -> Extrude036
FEATURE [Part::Cut] Cut019
  Base = -> Cut018
  Refine = true
  Tool = -> Extrude037
FEATURE [Part::Cut] Cut020
  Base = -> Cut019
  Refine = true
  Tool = -> Extrude030
FEATURE [Part::Cut] Cut022
  Base = -> Cut020
  Refine = true
  Tool = -> Extrude038
FEATURE [Part::Cut] Cut023
  Base = -> Cut022
  Refine = true
  Tool = -> Extrude041
FEATURE [Part::Cut] Cut024
  Base = -> Cut023
  Refine = true
  Tool = -> Extrude040
FEATURE [Part::Cut] Cut025
  Base = -> Cut024
  Refine = true
  Tool = -> Extrude042
FEATURE [Part::Cut] Cut026
  Base = -> Cut025
  Refine = true
  Tool = -> Extrude043
FEATURE [Part::Cut] Cut027
  Base = -> Cut026
  Refine = true
  Tool = -> Extrude044
FEATURE [Part::Cut] Cut028
  Base = -> Cut027
  Refine = true
  Tool = -> Extrude046
FEATURE [Part::Cut] Cut029
  Base = -> Cut028
  Refine = true
  Tool = -> Extrude047
FEATURE [Part::Cut] Cut033
  Base = -> Cut029
  Refine = true
  Tool = -> Extrude055
FEATURE [Part::Cut] Cut034
  Base = -> Cut033
  Refine = true
  Tool = -> Extrude056
FEATURE [Part::Cut] Cut035
  Base = -> Cut034
  Refine = true
  Tool = -> Extrude057
FEATURE [Part::Cut] Cut037
  Base = -> Cut035
  Refine = true
  Tool = -> Extrude060
FEATURE [Part::Cut] Cut038
  Base = -> Cut037
  Refine = true
  Tool = -> Extrude061
FEATURE [Part::Cut] Cut039
  Base = -> Cut038
  Refine = true
  Tool = -> Extrude063
FEATURE [Part::Cut] Cut040
  Base = -> Cut039
  Refine = true
  Tool = -> Extrude064
FEATURE [Part::Cut] Cut041
  Base = -> Cut040
  Refine = true
  Tool = -> Extrude062
FEATURE [Sketcher::SketchObject] Sketch068  label="base con smusso sopra neopixel"
  ArcFitTolerance = 1e-06
  AttachmentSupport = -> [YZ_Plane002]
  FullyConstrained = true
  MakeInternals = false
  MapMode = 5
  Placement = pos=(0,0,0) rot=(0.57735,0.57735,0.57735;2.0944rad)
  sketch-geometry (5):
    g0: LineSegment StartX=-9.5 StartY=-6.1 StartZ=0 EndX=9.5 EndY=-6.1 EndZ=0
    g1: LineSegment StartX=9.5 StartY=-6.1 StartZ=0 EndX=9.5 EndY=6.1 EndZ=0
    g2: LineSegment StartX=9.5 StartY=6.1 StartZ=0 EndX=-9.5 EndY=6.1 EndZ=0
    g3: LineSegment StartX=-9.5 StartY=6.1 StartZ=0 EndX=-9.5 EndY=-6.1 EndZ=0
    g4: GeomPoint [constr] X=0 Y=0 Z=0
  constraints (12):
    c: Coincident(g0,g1)
    c: Coincident(g1,g2)
    c: Coincident(g2,g3)
    c: Coincident(g3,g0)
    c: Horizontal(g0)
    c: Horizontal(g2)
    c: Vertical(g1)
    c: Vertical(g3)
    c: Symmetric(g2,g0,g4)
    c: Distance(g1,g3) = 19
    c: Distance(g0,g2) = 12.2
    c: Coincident(g4,g-1)
FEATURE [Sketcher::SketchObject] Sketch069  label="cilindro minore"
  ArcFitTolerance = 1e-06
  AttachmentSupport = -> [XZ_Plane004]
  FullyConstrained = true
  MakeInternals = false
  MapMode = 5
  Placement = pos=(0,0,0) rot=(1,0,0;1.5708rad)
  sketch-geometry (1):
    g0: Circle CenterX=0 CenterY=0 CenterZ=0 NormalX=0 NormalY=0 NormalZ=1 AngleXU=0 Radius=5.8
  constraints (2):
    c: Diameter(g0) = 11.6
    c: Coincident(g0,g-1)
FEATURE [Sketcher::SketchObject] Sketch070  label="cilindro maggiore"
  ArcFitTolerance = 1e-06
  AttachmentSupport = -> [XZ_Plane004]
  ExternalGeometry = -> [Sketch069]
  FullyConstrained = true
  MakeInternals = false
  MapMode = 5
  Placement = pos=(0,0,0) rot=(1,0,0;1.5708rad)
  sketch-geometry (1):
    g0: Circle CenterX=0 CenterY=0 CenterZ=0 NormalX=0 NormalY=0 NormalZ=1 AngleXU=0 Radius=6.5
  constraints (2):
    c: Coincident(g0,g-1)
    c: Diameter(g0) = 13
FEATURE [Sketcher::SketchObject] Sketch071  label="buco interno"
  ArcFitTolerance = 1e-06
  AttachmentSupport = -> [XZ_Plane004]
  ExternalGeometry = -> [Sketch069]
  FullyConstrained = true
  MakeInternals = false
  MapMode = 5
  Placement = pos=(0,0,0) rot=(1,0,0;1.5708rad)
  sketch-geometry (1):
    g0: Circle CenterX=0 CenterY=0 CenterZ=0 NormalX=0 NormalY=0 NormalZ=1 AngleXU=0 Radius=5
  constraints (2):
    c: Coincident(g0,g-1)
    c: Diameter(g0) = 10
FEATURE [PartDesign::Pad] Pad
  Direction = (0,-1,2e-16)
  Length = 1.2
  Length2 = 10
  Placement = pos=(0,0,0) rot=(1,0,0;1.5708rad)
  Profile = -> Sketch070
  ReferenceAxis = -> Sketch070 [N_Axis]
  Refine = true
  Suppressed = false
  Type = 0
FEATURE [PartDesign::Pad] Pad001
  BaseFeature = -> Pad
  Direction = (0,-1,2e-16)
  Length = 5.6
  Length2 = 10
  Placement = pos=(0,0,0) rot=(1,0,0;1.5708rad)
  Profile = -> Sketch069
  ReferenceAxis = -> Sketch069 [N_Axis]
  Refine = true
  Suppressed = false
  Type = 0
FEATURE [PartDesign::Pocket] Pocket
  BaseFeature = -> Pad001
  Direction = (0,1,-2e-16)
  Length = 7
  Length2 = 5
  Midplane = true
  Placement = pos=(0,0,0) rot=(1,0,0;1.5708rad)
  Profile = -> Sketch071
  ReferenceAxis = -> Sketch071 [N_Axis]
  Refine = true
  Suppressed = false
  Type = 0
FEATURE [PartDesign::Fillet] Fillet
  Base = -> Pocket [Face7]
  BaseFeature = -> Pocket
  Placement = pos=(0,0,0) rot=(1,0,0;1.5708rad)
  Radius = 1
  Refine = true
  SupportTransform = false
  Suppressed = false
  UseAllEdges = false
FEATURE [PartDesign::Body] Body004  label="pulsanti lato sinistro"
  AllowCompound = false
  Group = -> [Sketch069,Sketch070,Sketch071,Pad,Pad001,Pocket,Fillet]
  Origin = -> Origin004
  Tip = -> Fillet
FEATURE [Sketcher::SketchObject] Sketch072  label="buco per saldature e diodo driver solenoide"
  ArcFitTolerance = 1e-06
  AttachmentSupport = -> [XZ_Plane]
  ExternalGeometry = -> [Sketch038]
  FullyConstrained = true
  MakeInternals = false
  MapMode = 5
  Placement = pos=(0,0,0) rot=(1,0,0;1.5708rad)
  sketch-geometry (4):
    g0: LineSegment StartX=-212.269 StartY=-43.9083 StartZ=0 EndX=-207.197 EndY=-33.0326 EndZ=0
    g1: LineSegment StartX=-207.197 StartY=-33.0326 StartZ=0 EndX=-207.56 EndY=-32.8635 EndZ=0
    g2: LineSegment StartX=-207.56 StartY=-32.8635 StartZ=0 EndX=-212.631 EndY=-43.7392 EndZ=0
    g3: LineSegment StartX=-212.631 StartY=-43.7392 StartZ=0 EndX=-212.269 EndY=-43.9083 EndZ=0
  constraints (11):
    c: Coincident(g1,g0)
    c: Coincident(g2,g1)
    c: Coincident(g3,g2)
    c: Coincident(g3,g0)
    c: Parallel(g-3,g0)
    c: Parallel(g0,g2)
    c: Perpendicular(g0,g3)
    c: Perpendicular(g1,g0)
    c: Distance(g3) = 0.4
    c: Distance(g2) = 12
    c: Coincident(g0,g-3)
FEATURE [Part::Extrusion] Extrude074  label="Extrude buco per saldature e diodo driver solenoide"
  Base = -> Sketch072
  Dir = (0,-1,2e-16)
  DirMode = 2
  FaceMakerClass = Part::FaceMakerBullseye
  FaceMakerMode = 3
  LengthFwd = 14.6
  LengthRev = 0
  Solid = true
  Symmetric = true
FEATURE [Part::Cut] Cut042
  Base = -> Cut041
  Refine = true
  Tool = -> Extrude074
FEATURE [Sketcher::SketchObject] Sketch073  label="fori slargati blocco solenoide"
  ArcFitTolerance = 1e-06
  AttachmentSupport = -> [XY_Plane]
  ExternalGeometry = -> [Sketch030]
  FullyConstrained = true
  MakeInternals = false
  MapMode = 5
  sketch-geometry (2):
    g0: Circle CenterX=-152.209 CenterY=6.95 CenterZ=0 NormalX=0 NormalY=0 NormalZ=1 AngleXU=0 Radius=3.7
    g1: Circle CenterX=-130.41 CenterY=-6.95 CenterZ=0 NormalX=0 NormalY=0 NormalZ=1 AngleXU=0 Radius=3.7
  constraints (4):
    c: Diameter(g0) = 7.4
    c: Coincident(g0,g-3)
    c: Diameter(g1) = 7.4
    c: Coincident(g1,g-4)
FEATURE [Part::Extrusion] Extrude075  label="Extrude fori slargati blocco solenoide"
  Base = -> Sketch073
  Dir = (0,0,1)
  DirMode = 2
  FaceMakerClass = Part::FaceMakerBullseye
  FaceMakerMode = 3
  LengthFwd = 1.5
  LengthRev = 0
  Placement = pos=(0,0,36.4) rot=(0,0,1;0rad)
  Solid = true
  Symmetric = false
FEATURE [Part::Cut] Cut043
  Base = -> Cut042
  Refine = true
  Tool = -> Extrude075
FEATURE [Sketcher::SketchObject] Sketch074  label="lato sx pistola"
  ArcFitTolerance = 1e-06
  AttachmentSupport = -> [XZ_Plane]
  ExternalGeometry = -> [Sketch016,Sketch,Sketch058]
  FullyConstrained = true
  MakeInternals = false
  MapMode = 5
  Placement = pos=(0,0,0) rot=(1,0,0;1.5708rad)
  sketch-geometry (37):
    g0: LineSegment StartX=-82.8 StartY=3.2 StartZ=0 EndX=0 EndY=3.2 EndZ=0
    g1: LineSegment StartX=-82.8 StartY=3.2 StartZ=0 EndX=-82.8 EndY=6.2 EndZ=0
    g2: LineSegment [constr] StartX=-107.6 StartY=18 StartZ=0 EndX=-107.6 EndY=20 EndZ=0
    g3: LineSegment [constr] StartX=-132.428 StartY=18 StartZ=0 EndX=-132.428 EndY=20 EndZ=0
    g4: LineSegment StartX=-132.428 StartY=20 StartZ=0 EndX=-107.6 EndY=20 EndZ=0
    g5: ArcOfCircle CenterX=-107.6 CenterY=4 CenterZ=0 NormalX=0 NormalY=0 NormalZ=1 AngleXU=0 Radius=16 StartAngle=0.137937 EndAngle=1.5708
    g6: LineSegment StartX=-82.8 StartY=6.2 StartZ=0 EndX=-91.752 EndY=6.2 EndZ=0
    g7: LineSegment [constr] StartX=-145.743 StartY=8.32624 StartZ=0 EndX=-147.645 EndY=8.94427 EndZ=0
    g8: ArcOfCircle CenterX=-132.428 CenterY=4 CenterZ=0 NormalX=0 NormalY=0 NormalZ=1 AngleXU=0 Radius=16 StartAngle=1.5708 EndAngle=2.82743
    g9: LineSegment StartX=-215.932 StartY=-80.4316 StartZ=0 EndX=-176.685 EndY=-80.4316 EndZ=0
    g10: LineSegment StartX=-147.645 StartY=8.94427 StartZ=0 EndX=-176.685 EndY=-80.4316 EndZ=0
    g11: LineSegment [constr] StartX=-193.988 StartY=-2.33927 StartZ=0 EndX=-192.176 EndY=-3.18451 EndZ=0
    g12: LineSegment [constr] StartX=-217.232 StartY=-52.1862 StartZ=0 EndX=-215.42 EndY=-53.0314 EndZ=0
    g13: LineSegment StartX=-192.176 StartY=-3.18451 StartZ=0 EndX=-215.42 EndY=-53.0314 EndZ=0
    g14: ArcOfCircle CenterX=-184.801 CenterY=-67.3089 CenterZ=0 NormalX=0 NormalY=0 NormalZ=1 AngleXU=0 Radius=33.7833 StartAngle=2.70526 EndAngle=3.54053
    g15: ArcOfCircle CenterX=-207.583 CenterY=4 CenterZ=0 NormalX=0 NormalY=0 NormalZ=1 AngleXU=0 Radius=17 StartAngle=5.84685 EndAngle=7.56663
    g16: LineSegment StartX=-202.765 StartY=20.303 StartZ=0 EndX=-195.887 EndY=39.2 EndZ=0
    g17: LineSegment [constr] StartX=-193.885 StartY=33.0037 StartZ=0 EndX=-197.644 EndY=34.3718 EndZ=0
    g18: LineSegment StartX=-195.887 StartY=39.2 StartZ=0 EndX=0 EndY=39.2 EndZ=0
    g19: LineSegment StartX=0 StartY=3.2 StartZ=0 EndX=0 EndY=39.2 EndZ=0
    g20: LineSegment StartX=-189.939 StartY=31.5672 StartZ=0 EndX=-192.333 EndY=24.9893 EndZ=0
    g21: LineSegment StartX=-196.467 StartY=26.4942 StartZ=0 EndX=-194.073 EndY=33.0721 EndZ=0
    g22: Circle CenterX=-213.443 CenterY=-76.8316 CenterZ=0 NormalX=0 NormalY=0 NormalZ=1 AngleXU=0 Radius=1.8
    g23: Circle CenterX=-179.305 CenterY=-76.8316 CenterZ=0 NormalX=0 NormalY=0 NormalZ=1 AngleXU=0 Radius=1.8
    g24: Circle CenterX=-184.08 CenterY=34.8 CenterZ=0 NormalX=0 NormalY=0 NormalZ=1 AngleXU=0 Radius=1.8
    g25: Circle CenterX=-78.51 CenterY=34.8 CenterZ=0 NormalX=0 NormalY=0 NormalZ=1 AngleXU=0 Radius=1.8
    g26: Circle CenterX=-78.51 CenterY=7.6 CenterZ=0 NormalX=0 NormalY=0 NormalZ=1 AngleXU=0 Radius=1.8
    g27: Circle CenterX=-5.6 CenterY=34.8 CenterZ=0 NormalX=0 NormalY=0 NormalZ=1 AngleXU=0 Radius=1.8
    g28: Circle CenterX=-5.6 CenterY=7.6 CenterZ=0 NormalX=0 NormalY=0 NormalZ=1 AngleXU=0 Radius=1.8
    g29: LineSegment StartX=-190.127 StartY=31.6356 StartZ=0 EndX=-189.939 EndY=31.5672 EndZ=0
    g30: LineSegment StartX=-194.073 StartY=33.0721 StartZ=0 EndX=-193.885 EndY=33.0037 EndZ=0
    g31: LineSegment StartX=-193.885 StartY=33.0037 StartZ=0 EndX=-190.127 EndY=31.6356 EndZ=0
    g32: LineSegment StartX=-196.467 StartY=26.4942 StartZ=0 EndX=-192.333 EndY=24.9893 EndZ=0
    g33: Circle CenterX=-19 CenterY=21.2 CenterZ=0 NormalX=0 NormalY=0 NormalZ=1 AngleXU=0 Radius=6.3
    g34: Circle CenterX=-42 CenterY=21.2 CenterZ=0 NormalX=0 NormalY=0 NormalZ=1 AngleXU=0 Radius=6.3
    g35: Circle CenterX=-65 CenterY=21.2 CenterZ=0 NormalX=0 NormalY=0 NormalZ=1 AngleXU=0 Radius=6.3
    g36: LineSegment [constr] StartX=-4 StartY=21.2 StartZ=0 EndX=-65 EndY=21.2 EndZ=0
  constraints (96):
    c: Coincident(g0,g-41)
    c: Horizontal(g0)
    c: PointOnObject(g0,g-39)
    c: Coincident(g1,g0)
    c: Vertical(g1)
    c: DistanceY(g1,g1) = 3
    c: Coincident(g2,g-17)
    c: Vertical(g2)
    c: Coincident(g3,g-16)
    c: Vertical(g3)
    c: DistanceY(g2,g2) = 2
    c: DistanceY(g3,g3) = 2
    c: Coincident(g4,g3)
    c: Coincident(g4,g2)
    c: Coincident(g5,g-17)
    c: Coincident(g5,g2)
    c: Coincident(g6,g1)
    c: Horizontal(g6)
    c: Coincident(g6,g5)
    c: Coincident(g7,g-15)
    c: Coincident(g8,g7)
    c: Coincident(g8,g3)
    c: Coincident(g8,g-15)
    c: Horizontal(g9)
    c: DistanceY(g-13,g9) = 2
    c: Coincident(g10,g7)
    c: Parallel(g10,g-14)
    c: Coincident(g9,g10)
    c: Distance(g11) = 2
    c: Coincident(g11,g-11)
    c: Perpendicular(g-11,g11)
    c: Distance(g12) = 2
    c: Coincident(g12,g-12)
    c: Perpendicular(g-11,g12)
    c: Coincident(g13,g11)
    c: Coincident(g13,g12)
    c: Coincident(g14,g-32)
    c: Coincident(g14,g12)
    c: Coincident(g14,g9)
    c: Coincident(g15,g-10)
    c: Coincident(g15,g11)
    c: Parallel(g16,g-22)
    c: Distance(g17) = 4
    c: PointOnObject(g17,g16)
    c: Coincident(g15,g16)
    c: Horizontal(g18)
    c: Coincident(g18,g16)
    c: Coincident(g19,g0)
    c: PointOnObject(g19,g-39)
    c: DistanceY(g19,g-36) = 2
    c: Coincident(g18,g19)
    c: Diameter(g22) = 3.6
    c: Coincident(g22,g-9)
    c: Diameter(g23) = 3.6
    c: Coincident(g23,g-8)
    c: Diameter(g24) = 3.6
    c: Diameter(g25) = 3.6
    c: Diameter(g26) = 3.6
    c: Diameter(g27) = 3.6
    c: Diameter(g28) = 3.6
    c: Coincident(g27,g-4)
    c: Coincident(g28,g-3)
    c: Coincident(g25,g-6)
    c: Coincident(g26,g-5)
    c: Coincident(g24,g-7)
    c: Parallel(g20,g-21)
    c: Equal(g20,g-21)
    c: Parallel(g21,g-19)
    c: Equal(g21,g-19)
    c: Distance(g29) = 0.2
    c: Distance(g30) = 0.2
    c: Parallel(g29,g-20)
    c: Parallel(g31,g-20)
    c: Equal(g31,g-20)
    c: Coincident(g30,g31)
    c: Coincident(g31,g29)
    c: Coincident(g29,g-21)
    c: Parallel(g30,g31)
    c: Coincident(g17,g30)
    c: Coincident(g20,g29)
    c: Coincident(g21,g30)
    c: Perpendicular(g16,g17)
    c: Coincident(g32,g21)
    c: Coincident(g32,g20)
    c: Perpendicular(g10,g7)
    c: Diameter(g33) = 12.6
    c: Diameter(g34) = 12.6
    c: Diameter(g35) = 12.6
    c: Horizontal(g36)
    c: PointOnObject(g33,g36)
    c: PointOnObject(g34,g36)
    c: DistanceX(g34,g33) = 23
    c: DistanceX(g35,g34) = 23
    c: DistanceX(g33,g36) = 15
    c: Symmetric(g-24,g-24,g36)
    c: Coincident(g36,g35)
FEATURE [Sketcher::SketchObject] Sketch075  label="lato dx pistola"
  ArcFitTolerance = 1e-06
  AttachmentSupport = -> [XZ_Plane]
  ExternalGeometry = -> [Sketch016,Sketch,Sketch058,Sketch074]
  FullyConstrained = true
  MakeInternals = false
  MapMode = 5
  Placement = pos=(0,0,0) rot=(1,0,0;1.5708rad)
  sketch-geometry (61):
    g0: LineSegment StartX=-82.8 StartY=3.2 StartZ=0 EndX=0 EndY=3.2 EndZ=0
    g1: LineSegment StartX=-82.8 StartY=3.2 StartZ=0 EndX=-82.8 EndY=6.2 EndZ=0
    g2: LineSegment [constr] StartX=-107.6 StartY=18 StartZ=0 EndX=-107.6 EndY=20 EndZ=0
    g3: LineSegment [constr] StartX=-132.428 StartY=18 StartZ=0 EndX=-132.428 EndY=20 EndZ=0
    g4: LineSegment StartX=-132.428 StartY=20 StartZ=0 EndX=-107.6 EndY=20 EndZ=0
    g5: ArcOfCircle CenterX=-107.6 CenterY=4 CenterZ=0 NormalX=0 NormalY=0 NormalZ=1 AngleXU=0 Radius=16 StartAngle=0.137937 EndAngle=1.5708
    g6: LineSegment StartX=-82.8 StartY=6.2 StartZ=0 EndX=-91.752 EndY=6.2 EndZ=0
    g7: LineSegment [constr] StartX=-145.743 StartY=8.32624 StartZ=0 EndX=-147.645 EndY=8.94427 EndZ=0
    g8: ArcOfCircle CenterX=-132.428 CenterY=4 CenterZ=0 NormalX=0 NormalY=0 NormalZ=1 AngleXU=0 Radius=16 StartAngle=1.5708 EndAngle=2.82743
    g9: LineSegment StartX=-215.932 StartY=-80.4316 StartZ=0 EndX=-176.685 EndY=-80.4316 EndZ=0
    g10: LineSegment StartX=-147.645 StartY=8.94427 StartZ=0 EndX=-176.685 EndY=-80.4316 EndZ=0
    g11: LineSegment [constr] StartX=-193.988 StartY=-2.33927 StartZ=0 EndX=-192.176 EndY=-3.18451 EndZ=0
    g12: LineSegment [constr] StartX=-217.232 StartY=-52.1862 StartZ=0 EndX=-215.42 EndY=-53.0314 EndZ=0
    g13: LineSegment StartX=-192.176 StartY=-3.18451 StartZ=0 EndX=-215.42 EndY=-53.0314 EndZ=0
    g14: ArcOfCircle CenterX=-184.801 CenterY=-67.3089 CenterZ=0 NormalX=0 NormalY=0 NormalZ=1 AngleXU=0 Radius=33.7833 StartAngle=2.70526 EndAngle=3.54053
    g15: ArcOfCircle CenterX=-207.583 CenterY=4 CenterZ=0 NormalX=0 NormalY=0 NormalZ=1 AngleXU=0 Radius=17 StartAngle=5.84685 EndAngle=7.56663
    g16: LineSegment StartX=-202.765 StartY=20.303 StartZ=0 EndX=-195.887 EndY=39.2 EndZ=0
    g17: LineSegment [constr] StartX=-193.885 StartY=33.0037 StartZ=0 EndX=-197.644 EndY=34.3718 EndZ=0
    g18: LineSegment StartX=-195.887 StartY=39.2 StartZ=0 EndX=0 EndY=39.2 EndZ=0
    g19: LineSegment StartX=0 StartY=3.2 StartZ=0 EndX=0 EndY=39.2 EndZ=0
    g20: LineSegment StartX=-189.939 StartY=31.5672 StartZ=0 EndX=-192.333 EndY=24.9893 EndZ=0
    g21: LineSegment StartX=-196.467 StartY=26.4942 StartZ=0 EndX=-194.073 EndY=33.0721 EndZ=0
    g22: Circle CenterX=-213.443 CenterY=-76.8316 CenterZ=0 NormalX=0 NormalY=0 NormalZ=1 AngleXU=0 Radius=1.8
    g23: Circle CenterX=-179.305 CenterY=-76.8316 CenterZ=0 NormalX=0 NormalY=0 NormalZ=1 AngleXU=0 Radius=1.8
    g24: Circle CenterX=-184.08 CenterY=34.8 CenterZ=0 NormalX=0 NormalY=0 NormalZ=1 AngleXU=0 Radius=1.8
    g25: Circle CenterX=-78.51 CenterY=34.8 CenterZ=0 NormalX=0 NormalY=0 NormalZ=1 AngleXU=0 Radius=1.8
    g26: Circle CenterX=-78.51 CenterY=7.6 CenterZ=0 NormalX=0 NormalY=0 NormalZ=1 AngleXU=0 Radius=1.8
    g27: Circle CenterX=-5.6 CenterY=34.8 CenterZ=0 NormalX=0 NormalY=0 NormalZ=1 AngleXU=0 Radius=1.8
    g28: Circle CenterX=-5.6 CenterY=7.6 CenterZ=0 NormalX=0 NormalY=0 NormalZ=1 AngleXU=0 Radius=1.8
    g29: LineSegment StartX=-190.127 StartY=31.6356 StartZ=0 EndX=-189.939 EndY=31.5672 EndZ=0
    g30: LineSegment StartX=-194.073 StartY=33.0721 StartZ=0 EndX=-193.885 EndY=33.0037 EndZ=0
    g31: LineSegment StartX=-193.885 StartY=33.0037 StartZ=0 EndX=-190.127 EndY=31.6356 EndZ=0
    g32: LineSegment StartX=-196.467 StartY=26.4942 StartZ=0 EndX=-192.333 EndY=24.9893 EndZ=0
    g33: LineSegment [constr] StartX=-4 StartY=21.2 StartZ=0 EndX=-87.91 EndY=21.2 EndZ=0
    g34: GeomPoint [constr] X=-4 Y=21.2 Z=0
    g35: LineSegment [constr] StartX=-15.2 StartY=33.7 StartZ=0 EndX=-15.2 EndY=8.7 EndZ=0
    g36: LineSegment [constr] StartX=-15.2 StartY=33.7 StartZ=0 EndX=-56.2 EndY=33.7 EndZ=0
    g37: LineSegment [constr] StartX=-15.2 StartY=8.7 StartZ=0 EndX=-56.2 EndY=8.7 EndZ=0
    g38: LineSegment [constr] StartX=-56.2 StartY=33.7 StartZ=0 EndX=-56.2 EndY=8.7 EndZ=0
    g39: Circle CenterX=-18.6 CenterY=30.3 CenterZ=0 NormalX=0 NormalY=0 NormalZ=1 AngleXU=0 Radius=3.4
    g40: Circle CenterX=-18.6 CenterY=12.1 CenterZ=0 NormalX=0 NormalY=0 NormalZ=1 AngleXU=0 Radius=3.4
    g41: Circle CenterX=-43.2 CenterY=30.3 CenterZ=0 NormalX=0 NormalY=0 NormalZ=1 AngleXU=0 Radius=3.4
    g42: Circle CenterX=-43.2 CenterY=12.1 CenterZ=0 NormalX=0 NormalY=0 NormalZ=1 AngleXU=0 Radius=3.4
    g43: LineSegment [constr] StartX=-4 StartY=21.2 StartZ=0 EndX=-15.2 EndY=21.2 EndZ=0
    g44: LineSegment [constr] StartX=-15.2 StartY=21.2 StartZ=0 EndX=-36.2 EndY=21.2 EndZ=0
    g45: LineSegment [constr] StartX=-41.5 StartY=16.2 StartZ=0 EndX=-30.9 EndY=16.2 EndZ=0
    g46: LineSegment [constr] StartX=-30.9 StartY=16.2 StartZ=0 EndX=-30.9 EndY=26.2 EndZ=0
    g47: LineSegment [constr] StartX=-30.9 StartY=26.2 StartZ=0 EndX=-41.5 EndY=26.2 EndZ=0
    g48: LineSegment [constr] StartX=-41.5 StartY=26.2 StartZ=0 EndX=-41.5 EndY=16.2 EndZ=0
    g49: GeomPoint [constr] X=-36.2 Y=21.2 Z=0
    g50: Circle CenterX=-36.2 CenterY=21.2 CenterZ=0 NormalX=0 NormalY=0 NormalZ=1 AngleXU=0 Radius=2.8
    g51: LineSegment [constr] StartX=-24.2 StartY=26.7 StartZ=0 EndX=-24.2 EndY=15.7 EndZ=0
    g52: Circle CenterX=-24.2 CenterY=26.7 CenterZ=0 NormalX=0 NormalY=0 NormalZ=1 AngleXU=0 Radius=3
    g53: Circle CenterX=-24.2 CenterY=15.7 CenterZ=0 NormalX=0 NormalY=0 NormalZ=1 AngleXU=0 Radius=3
    g54: GeomPoint X=-18.6 Y=30.3 Z=0
    g55: GeomPoint X=-18.6 Y=12.1 Z=0
    g56: GeomPoint X=-43.2 Y=12.1 Z=0
    g57: GeomPoint X=-43.2 Y=30.3 Z=0
    g58: Circle CenterX=-65 CenterY=21.2 CenterZ=0 NormalX=0 NormalY=0 NormalZ=1 AngleXU=0 Radius=1.5
    g59: Circle CenterX=-42 CenterY=21.2 CenterZ=0 NormalX=0 NormalY=0 NormalZ=1 AngleXU=0 Radius=1.5
    g60: Circle CenterX=-19 CenterY=21.2 CenterZ=0 NormalX=0 NormalY=0 NormalZ=1 AngleXU=0 Radius=1.5
  constraints (149):
    c: Coincident(g0,g-41)
    c: Horizontal(g0)
    c: PointOnObject(g0,g-39)
    c: Coincident(g1,g0)
    c: Vertical(g1)
    c: DistanceY(g1,g1) = 3
    c: Coincident(g2,g-17)
    c: Vertical(g2)
    c: Coincident(g3,g-16)
    c: Vertical(g3)
    c: DistanceY(g2,g2) = 2
    c: DistanceY(g3,g3) = 2
    c: Coincident(g4,g3)
    c: Coincident(g4,g2)
    c: Coincident(g5,g-17)
    c: Coincident(g5,g2)
    c: Coincident(g6,g1)
    c: Horizontal(g6)
    c: Coincident(g6,g5)
    c: Coincident(g7,g-15)
    c: Coincident(g8,g7)
    c: Coincident(g8,g3)
    c: Coincident(g8,g-15)
    c: Horizontal(g9)
    c: DistanceY(g-13,g9) = 2
    c: Coincident(g10,g7)
    c: Parallel(g10,g-14)
    c: Coincident(g9,g10)
    c: Distance(g11) = 2
    c: Coincident(g11,g-11)
    c: Perpendicular(g-11,g11)
    c: Distance(g12) = 2
    c: Coincident(g12,g-12)
    c: Perpendicular(g-11,g12)
    c: Coincident(g13,g11)
    c: Coincident(g13,g12)
    c: Coincident(g14,g-32)
    c: Coincident(g14,g12)
    c: Coincident(g14,g9)
    c: Coincident(g15,g-10)
    c: Coincident(g15,g11)
    c: Parallel(g16,g-22)
    c: Distance(g17) = 4
    c: PointOnObject(g17,g16)
    c: Coincident(g15,g16)
    c: Horizontal(g18)
    c: Coincident(g18,g16)
    c: Coincident(g19,g0)
    c: PointOnObject(g19,g-39)
    c: DistanceY(g19,g-36) = 2
    c: Coincident(g18,g19)
    c: Diameter(g22) = 3.6
    c: Coincident(g22,g-9)
    c: Diameter(g23) = 3.6
    c: Coincident(g23,g-8)
    c: Diameter(g24) = 3.6
    c: Diameter(g25) = 3.6
    c: Diameter(g26) = 3.6
    c: Diameter(g27) = 3.6
    c: Diameter(g28) = 3.6
    c: Coincident(g27,g-4)
    c: Coincident(g28,g-3)
    c: Coincident(g25,g-6)
    c: Coincident(g26,g-5)
    c: Coincident(g24,g-7)
    c: Parallel(g20,g-21)
    c: Equal(g20,g-21)
    c: Parallel(g21,g-19)
    c: Equal(g21,g-19)
    c: Distance(g29) = 0.2
    c: Distance(g30) = 0.2
    c: Parallel(g29,g-20)
    c: Parallel(g31,g-20)
    c: Equal(g31,g-20)
    c: Coincident(g30,g31)
    c: Coincident(g31,g29)
    c: Coincident(g29,g-21)
    c: Parallel(g30,g31)
    c: Coincident(g17,g30)
    c: Coincident(g20,g29)
    c: Coincident(g21,g30)
    c: Perpendicular(g16,g17)
    c: Coincident(g32,g21)
    c: Coincident(g32,g20)
    c: Perpendicular(g10,g7)
    c: Horizontal(g33)
    c: Symmetric(g-24,g-24,g33)
    c: PointOnObject(g33,g-28)
    c: Symmetric(g-24,g-24,g34)
    c: DistanceY(g35,g35) = 25
    c: Symmetric(g35,g35,g33)
    c: Distance(g36) = 41
    c: Coincident(g36,g35)
    c: Horizontal(g36)
    c: Coincident(g37,g35)
    c: Horizontal(g37)
    c: Coincident(g38,g36)
    c: Vertical(g38)
    c: Coincident(g37,g38)
    c: Diameter(g39) = 6.8
    c: Diameter(g40) = 6.8
    c: Tangent(g39,g36)
    c: Tangent(g40,g37)
    c: Tangent(g39,g35)
    c: Tangent(g40,g35)
    c: Diameter(g41) = 6.8
    c: Diameter(g42) = 6.8
    c: Tangent(g41,g36)
    c: Tangent(g42,g37)
    c: DistanceX(g41,g39) = 24.6
    c: DistanceX(g42,g40) = 24.6
    c: Distance(g43) = 11.2
    c: Coincident(g43,g33)
    c: PointOnObject(g43,g33)
    c: PointOnObject(g43,g35)
    c: Distance(g44) = 21
    c: Coincident(g44,g43)
    c: PointOnObject(g44,g33)
    c: Coincident(g45,g46)
    c: Coincident(g46,g47)
    c: Coincident(g47,g48)
    c: Coincident(g48,g45)
    c: Horizontal(g45)
    c: Horizontal(g47)
    c: Vertical(g46)
    c: Vertical(g48)
    c: Symmetric(g47,g45,g49)
    c: Distance(g46,g48) = 10.6
    c: Distance(g45,g47) = 10
    c: Coincident(g49,g44)
    c: Diameter(g50) = 5.6
    c: Coincident(g50,g44)
    c: Distance(g51) = 11
    c: Symmetric(g51,g51,g33)
    c: DistanceX(g51,g43) = 9
    c: Diameter(g52) = 6
    c: Coincident(g52,g51)
    c: Diameter(g53) = 6
    c: Coincident(g53,g51)
    c: Coincident(g40,g55)
    c: Coincident(g39,g54)
    c: Coincident(g41,g57)
    c: Coincident(g42,g56)
    c: Diameter(g58) = 3
    c: Diameter(g59) = 3
    c: Diameter(g60) = 3
    c: Coincident(g58,g-44)
    c: Coincident(g59,g-46)
    c: Coincident(g60,g-45)
FEATURE [Sketcher::SketchObject] Sketch078
  ArcFitTolerance = 1e-06
  AttachmentSupport = -> [XZ_Plane005]
  FullyConstrained = true
  MakeInternals = false
  MapMode = 5
  Placement = pos=(0,0,0) rot=(1,0,0;1.5708rad)
  sketch-geometry (5):
    g0: LineSegment [constr] StartX=0 StartY=5.5 StartZ=0 EndX=0 EndY=-5.5 EndZ=0
    g1: ArcOfCircle CenterX=0 CenterY=5.5 CenterZ=0 NormalX=0 NormalY=0 NormalZ=1 AngleXU=0 Radius=2.7 StartAngle=0 EndAngle=3.14159
    g2: ArcOfCircle CenterX=0 CenterY=-5.5 CenterZ=0 NormalX=0 NormalY=0 NormalZ=1 AngleXU=0 Radius=2.7 StartAngle=3.1416 EndAngle=6.28318
    g3: LineSegment StartX=-2.7 StartY=5.5 StartZ=0 EndX=-2.7 EndY=-5.50001 EndZ=0
    g4: LineSegment StartX=2.7 StartY=5.5 StartZ=0 EndX=2.7 EndY=-5.50001 EndZ=0
  constraints (13):
    c: Distance(g0) = 11
    c: Vertical(g0)
    c: Symmetric(g0,g0,g-1)
    c: Radius(g1) = 2.7
    c: Coincident(g1,g0)
    c: Radius(g2) = 2.7
    c: Coincident(g2,g0)
    c: Vertical(g3)
    c: Vertical(g4)
    c: Coincident(g2,g4)
    c: Coincident(g2,g3)
    c: Tangent(g3,g1) = -1.5708
    c: Tangent(g4,g1) = 1.5708
FEATURE [PartDesign::Pad] Pad002
  Direction = (0,-1,2e-16)
  Length = 0.8
  Length2 = 10
  Placement = pos=(0,0,0) rot=(1,0,0;1.5708rad)
  Profile = -> Sketch078
  ReferenceAxis = -> Sketch078 [N_Axis]
  Refine = true
  Suppressed = false
  Type = 0
FEATURE [Sketcher::SketchObject] Sketch079
  ArcFitTolerance = 1e-06
  AttachmentSupport = -> [XZ_Plane005]
  ExternalGeometry = -> [Sketch078]
  FullyConstrained = true
  MakeInternals = false
  MapMode = 5
  Placement = pos=(0,0,0) rot=(1,0,0;1.5708rad)
  sketch-geometry (2):
    g0: Circle CenterX=-1e-16 CenterY=5.5 CenterZ=0 NormalX=0 NormalY=0 NormalZ=1 AngleXU=0 Radius=2.7
    g1: Circle CenterX=0 CenterY=-5.5 CenterZ=0 NormalX=0 NormalY=0 NormalZ=1 AngleXU=0 Radius=2.7
  constraints (4):
    c: Coincident(g0,g-3)
    c: PointOnObject(g-3,g0)
    c: Coincident(g1,g-4)
    c: Equal(g1,g-4)
FEATURE [PartDesign::Pad] Pad003
  BaseFeature = -> Pad002
  Direction = (0,-1,2e-16)
  Length = 5
  Length2 = 10
  Placement = pos=(0,0,0) rot=(1,0,0;1.5708rad)
  Profile = -> Sketch079
  ReferenceAxis = -> Sketch079 [N_Axis]
  Refine = true
  Suppressed = false
  Type = 0
FEATURE [PartDesign::Fillet] Fillet001
  Base = -> Pad003 [Edge16,Edge14]
  BaseFeature = -> Pad003
  Placement = pos=(0,0,0) rot=(1,0,0;1.5708rad)
  Radius = 0.4
  Refine = true
  SupportTransform = false
  Suppressed = false
  UseAllEdges = false
FEATURE [PartDesign::Body] Body005  label="pulsanti lato destro"
  AllowCompound = false
  Group = -> [Sketch078,Pad002,Sketch079,Pad003,Fillet001]
  Origin = -> Origin005
  Tip = -> Fillet001
FEATURE [PartDesign::SubShapeBinder] Binder
  BindCopyOnChange = 0
  BindMode = 0
  ClaimChildren = false
  Context = -> Body006 [Binder.]
  Fuse = false
  MakeFace = true
  OffsetFill = false
  OffsetIntersection = false
  OffsetJoinType = 0
  OffsetOpenResult = false
  PartialLoad = false
  Refine = true
  Relative = true
  Support = -> [Body[Sketch074.]]
  _Version = 2
FEATURE [PartDesign::SubShapeBinder] Binder001
  BindCopyOnChange = 0
  BindMode = 0
  ClaimChildren = false
  Context = -> Body007 [Binder001.]
  Fuse = false
  MakeFace = true
  OffsetFill = false
  OffsetIntersection = false
  OffsetJoinType = 0
  OffsetOpenResult = false
  PartialLoad = false
  Refine = true
  Relative = true
  Support = -> [Body[Sketch075.]]
  _Version = 2
FEATURE [Mesh::Feature] logo_per_PCB_definitivo_positivo
  Placement = pos=(-191,17,-66) rot=(0,1,1;0rad)
FEATURE [Sketcher::SketchObject] Sketch114  label="Sketch114 - base lato DX"
  ArcFitTolerance = 1e-06
  AttachmentSupport = -> [Binder001]
  ExternalGeometry = -> [Binder001]
  FullyConstrained = true
  MakeInternals = false
  MapMode = 5
  Placement = pos=(0,1e-15,0) rot=(0,0.707107,0.707107;3.14159rad)
  sketch-geometry (30):
    g0: Circle CenterX=5.6 CenterY=34.8 CenterZ=0 NormalX=0 NormalY=0 NormalZ=1 AngleXU=0 Radius=1.8
    g1: Circle CenterX=5.6 CenterY=7.6 CenterZ=0 NormalX=0 NormalY=0 NormalZ=1 AngleXU=0 Radius=1.8
    g2: Circle CenterX=24.2 CenterY=26.7 CenterZ=0 NormalX=0 NormalY=0 NormalZ=1 AngleXU=0 Radius=3
    g3: Circle CenterX=24.2 CenterY=15.7 CenterZ=0 NormalX=0 NormalY=0 NormalZ=1 AngleXU=0 Radius=3
    g4: Circle CenterX=36.2 CenterY=21.2 CenterZ=0 NormalX=0 NormalY=0 NormalZ=1 AngleXU=0 Radius=2.8
    g5: Circle CenterX=78.51 CenterY=34.8 CenterZ=0 NormalX=0 NormalY=0 NormalZ=1 AngleXU=0 Radius=1.8
    g6: Circle CenterX=78.51 CenterY=7.6 CenterZ=0 NormalX=0 NormalY=0 NormalZ=1 AngleXU=0 Radius=1.8
    g7: Circle CenterX=184.08 CenterY=34.8 CenterZ=0 NormalX=0 NormalY=0 NormalZ=1 AngleXU=0 Radius=1.8
    g8: Circle CenterX=213.443 CenterY=-76.8316 CenterZ=0 NormalX=0 NormalY=0 NormalZ=1 AngleXU=0 Radius=1.8
    g9: Circle CenterX=179.305 CenterY=-76.8316 CenterZ=0 NormalX=0 NormalY=0 NormalZ=1 AngleXU=0 Radius=1.8
    g10: ArcOfCircle [constr] CenterX=132.428 CenterY=4 CenterZ=0 NormalX=0 NormalY=0 NormalZ=1 AngleXU=0 Radius=16 StartAngle=0.314159 EndAngle=1.5708
    g11: ArcOfCircle CenterX=107.6 CenterY=4 CenterZ=0 NormalX=0 NormalY=0 NormalZ=1 AngleXU=0 Radius=16 StartAngle=1.5708 EndAngle=3.00366
    g12: ArcOfCircle CenterX=207.583 CenterY=4 CenterZ=0 NormalX=0 NormalY=0 NormalZ=1 AngleXU=0 Radius=17 StartAngle=1.85815 EndAngle=3.57792
    g13: ArcOfCircle CenterX=184.801 CenterY=-67.3089 CenterZ=0 NormalX=0 NormalY=0 NormalZ=1 AngleXU=0 Radius=33.7833 StartAngle=5.88425 EndAngle=6.71952
    g14: LineSegment StartX=0 StartY=39.2 StartZ=0 EndX=0 EndY=3.2 EndZ=0
    g15: LineSegment StartX=0 StartY=3.2 StartZ=0 EndX=82.8 EndY=3.2 EndZ=0
    g16: LineSegment StartX=82.8 StartY=3.2 StartZ=0 EndX=82.8 EndY=6.2 EndZ=0
    g17: LineSegment StartX=82.8 StartY=6.2 StartZ=0 EndX=91.752 EndY=6.2 EndZ=0
    g18: LineSegment StartX=107.6 StartY=20 StartZ=0 EndX=132.428 EndY=20 EndZ=0
    g19: LineSegment StartX=147.645 StartY=8.94427 StartZ=0 EndX=176.685 EndY=-80.4316 EndZ=0
    g20: LineSegment StartX=176.685 StartY=-80.4316 StartZ=0 EndX=215.932 EndY=-80.4316 EndZ=0
    g21: LineSegment StartX=215.42 StartY=-53.0314 StartZ=0 EndX=192.176 EndY=-3.18451 EndZ=0
    g22: LineSegment StartX=202.765 StartY=20.303 StartZ=0 EndX=195.887 EndY=39.2 EndZ=0
    g23: LineSegment StartX=195.887 StartY=39.2 StartZ=0 EndX=0 EndY=39.2 EndZ=0
    g24: LineSegment StartX=196.467 StartY=26.4942 StartZ=0 EndX=194.073 EndY=33.0721 EndZ=0
    g25: LineSegment StartX=194.073 StartY=33.0721 StartZ=0 EndX=189.939 EndY=31.5672 EndZ=0
    g26: LineSegment StartX=189.939 StartY=31.5672 StartZ=0 EndX=192.333 EndY=24.9893 EndZ=0
    g27: LineSegment StartX=192.333 StartY=24.9893 StartZ=0 EndX=196.467 EndY=26.4942 EndZ=0
    g28: LineSegment StartX=132.428 StartY=20 StartZ=0 EndX=144.053 EndY=20 EndZ=0
    g29: LineSegment StartX=144.053 StartY=20 StartZ=0 EndX=147.645 EndY=8.94427 EndZ=0
  constraints (65):
    c: Equal(g0,g-25)
    c: Equal(g2,g-29)
    c: Equal(g3,g-30)
    c: Equal(g4,g-28)
    c: Equal(g1,g-26)
    c: Coincident(g0,g-25)
    c: Coincident(g1,g-26)
    c: Coincident(g2,g-29)
    c: Coincident(g3,g-30)
    c: Coincident(g4,g-28)
    c: Equal(g5,g-23)
    c: Equal(g6,g-24)
    c: Coincident(g5,g-23)
    c: Coincident(g6,g-24)
    c: Equal(g7,g-20)
    c: Coincident(g7,g-20)
    c: Equal(g9,g-22)
    c: Coincident(g9,g-22)
    c: Equal(g8,g-21)
    c: Coincident(g8,g-21)
    c: Equal(g13,g-12)
    c: Equal(g12,g-14)
    c: Equal(g10,g-9)
    c: Equal(g11,g-7)
    c: Coincident(g14,g-27)
    c: Coincident(g14,g-27)
    c: Coincident(g15,g14)
    c: Coincident(g15,g-5)
    c: Coincident(g16,g15)
    c: Coincident(g16,g-6)
    c: Coincident(g17,g16)
    c: Coincident(g17,g-7)
    c: Coincident(g11,g17)
    c: Coincident(g11,g-8)
    c: Coincident(g18,g11)
    c: Coincident(g18,g-9)
    c: Coincident(g10,g18)
    c: Coincident(g10,g-10)
    c: Coincident(g19,g10)
    c: Coincident(g19,g-11)
    c: Coincident(g20,g19)
    c: Coincident(g20,g-12)
    c: Coincident(g13,g20)
    c: Coincident(g13,g-13)
    c: Coincident(g21,g13)
    c: Coincident(g21,g-14)
    c: Coincident(g12,g21)
    c: Coincident(g12,g-15)
    c: Coincident(g22,g12)
    c: Coincident(g22,g-15)
    c: Coincident(g23,g22)
    c: Coincident(g23,g14)
    c: Coincident(g24,g-18)
    c: Coincident(g24,g-16)
    c: Coincident(g25,g24)
    c: Coincident(g25,g-19)
    c: Coincident(g26,g25)
    c: Coincident(g26,g-19)
    c: Coincident(g27,g26)
    c: Coincident(g27,g24)
    c: Coincident(g29,g10)
    c: Coincident(g28,g10)
    c: Coincident(g29,g28)
    c: Parallel(g28,g18)
    c: Parallel(g29,g19)
FEATURE [PartDesign::Pad] Pad011
  Direction = (0,1,-2e-16)
  Length = 2
  Length2 = 10
  Profile = -> Sketch114
  ReferenceAxis = -> Sketch114 [N_Axis]
  Refine = true
  Reversed = true
  Suppressed = false
  Type = 0
FEATURE [Sketcher::SketchObject] Sketch115
  ArcFitTolerance = 1e-06
  AttachmentSupport = -> [Pad011]
  ExternalGeometry = -> [Binder001]
  FullyConstrained = true
  MakeInternals = false
  MapMode = 5
  Placement = pos=(0,1.7e-15,0) rot=(0,0.707107,0.707107;3.14159rad)
  sketch-geometry (4):
    g0: ArcOfCircle CenterX=24.2 CenterY=26.7 CenterZ=0 NormalX=0 NormalY=0 NormalZ=1 AngleXU=0 Radius=3 StartAngle=4.48384e-08 EndAngle=3.14159
    g1: ArcOfCircle CenterX=24.2 CenterY=15.7 CenterZ=0 NormalX=0 NormalY=0 NormalZ=1 AngleXU=0 Radius=3 StartAngle=3.14159 EndAngle=6.28318
    g2: LineSegment StartX=21.2 StartY=26.7 StartZ=0 EndX=21.2 EndY=15.7 EndZ=0
    g3: LineSegment StartX=27.2 StartY=26.7 StartZ=0 EndX=27.2 EndY=15.7 EndZ=0
  constraints (12):
    c: Equal(g1,g-4)
    c: Equal(g0,g-3)
    c: Coincident(g0,g-3)
    c: Coincident(g1,g-4)
    c: Vertical(g2)
    c: Vertical(g3)
    c: Tangent(g3,g-3)
    c: Tangent(g2,g-3)
    c: Coincident(g0,g2)
    c: Coincident(g0,g3)
    c: Coincident(g1,g2)
    c: Coincident(g3,g1)
FEATURE [Sketcher::SketchObject] Sketch117  label="Sketch117 - fori per inserto M3 x 3 x 4.5"
  ArcFitTolerance = 1e-06
  AttachmentSupport = -> [Pad011]
  ExternalGeometry = -> [Binder001]
  FullyConstrained = true
  MakeInternals = false
  MapMode = 5
  Placement = pos=(0,1.7e-15,0) rot=(0,0.707107,0.707107;3.14159rad)
  sketch-geometry (4):
    g0: Circle CenterX=43.2 CenterY=30.3 CenterZ=0 NormalX=0 NormalY=0 NormalZ=1 AngleXU=0 Radius=2.25
    g1: Circle CenterX=43.2 CenterY=12.1 CenterZ=0 NormalX=0 NormalY=0 NormalZ=1 AngleXU=0 Radius=2.25
    g2: Circle CenterX=18.6 CenterY=30.3 CenterZ=0 NormalX=0 NormalY=0 NormalZ=1 AngleXU=0 Radius=2.25
    g3: Circle CenterX=18.6 CenterY=12.1 CenterZ=0 NormalX=0 NormalY=0 NormalZ=1 AngleXU=0 Radius=2.25
  constraints (8):
    c: Diameter(g0) = 4.5
    c: Diameter(g1) = 4.5
    c: Diameter(g2) = 4.5
    c: Diameter(g3) = 4.5
    c: Coincident(g2,g-3)
    c: Coincident(g3,g-6)
    c: Coincident(g0,g-4)
    c: Coincident(g1,g-5)
FEATURE [Sketcher::SketchObject] Sketch118
  ArcFitTolerance = 1e-06
  AttachmentSupport = -> [Pad011]
  ExternalGeometry = -> [Binder001]
  FullyConstrained = true
  MakeInternals = false
  MapMode = 5
  Placement = pos=(0,-2,0) rot=(1,0,0;1.5708rad)
  sketch-geometry (12):
    g0: Circle CenterX=-78.51 CenterY=34.8 CenterZ=0 NormalX=0 NormalY=0 NormalZ=1 AngleXU=0 Radius=1.8
    g1: Circle CenterX=-78.51 CenterY=7.6 CenterZ=0 NormalX=0 NormalY=0 NormalZ=1 AngleXU=0 Radius=1.8
    g2: Circle CenterX=-5.6 CenterY=34.8 CenterZ=0 NormalX=0 NormalY=0 NormalZ=1 AngleXU=0 Radius=1.8
    g3: Circle CenterX=-5.6 CenterY=7.6 CenterZ=0 NormalX=0 NormalY=0 NormalZ=1 AngleXU=0 Radius=1.8
    g4: LineSegment StartX=0 StartY=39.2 StartZ=0 EndX=0 EndY=3.2 EndZ=0
    g5: LineSegment StartX=0 StartY=3.2 StartZ=0 EndX=-82.8 EndY=3.2 EndZ=0
    g6: LineSegment StartX=-82.8 StartY=3.2 StartZ=0 EndX=-82.8 EndY=39.2 EndZ=0
    g7: LineSegment StartX=-82.8 StartY=39.2 StartZ=0 EndX=0 EndY=39.2 EndZ=0
    g8: ArcOfCircle CenterX=-65 CenterY=21.2 CenterZ=0 NormalX=0 NormalY=0 NormalZ=1 AngleXU=0 Radius=10 StartAngle=1.5708 EndAngle=4.71239
    g9: ArcOfCircle CenterX=-19 CenterY=21.2 CenterZ=0 NormalX=0 NormalY=0 NormalZ=1 AngleXU=0 Radius=10 StartAngle=4.71239 EndAngle=7.85398
    g10: LineSegment StartX=-65 StartY=31.2 StartZ=0 EndX=-19 EndY=31.2 EndZ=0
    g11: LineSegment StartX=-65 StartY=11.2 StartZ=0 EndX=-19 EndY=11.2 EndZ=0
  constraints (25):
    c: Equal(g2,g-5)
    c: Equal(g3,g-7)
    c: Equal(g1,g-6)
    c: Equal(g0,g-4)
    c: Coincident(g0,g-4)
    c: Coincident(g1,g-6)
    c: Coincident(g3,g-7)
    c: Coincident(g2,g-5)
    c: Coincident(g4,g-8)
    c: Coincident(g4,g-9)
    c: Coincident(g5,g4)
    c: Coincident(g5,g-10)
    c: Coincident(g6,g5)
    c: PointOnObject(g6,g-3)
    c: Vertical(g6)
    c: Coincident(g7,g6)
    c: Coincident(g7,g4)
    c: Tangent(g8,g10) = 1.5708
    c: Tangent(g8,g11) = -1.5708
    c: Tangent(g9,g10) = 1.5708
    c: Tangent(g9,g11) = -1.5708
    c: Equal(g8,g9)
    c: Radius(g8) = 10
    c: Coincident(g8,g-11)
    c: Coincident(g9,g-12)
FEATURE [Sketcher::SketchObject] Sketch120
  ArcFitTolerance = 1e-06
  AttachmentSupport = -> [Pad011]
  ExternalGeometry = -> [Binder001]
  FullyConstrained = true
  MakeInternals = false
  MapMode = 5
  Placement = pos=(0,-2,0) rot=(1,0,0;1.5708rad)
  sketch-geometry (4):
    g0: LineSegment StartX=-137.815 StartY=39.2 StartZ=0 EndX=-142.655 EndY=24.303 EndZ=0
    g1: LineSegment StartX=-137.815 StartY=39.2 StartZ=0 EndX=-110.815 EndY=39.2 EndZ=0
    g2: LineSegment StartX=-142.655 StartY=24.303 StartZ=0 EndX=-110.815 EndY=24.303 EndZ=0
    g3: ArcOfCircle CenterX=-92.2534 CenterY=31.7515 CenterZ=0 NormalX=0 NormalY=0 NormalZ=1 AngleXU=0 Radius=20 StartAngle=2.75997 EndAngle=3.52321
  constraints (12):
    c: PointOnObject(g0,g-3)
    c: Coincident(g1,g0)
    c: PointOnObject(g1,g-3)
    c: Coincident(g2,g0)
    c: Horizontal(g2)
    c: Tangent(g0,g-4)
    c: Vertical(g2,g1)
    c: DistanceX(g1,g1) = 27
    c: DistanceY(g-6,g0) = 4
    c: Radius(g3) = 20
    c: Coincident(g3,g1)
    c: Coincident(g3,g2)
FEATURE [Sketcher::SketchObject] Sketch121
  ArcFitTolerance = 1e-06
  AttachmentSupport = -> [Pad011]
  ExternalGeometry = -> [Binder001]
  FullyConstrained = true
  MakeInternals = false
  MapMode = 5
  Placement = pos=(0,-2,0) rot=(1,0,0;1.5708rad)
  sketch-geometry (15):
    g0: LineSegment StartX=-137.815 StartY=39.2 StartZ=0 EndX=-143.955 EndY=20.303 EndZ=0
    g1: LineSegment StartX=-143.955 StartY=20.303 StartZ=0 EndX=-190.141 EndY=20.303 EndZ=0
    g2: LineSegment StartX=-190.141 StartY=20.303 StartZ=0 EndX=-186.139 EndY=31.3 EndZ=0
    g3: LineSegment StartX=-178.754 StartY=39.2 StartZ=0 EndX=-180.791 EndY=33.6029 EndZ=0
    g4: ArcOfCircle CenterX=-184.08 CenterY=34.8 CenterZ=0 NormalX=0 NormalY=0 NormalZ=1 AngleXU=0 Radius=3.5 StartAngle=4.71239 EndAngle=5.93412
    g5: LineSegment StartX=-184.08 StartY=31.3 StartZ=0 EndX=-186.139 EndY=31.3 EndZ=0
    g6: LineSegment StartX=-137.815 StartY=39.2 StartZ=0 EndX=-156.815 EndY=39.2 EndZ=0
    g7: LineSegment StartX=-168.815 StartY=39.2 StartZ=0 EndX=-178.754 EndY=39.2 EndZ=0
    g8: LineSegment StartX=-157.815 StartY=39.2 StartZ=0 EndX=-167.815 EndY=39.2 EndZ=0
    g9: LineSegment StartX=-168.815 StartY=31.2 StartZ=0 EndX=-156.815 EndY=31.2 EndZ=0
    g10: LineSegment StartX=-167.436 StartY=36.2 StartZ=0 EndX=-157.436 EndY=36.2 EndZ=0
    g11: ArcOfCircle CenterX=-176.411 CenterY=35.2 CenterZ=0 NormalX=0 NormalY=0 NormalZ=1 AngleXU=0 Radius=20 StartAngle=6.08183 EndAngle=6.48454
    g12: ArcOfCircle CenterX=-188.411 CenterY=35.2 CenterZ=0 NormalX=0 NormalY=0 NormalZ=1 AngleXU=0 Radius=20 StartAngle=6.08183 EndAngle=6.48454
    g13: ArcOfCircle CenterX=-177.411 CenterY=35.2 CenterZ=0 NormalX=0 NormalY=0 NormalZ=1 AngleXU=0 Radius=20 StartAngle=0.0500209 EndAngle=0.201358
    g14: ArcOfCircle CenterX=-187.411 CenterY=35.2 CenterZ=0 NormalX=0 NormalY=0 NormalZ=1 AngleXU=0 Radius=20 StartAngle=0.0500209 EndAngle=0.201358
  constraints (46):
    c: PointOnObject(g0,g-3)
    c: Tangent(g0,g-5)
    c: Coincident(g1,g0)
    c: Horizontal(g1)
    c: Coincident(g2,g1)
    c: PointOnObject(g3,g-3)
    c: Parallel(g3,g-6)
    c: Parallel(g2,g-6)
    c: Radius(g4) = 3.5
    c: Coincident(g4,g-7)
    c: Tangent(g3,g4) = 1.5708
    c: Horizontal(g5)
    c: Tangent(g5,g4) = 1.5708
    c: DistanceX(g-8,g5) = 3.8
    c: Coincident(g2,g5)
    c: Coincident(g6,g0)
    c: PointOnObject(g6,g-3)
    c: DistanceX(g6,g6) = 19
    c: PointOnObject(g7,g-3)
    c: DistanceX(g7,g6) = 12
    c: Coincident(g7,g3)
    c: PointOnObject(g8,g-3)
    c: PointOnObject(g8,g-3)
    c: DistanceX(g8,g8) = 10
    c: DistanceX(g8,g6) = 1
    c: Horizontal(g9)
    c: Vertical(g7,g9)
    c: Vertical(g6,g9)
    c: DistanceY(g9,g7) = 8
    c: Horizontal(g10)
    c: Equal(g8,g10)
    c: DistanceY(g10,g8) = 3
    c: Radius(g11) = 20
    c: Coincident(g11,g6)
    c: Coincident(g11,g9)
    c: Radius(g12) = 20
    c: Coincident(g12,g7)
    c: Coincident(g12,g9)
    c: Equal(g13,g11)
    c: Coincident(g13,g8)
    c: Coincident(g13,g10)
    c: Horizontal(g13,g11)
    c: Equal(g14,g12)
    c: Coincident(g14,g8)
    c: Coincident(g14,g10)
    c: Horizontal(g1,g-6)
FEATURE [Sketcher::SketchObject] Sketch122
  ArcFitTolerance = 1e-06
  AttachmentSupport = -> [Pad011]
  ExternalGeometry = -> [Binder001]
  FullyConstrained = true
  MakeInternals = false
  MapMode = 5
  Placement = pos=(0,-2,0) rot=(1,0,0;1.5708rad)
  sketch-geometry (8):
    g0: LineSegment StartX=-202.765 StartY=20.303 StartZ=0 EndX=-143.955 EndY=20.303 EndZ=0
    g1: ArcOfCircle CenterX=-184.801 CenterY=-67.3089 CenterZ=0 NormalX=0 NormalY=0 NormalZ=1 AngleXU=0 Radius=33.7833 StartAngle=2.70526 EndAngle=3.54053
    g2: LineSegment StartX=-176.685 StartY=-80.4316 StartZ=0 EndX=-215.932 EndY=-80.4316 EndZ=0
    g3: LineSegment StartX=-215.42 StartY=-53.0315 StartZ=0 EndX=-192.176 EndY=-3.18454 EndZ=0
    g4: ArcOfCircle CenterX=-207.583 CenterY=4 CenterZ=0 NormalX=0 NormalY=0 NormalZ=1 AngleXU=0 Radius=17 StartAngle=5.84685 EndAngle=7.56663
    g5: Circle CenterX=-213.443 CenterY=-76.8316 CenterZ=0 NormalX=0 NormalY=0 NormalZ=1 AngleXU=0 Radius=3
    g6: Circle CenterX=-179.305 CenterY=-76.8316 CenterZ=0 NormalX=0 NormalY=0 NormalZ=1 AngleXU=0 Radius=3
    g7: LineSegment StartX=-143.955 StartY=20.303 StartZ=0 EndX=-176.685 EndY=-80.4316 EndZ=0
  constraints (18):
    c: Coincident(g0,g-6)
    c: Coincident(g1,g-7)
    c: Coincident(g1,g-8)
    c: Coincident(g2,g1)
    c: Tangent(g3,g-5)
    c: Coincident(g4,g-6)
    c: Coincident(g4,g0)
    c: Coincident(g3,g4)
    c: Coincident(g1,g3)
    c: Diameter(g5) = 6
    c: Diameter(g6) = 6
    c: Coincident(g5,g-9)
    c: Coincident(g6,g-10)
    c: Horizontal(g0)
    c: Horizontal(g2)
    c: Coincident(g7,g0)
    c: Coincident(g7,g2)
    c: Tangent(g7,g-4)
FEATURE [Sketcher::SketchObject] Sketch123
  ArcFitTolerance = 1e-06
  AttachmentSupport = -> [Pad011]
  ExternalGeometry = -> [Binder001]
  FullyConstrained = true
  MakeInternals = false
  MapMode = 5
  Placement = pos=(0,-2,0) rot=(1,0,0;1.5708rad)
  sketch-geometry (4):
    g0: LineSegment StartX=-108 StartY=36.8 StartZ=0 EndX=-90 EndY=36.8 EndZ=0
    g1: LineSegment StartX=-108 StartY=36.8 StartZ=0 EndX=-108 EndY=26.8 EndZ=0
    g2: LineSegment StartX=-108 StartY=26.8 StartZ=0 EndX=-90 EndY=26.8 EndZ=0
    g3: ArcOfCircle CenterX=-94 CenterY=31.8 CenterZ=0 NormalX=0 NormalY=0 NormalZ=1 AngleXU=0 Radius=6.40312 StartAngle=5.38713 EndAngle=7.17924
  constraints (13):
    c: Horizontal(g0)
    c: Coincident(g1,g0)
    c: Vertical(g1)
    c: Coincident(g2,g1)
    c: Horizontal(g2)
    c: DistanceX(g0,g0) = 18
    c: DistanceY(g1,g1) = 10
    c: Equal(g0,g2)
    c: DistanceX(g0,g-3) = 90
    c: DistanceY(g0,g-3) = 2.4
    c: Coincident(g3,g0)
    c: Coincident(g3,g2)
    c: DistanceX(g3,g0) = 4
FEATURE [PartDesign::Chamfer] Chamfer014
  Angle = 45
  Base = -> Pad011 [Edge80,Edge4,Edge7]
  BaseFeature = -> Pad011
  ChamferType = 0
  FlipDirection = false
  Refine = true
  Size = 1.9
  Size2 = 1
  SupportTransform = false
  Suppressed = false
  UseAllEdges = false
FEATURE [PartDesign::Pocket] Pocket006
  BaseFeature = -> Chamfer014
  Direction = (0,-1,2e-16)
  Length = 1.2
  Length2 = 5
  Profile = -> Sketch115
  ReferenceAxis = -> Sketch115 [N_Axis]
  Refine = true
  Suppressed = false
  Type = 0
FEATURE [Sketcher::SketchObject] Sketch116  label="Sketch116 - pieno per inserto M3 x 3 x 4,5"
  ArcFitTolerance = 1e-06
  AttachmentSupport = -> [Pocket006]
  ExternalGeometry = -> [Binder001]
  FullyConstrained = true
  MakeInternals = false
  MapMode = 5
  Placement = pos=(0,1.7e-15,0) rot=(0,0.707107,0.707107;3.14159rad)
  sketch-geometry (4):
    g0: Circle CenterX=43.2 CenterY=30.3 CenterZ=0 NormalX=0 NormalY=0 NormalZ=1 AngleXU=0 Radius=3.4
    g1: Circle CenterX=43.2 CenterY=12.1 CenterZ=0 NormalX=0 NormalY=0 NormalZ=1 AngleXU=0 Radius=3.4
    g2: Circle CenterX=18.6 CenterY=30.3 CenterZ=0 NormalX=0 NormalY=0 NormalZ=1 AngleXU=0 Radius=3.4
    g3: Circle CenterX=18.6 CenterY=12.1 CenterZ=0 NormalX=0 NormalY=0 NormalZ=1 AngleXU=0 Radius=3.4
  constraints (8):
    c: Diameter(g0) = 6.8
    c: Diameter(g1) = 6.8
    c: Diameter(g2) = 6.8
    c: Diameter(g3) = 6.8
    c: Coincident(g2,g-3)
    c: Coincident(g0,g-4)
    c: Coincident(g3,g-6)
    c: Coincident(g1,g-5)
FEATURE [PartDesign::Pad] Pad012
  BaseFeature = -> Pocket006
  Direction = (0,1,-2e-16)
  Length = 2.4
  Length2 = 10
  Profile = -> Sketch116
  ReferenceAxis = -> Sketch116 [N_Axis]
  Refine = true
  Suppressed = false
  Type = 0
FEATURE [PartDesign::Pocket] Pocket007
  BaseFeature = -> Pad012
  Direction = (0,-1,2e-16)
  Length = 0.6
  Length2 = 2.4
  Profile = -> Sketch117
  ReferenceAxis = -> Sketch117 [N_Axis]
  Refine = true
  Suppressed = false
  Type = 4
FEATURE [PartDesign::Pad] Pad013
  BaseFeature = -> Pocket007
  Direction = (0,-1,2e-16)
  Length = 1.6
  Length2 = 10
  Profile = -> Sketch118
  ReferenceAxis = -> Sketch118 [N_Axis]
  Refine = true
  Suppressed = false
  Type = 0
FEATURE [Sketcher::SketchObject] Sketch119
  ArcFitTolerance = 1e-06
  AttachmentSupport = -> [Pad013]
  ExternalGeometry = -> [Binder001]
  FullyConstrained = true
  MakeInternals = false
  MapMode = 5
  Placement = pos=(0,-3.6,0) rot=(1,0,0;1.5708rad)
  sketch-geometry (21):
    g0: LineSegment [constr] StartX=-82.8 StartY=3.2 StartZ=0 EndX=-82.8 EndY=39.2 EndZ=0
    g1: ArcOfCircle CenterX=-78.51 CenterY=34.8 CenterZ=0 NormalX=0 NormalY=0 NormalZ=1 AngleXU=0 Radius=3.5 StartAngle=4.71239 EndAngle=6.28319
    g2: ArcOfCircle CenterX=-78.51 CenterY=7.6 CenterZ=0 NormalX=0 NormalY=0 NormalZ=1 AngleXU=0 Radius=3.5 StartAngle=0 EndAngle=1.5708
    g3: ArcOfCircle CenterX=-5.6 CenterY=34.8 CenterZ=0 NormalX=0 NormalY=0 NormalZ=1 AngleXU=0 Radius=3.5 StartAngle=3.14159 EndAngle=4.71239
    g4: ArcOfCircle CenterX=-5.6 CenterY=7.6 CenterZ=0 NormalX=0 NormalY=0 NormalZ=1 AngleXU=0 Radius=3.5 StartAngle=1.5708 EndAngle=3.14159
    g5: LineSegment StartX=0 StartY=39.2 StartZ=0 EndX=0 EndY=31.3 EndZ=0
    g6: LineSegment StartX=0 StartY=39.2 StartZ=0 EndX=-9.1 EndY=39.2 EndZ=0
    g7: LineSegment StartX=0 StartY=3.2 StartZ=0 EndX=0 EndY=11.1 EndZ=0
    g8: LineSegment StartX=0 StartY=3.2 StartZ=0 EndX=-9.1 EndY=3.2 EndZ=0
    g9: LineSegment StartX=-82.8 StartY=3.2 StartZ=0 EndX=-75.01 EndY=3.2 EndZ=0
    g10: LineSegment StartX=-82.8 StartY=3.2 StartZ=0 EndX=-82.8 EndY=11.1 EndZ=0
    g11: LineSegment StartX=-82.8 StartY=39.2 StartZ=0 EndX=-82.8 EndY=31.3 EndZ=0
    g12: LineSegment StartX=-82.8 StartY=39.2 StartZ=0 EndX=-75.01 EndY=39.2 EndZ=0
    g13: LineSegment StartX=-82.8 StartY=31.3 StartZ=0 EndX=-78.51 EndY=31.3 EndZ=0
    g14: LineSegment StartX=-75.01 StartY=39.2 StartZ=0 EndX=-75.01 EndY=34.8 EndZ=0
    g15: LineSegment StartX=-82.8 StartY=11.1 StartZ=0 EndX=-78.51 EndY=11.1 EndZ=0
    g16: LineSegment StartX=-75.01 StartY=3.2 StartZ=0 EndX=-75.01 EndY=7.6 EndZ=0
    g17: LineSegment StartX=-9.1 StartY=39.2 StartZ=0 EndX=-9.1 EndY=34.8 EndZ=0
    g18: LineSegment StartX=0 StartY=31.3 StartZ=0 EndX=-5.6 EndY=31.3 EndZ=0
    g19: LineSegment StartX=0 StartY=11.1 StartZ=0 EndX=-5.6 EndY=11.1 EndZ=0
    g20: LineSegment StartX=-9.1 StartY=3.2 StartZ=0 EndX=-9.1 EndY=7.6 EndZ=0
  constraints (51):
    c: Coincident(g0,g-10)
    c: PointOnObject(g0,g-8)
    c: Vertical(g0)
    c: Coincident(g1,g-3)
    c: Coincident(g2,g-4)
    c: Coincident(g3,g-5)
    c: Coincident(g4,g-6)
    c: Radius(g4) = 3.5
    c: Radius(g3) = 3.5
    c: Radius(g1) = 3.5
    c: Radius(g2) = 3.5
    c: Coincident(g5,g-9)
    c: PointOnObject(g5,g-9)
    c: Coincident(g6,g5)
    c: PointOnObject(g6,g-8)
    c: Coincident(g7,g-9)
    c: PointOnObject(g7,g-9)
    c: Coincident(g8,g7)
    c: PointOnObject(g8,g-7)
    c: Coincident(g9,g0)
    c: PointOnObject(g9,g-7)
    c: Coincident(g10,g0)
    c: PointOnObject(g10,g0)
    c: Coincident(g11,g0)
    c: PointOnObject(g11,g0)
    c: Coincident(g12,g0)
    c: PointOnObject(g12,g-8)
    c: Coincident(g13,g11)
    c: Horizontal(g13)
    c: Coincident(g14,g12)
    c: Vertical(g14)
    c: Coincident(g15,g10)
    c: Horizontal(g15)
    c: Coincident(g16,g9)
    c: Vertical(g16)
    c: Coincident(g17,g6)
    c: Vertical(g17)
    c: Coincident(g18,g5)
    c: Horizontal(g18)
    c: Coincident(g19,g7)
    c: Horizontal(g19)
    c: Coincident(g20,g8)
    c: Vertical(g20)
    c: Tangent(g20,g4) = 1.5708
    c: Tangent(g4,g19) = -1.5708
    c: Tangent(g18,g3) = 1.5708
    c: Tangent(g3,g17) = -1.5708
    c: Tangent(g13,g1) = -1.5708
    c: Tangent(g1,g14) = 1.5708
    c: Tangent(g16,g2) = -1.5708
    c: Tangent(g2,g15) = 1.5708
FEATURE [PartDesign::Pocket] Pocket008
  BaseFeature = -> Pad013
  Direction = (0,1,-2e-16)
  Length = 1.6
  Length2 = 5
  Profile = -> Sketch119
  ReferenceAxis = -> Sketch119 [N_Axis]
  Refine = true
  Suppressed = false
  Type = 0
FEATURE [PartDesign::Pad] Pad017
  BaseFeature = -> Pocket008
  Direction = (0,-1,2e-16)
  Length = 1.6
  Length2 = 10
  Profile = -> Sketch123
  ReferenceAxis = -> Sketch123 [N_Axis]
  Refine = true
  Suppressed = false
  Type = 0
FEATURE [Sketcher::SketchObject] Sketch125
  ArcFitTolerance = 1e-06
  AttachmentSupport = -> [Pad017]
  ExternalGeometry = -> [Pad017]
  FullyConstrained = true
  MakeInternals = false
  MapMode = 5
  Placement = pos=(0,-3.6,8e-16) rot=(1,0,0;1.5708rad)
  sketch-geometry (20):
    g0: LineSegment StartX=-108 StartY=35.8 StartZ=0 EndX=-108 EndY=35 EndZ=0
    g1: LineSegment StartX=-108 StartY=35 StartZ=0 EndX=-97 EndY=35 EndZ=0
    g2: LineSegment StartX=-97 StartY=35 StartZ=0 EndX=-97 EndY=35.8 EndZ=0
    g3: LineSegment StartX=-97 StartY=35.8 StartZ=0 EndX=-108 EndY=35.8 EndZ=0
    g4: LineSegment StartX=-108 StartY=28.6 StartZ=0 EndX=-108 EndY=27.8 EndZ=0
    g5: LineSegment StartX=-108 StartY=27.8 StartZ=0 EndX=-97 EndY=27.8 EndZ=0
    g6: LineSegment StartX=-97 StartY=27.8 StartZ=0 EndX=-97 EndY=28.6 EndZ=0
    g7: LineSegment StartX=-97 StartY=28.6 StartZ=0 EndX=-108 EndY=28.6 EndZ=0
    g8: LineSegment StartX=-108 StartY=30.4 StartZ=0 EndX=-108 EndY=29.6 EndZ=0
    g9: LineSegment StartX=-108 StartY=29.6 StartZ=0 EndX=-97 EndY=29.6 EndZ=0
    g10: LineSegment StartX=-97 StartY=29.6 StartZ=0 EndX=-97 EndY=30.4 EndZ=0
    g11: LineSegment StartX=-97 StartY=30.4 StartZ=0 EndX=-108 EndY=30.4 EndZ=0
    g12: LineSegment StartX=-108 StartY=32.2 StartZ=0 EndX=-108 EndY=31.4 EndZ=0
    g13: LineSegment StartX=-108 StartY=31.4 StartZ=0 EndX=-97 EndY=31.4 EndZ=0
    g14: LineSegment StartX=-97 StartY=31.4 StartZ=0 EndX=-97 EndY=32.2 EndZ=0
    g15: LineSegment StartX=-97 StartY=32.2 StartZ=0 EndX=-108 EndY=32.2 EndZ=0
    g16: LineSegment StartX=-108 StartY=34 StartZ=0 EndX=-108 EndY=33.2 EndZ=0
    g17: LineSegment StartX=-108 StartY=33.2 StartZ=0 EndX=-97 EndY=33.2 EndZ=0
    g18: LineSegment StartX=-97 StartY=33.2 StartZ=0 EndX=-97 EndY=34 EndZ=0
    g19: LineSegment StartX=-97 StartY=34 StartZ=0 EndX=-108 EndY=34 EndZ=0
  constraints (55):
    c: Coincident(g1,g0)
    c: Horizontal(g1)
    c: Coincident(g2,g1)
    c: Vertical(g2)
    c: Coincident(g3,g2)
    c: Horizontal(g3)
    c: Coincident(g3,g0)
    c: DistanceX(g1,g1) = 11
    c: DistanceY(g2,g2) = 0.8
    c: Coincident(g5,g4)
    c: Horizontal(g5)
    c: Coincident(g6,g5)
    c: Vertical(g6)
    c: Coincident(g7,g6)
    c: Horizontal(g7)
    c: Coincident(g7,g4)
    c: Coincident(g9,g8)
    c: Horizontal(g9)
    c: Coincident(g10,g9)
    c: Vertical(g10)
    c: Coincident(g11,g10)
    c: Horizontal(g11)
    c: Coincident(g11,g8)
    c: Coincident(g13,g12)
    c: Horizontal(g13)
    c: Coincident(g14,g13)
    c: Vertical(g14)
    c: Coincident(g15,g14)
    c: Horizontal(g15)
    c: Coincident(g15,g12)
    c: Coincident(g17,g16)
    c: Horizontal(g17)
    c: Coincident(g18,g17)
    c: Vertical(g18)
    c: Coincident(g19,g18)
    c: Horizontal(g19)
    c: Coincident(g19,g16)
    c: Equal(g3,g19)
    c: Equal(g3,g15)
    c: Equal(g3,g11)
    c: Equal(g3,g7)
    c: Equal(g2,g18)
    c: Equal(g2,g14)
    c: Equal(g2,g10)
    c: Equal(g2,g6)
    c: DistanceY(g-4,g4) = 1
    c: DistanceY(g4,g8) = 1
    c: DistanceY(g8,g12) = 1
    c: DistanceY(g12,g16) = 1
    c: DistanceY(g16,g0) = 1
    c: Tangent(g0,g-5)
    c: Tangent(g16,g-5)
    c: Tangent(g12,g-5)
    c: Tangent(g8,g-5)
    c: Tangent(g4,g-5)
FEATURE [PartDesign::Chamfer] Chamfer009
  Angle = 45
  Base = -> Pad017 [Edge151,Edge154]
  BaseFeature = -> Pad017
  ChamferType = 1
  FlipDirection = false
  Refine = true
  Size = 1.5
  Size2 = 2.8
  SupportTransform = false
  Suppressed = false
  UseAllEdges = false
FEATURE [PartDesign::Pocket] Pocket009
  BaseFeature = -> Chamfer009
  Direction = (0,1,-2e-16)
  Length = 1
  Length2 = 5
  Profile = -> Sketch125
  ReferenceAxis = -> Sketch125 [N_Axis]
  Refine = true
  Suppressed = false
  Type = 0
FEATURE [PartDesign::Pad] Pad014
  BaseFeature = -> Pocket009
  Direction = (0,-1,2e-16)
  Length = 0.8
  Length2 = 10
  Profile = -> Sketch120
  ReferenceAxis = -> Sketch120 [N_Axis]
  Refine = true
  Suppressed = false
  Type = 0
FEATURE [Sketcher::SketchObject] Sketch124
  ArcFitTolerance = 1e-06
  AttachmentSupport = -> [Pad014]
  ExternalGeometry = -> [Binder001]
  FullyConstrained = true
  MakeInternals = false
  MapMode = 5
  Placement = pos=(0,-2.8,6e-16) rot=(1,0,0;1.5708rad)
  sketch-geometry (4):
    g0: LineSegment StartX=-129 StartY=39.2 StartZ=0 EndX=-131.599 EndY=31.2 EndZ=0
    g1: LineSegment StartX=-118 StartY=39.2 StartZ=0 EndX=-120.599 EndY=31.2 EndZ=0
    g2: LineSegment StartX=-129 StartY=39.2 StartZ=0 EndX=-118 EndY=39.2 EndZ=0
    g3: LineSegment StartX=-120.599 StartY=31.2 StartZ=0 EndX=-131.599 EndY=31.2 EndZ=0
  constraints (12):
    c: PointOnObject(g0,g-3)
    c: PointOnObject(g1,g-3)
    c: Parallel(g-4,g0)
    c: Parallel(g-4,g1)
    c: Coincident(g2,g0)
    c: Coincident(g2,g1)
    c: DistanceX(g2,g2) = 11
    c: DistanceY(g1,g1) = 8
    c: Coincident(g3,g1)
    c: Horizontal(g3)
    c: Coincident(g3,g0)
    c: DistanceX(g1,g-3) = 118
FEATURE [PartDesign::Pad] Pad018
  BaseFeature = -> Pad014
  Direction = (0,-1,2e-16)
  Length = 1.2
  Length2 = 10
  Profile = -> Sketch124
  ReferenceAxis = -> Sketch124 [N_Axis]
  Refine = true
  Suppressed = false
  Type = 0
FEATURE [Sketcher::SketchObject] Sketch126
  ArcFitTolerance = 1e-06
  AttachmentSupport = -> [Pad018]
  ExternalGeometry = -> [Pad018]
  FullyConstrained = true
  MakeInternals = false
  MapMode = 5
  Placement = pos=(0,-4,0) rot=(1,0,0;1.5708rad)
  sketch-geometry (8):
    g0: LineSegment StartX=-129.877 StartY=36.5 StartZ=0 EndX=-130.137 EndY=35.7 EndZ=0
    g1: LineSegment StartX=-130.69 StartY=34 StartZ=0 EndX=-130.95 EndY=33.2 EndZ=0
    g2: LineSegment StartX=-129.877 StartY=36.5 StartZ=0 EndX=-118.877 EndY=36.5 EndZ=0
    g3: LineSegment StartX=-130.137 StartY=35.7 StartZ=0 EndX=-119.137 EndY=35.7 EndZ=0
    g4: LineSegment StartX=-130.69 StartY=34 StartZ=0 EndX=-119.69 EndY=34 EndZ=0
    g5: LineSegment StartX=-130.95 StartY=33.2 StartZ=0 EndX=-119.95 EndY=33.2 EndZ=0
    g6: LineSegment StartX=-118.877 StartY=36.5 StartZ=0 EndX=-119.137 EndY=35.7 EndZ=0
    g7: LineSegment StartX=-119.69 StartY=34 StartZ=0 EndX=-119.95 EndY=33.2 EndZ=0
  constraints (20):
    c: Coincident(g2,g0)
    c: Horizontal(g2)
    c: Coincident(g3,g0)
    c: Horizontal(g3)
    c: Coincident(g4,g1)
    c: Horizontal(g4)
    c: Coincident(g5,g1)
    c: Horizontal(g5)
    c: Coincident(g6,g2)
    c: Coincident(g6,g3)
    c: Coincident(g7,g4)
    c: Coincident(g7,g5)
    c: Tangent(g0,g-4)
    c: Tangent(g6,g-5)
    c: Tangent(g1,g-4)
    c: Tangent(g7,g-5)
    c: DistanceY(g3,g2) = 0.8
    c: DistanceY(g5,g4) = 0.8
    c: DistanceY(g-6,g1) = 2
    c: DistanceY(g-6,g0) = 4.5
FEATURE [PartDesign::Chamfer] Chamfer008
  Angle = 45
  Base = -> Pad018 [Edge257]
  BaseFeature = -> Pad018
  ChamferType = 1
  FlipDirection = false
  Refine = true
  Size = 1
  Size2 = 6
  SupportTransform = false
  Suppressed = false
  UseAllEdges = false
FEATURE [PartDesign::Pocket] Pocket010
  BaseFeature = -> Chamfer008
  Direction = (0,1,-2e-16)
  Length = 1
  Length2 = 5
  Profile = -> Sketch126
  ReferenceAxis = -> Sketch126 [N_Axis]
  Refine = true
  Suppressed = false
  Type = 0
FEATURE [PartDesign::Pad] Pad015
  BaseFeature = -> Pocket010
  Direction = (0,-1,2e-16)
  Length = 2
  Length2 = 10
  Profile = -> Sketch121
  ReferenceAxis = -> Sketch121 [N_Axis]
  Refine = true
  Suppressed = false
  Type = 0
FEATURE [PartDesign::Pad] Pad016
  BaseFeature = -> Pad015
  Direction = (0,-1,2e-16)
  Length = 1.6
  Length2 = 10
  Profile = -> Sketch122
  ReferenceAxis = -> Sketch122 [N_Axis]
  Refine = true
  Suppressed = false
  Type = 0
FEATURE [Sketcher::SketchObject] Sketch129
  ArcFitTolerance = 1e-06
  AttachmentSupport = -> [Pad016]
  ExternalGeometry = -> [Binder001]
  FullyConstrained = true
  MakeInternals = false
  MapMode = 5
  Placement = pos=(0,-3.6,0) rot=(1,0,0;1.5708rad)
  sketch-geometry (12):
    g0: LineSegment [constr] StartX=-192.176 StartY=-3.18451 StartZ=0 EndX=-181.223 EndY=20.303 EndZ=0
    g1: LineSegment [constr] StartX=-202.765 StartY=20.303 StartZ=0 EndX=-181.223 EndY=20.303 EndZ=0
    g2: LineSegment StartX=-202.765 StartY=20.303 StartZ=0 EndX=-181.223 EndY=20.303 EndZ=0
    g3: LineSegment StartX=-192.176 StartY=-3.18451 StartZ=0 EndX=-196.804 EndY=-13.1107 EndZ=0
    g4: ArcOfCircle CenterX=-207.583 CenterY=4 CenterZ=0 NormalX=0 NormalY=0 NormalZ=1 AngleXU=0 Radius=17 StartAngle=5.84685 EndAngle=7.56663
    g5: ArcOfEllipse CenterX=-181.223 CenterY=8.55923 CenterZ=0 NormalX=0 NormalY=0 NormalZ=1 MajorRadius=23.4779 MinorRadius=11.7437 AngleXU=2e-16 StartAngle=4.71239 EndAngle=7.85398
    g6: LineSegment [constr] StartX=-157.745 StartY=8.55923 StartZ=0 EndX=-204.701 EndY=8.55923 EndZ=0
    g7: LineSegment [constr] StartX=-181.223 StartY=20.303 StartZ=0 EndX=-181.223 EndY=-3.18451 EndZ=0
    g8: GeomPoint [constr] X=-160.894 Y=8.55923 Z=0
    g9: GeomPoint [constr] X=-201.553 Y=8.55923 Z=0
    g10: ArcOfCircle CenterX=-181.223 CenterY=-20.3763 CenterZ=0 NormalX=0 NormalY=0 NormalZ=1 AngleXU=0 Radius=17.1918 StartAngle=1.57079 EndAngle=2.70526
    g11: GeomPoint [constr] X=-181.223 Y=-3.18451 Z=0
  constraints (23):
    c: Coincident(g0,g-5)
    c: Coincident(g1,g-6)
    c: Horizontal(g1)
    c: Coincident(g1,g0)
    c: Parallel(g0,g-4)
    c: Coincident(g2,g1)
    c: Coincident(g2,g0)
    c: Coincident(g3,g0)
    c: Equal(g4,g-5)
    c: Coincident(g4,g1)
    c: Coincident(g4,g0)
    c: InternalAlignment(g6-g9 -> g5) x4
    c: Vertical(g5,g0)
    c: Horizontal(g6)
    c: Coincident(g5,g0)
    c: DistanceX(g6,g-3) = 10.1
    c: Tangent(g10,g3) = -1.5708
    c: PointOnObject(g11,g10)
    c: Tangent(g5,g10,g11) = 1.5708
    c: Coincident(g10,g5)
    c: Coincident(g11,g7)
    c: Parallel(g3,g-4)
    c: Horizontal(g5,g0)
FEATURE [Sketcher::SketchObject] Sketch130
  ArcFitTolerance = 1e-06
  AttachmentOffset = pos=(0,0,-1.6) rot=(0,0,1;0rad)
  AttachmentSupport = -> [Pad016]
  ExternalGeometry = -> [Binder001]
  FullyConstrained = true
  MakeInternals = false
  MapMode = 5
  Placement = pos=(0,-2,-4e-16) rot=(1,0,0;1.5708rad)
  sketch-geometry (12):
    g0: LineSegment [constr] StartX=-192.176 StartY=-3.18451 StartZ=0 EndX=-181.223 EndY=20.303 EndZ=0
    g1: LineSegment [constr] StartX=-202.765 StartY=20.303 StartZ=0 EndX=-181.223 EndY=20.303 EndZ=0
    g2: LineSegment StartX=-202.765 StartY=20.303 StartZ=0 EndX=-181.223 EndY=20.303 EndZ=0
    g3: LineSegment StartX=-192.176 StartY=-3.18451 StartZ=0 EndX=-193.827 EndY=-6.72678 EndZ=0
    g4: ArcOfCircle CenterX=-207.583 CenterY=4 CenterZ=0 NormalX=0 NormalY=0 NormalZ=1 AngleXU=0 Radius=17 StartAngle=5.84685 EndAngle=7.56663
    g5: ArcOfEllipse CenterX=-181.223 CenterY=10.803 CenterZ=0 NormalX=0 NormalY=0 NormalZ=1 MajorRadius=14.4779 MinorRadius=9.5 AngleXU=0 StartAngle=4.71239 EndAngle=7.85398
    g6: LineSegment [constr] StartX=-166.745 StartY=10.803 StartZ=0 EndX=-195.701 EndY=10.803 EndZ=0
    g7: LineSegment [constr] StartX=-181.223 StartY=20.303 StartZ=0 EndX=-181.223 EndY=1.30297 EndZ=0
    g8: GeomPoint [constr] X=-170.298 Y=10.803 Z=0
    g9: GeomPoint [constr] X=-192.148 Y=10.803 Z=0
    g10: ArcOfCircle CenterX=-181.223 CenterY=-12.6042 CenterZ=0 NormalX=0 NormalY=0 NormalZ=1 AngleXU=0 Radius=13.9072 StartAngle=1.5708 EndAngle=2.70526
    g11: GeomPoint [constr] X=-181.223 Y=1.30297 Z=0
  constraints (23):
    c: Coincident(g0,g-5)
    c: Coincident(g1,g-6)
    c: Horizontal(g1)
    c: Coincident(g1,g0)
    c: Parallel(g0,g-4)
    c: Coincident(g2,g1)
    c: Coincident(g2,g0)
    c: Coincident(g3,g0)
    c: Equal(g4,g-5)
    c: Coincident(g4,g1)
    c: Coincident(g4,g0)
    c: InternalAlignment(g6-g9 -> g5) x4
    c: Vertical(g5,g0)
    c: Horizontal(g6)
    c: Coincident(g5,g0)
    c: DistanceX(g6,g-3) = 19.1
    c: Tangent(g10,g3) = -1.5708
    c: PointOnObject(g11,g10)
    c: Tangent(g5,g10,g11) = 1.5708
    c: Coincident(g10,g5)
    c: Coincident(g11,g7)
    c: Parallel(g3,g-4)
    c: DistanceY(g5,g0) = 19
FEATURE [Part::Part2DObjectPython] Clone2D001  label="Sketch130 (2D)"  # Draft 2D object (typed FeaturePython)
  Fuse = false
  Objects = -> [Sketch130]
  Placement = pos=(0,-2,-4e-16) rot=(1,0,0;1.5708rad)
  Scale = (1,1,1)
FEATURE [Sketcher::SketchObject] Sketch131
  ArcFitTolerance = 1e-06
  AttachmentOffset = pos=(0,0,-3.5) rot=(0,0,1;0rad)
  AttachmentSupport = -> [Pad016]
  ExternalGeometry = -> [Binder001]
  FullyConstrained = true
  MakeInternals = false
  MapMode = 5
  Placement = pos=(0,-0.1,-8e-16) rot=(1,0,0;1.5708rad)
  sketch-geometry (1):
    g0: GeomPoint X=-197.47 Y=8.55923 Z=0
  constraints (1):
    c: Symmetric(g-6,g-4,g0)
FEATURE [Sketcher::SketchObject] Sketch132
  ArcFitTolerance = 1e-06
  AttachmentSupport = -> [Pad016]
  ExternalGeometry = -> [Binder001]
  FullyConstrained = true
  MakeInternals = false
  MapMode = 5
  Placement = pos=(0,-3.6,0) rot=(1,0,0;1.5708rad)
  sketch-geometry (3):
    g0: LineSegment [constr] StartX=-215.42 StartY=-53.0314 StartZ=0 EndX=-167.782 EndY=-53.0314 EndZ=0
    g1: Circle CenterX=-191.282 CenterY=-53.0314 CenterZ=0 NormalX=0 NormalY=0 NormalZ=1 AngleXU=0 Radius=11.5
    g2: Circle CenterX=-191.282 CenterY=-53.0314 CenterZ=0 NormalX=0 NormalY=0 NormalZ=1 AngleXU=0 Radius=10.7
  constraints (8):
    c: Coincident(g0,g-3)
    c: PointOnObject(g0,g-4)
    c: Horizontal(g0)
    c: Diameter(g1) = 23
    c: PointOnObject(g1,g0)
    c: DistanceX(g1,g0) = 23.5
    c: Diameter(g2) = 21.4
    c: Coincident(g2,g1)
FEATURE [Part::Part2DObjectPython] ShapeString  # Draft 2D object (typed FeaturePython)
  FontFile = <path>
  Fuse = false
  Justification = 6
  JustificationReference = 0
  KeepLeftMargin = false
  MakeFace = true
  ObliqueAngle = 0
  Placement = pos=(-199,-3.6,-57.5) rot=(1,0,0;1.5708rad)
  ScaleToSize = true
  Size = 10
  String = AS
  Tracking = 0
FEATURE [Sketcher::SketchObject] Sketch133
  ArcFitTolerance = 1e-06
  AttachmentSupport = -> [Binder]
  ExternalGeometry = -> [Binder]
  FullyConstrained = true
  MakeInternals = false
  MapMode = 5
  Placement = pos=(0,9e-16,0) rot=(0,0.707107,0.707107;3.14159rad)
  sketch-geometry (30):
    g0: LineSegment StartX=0 StartY=39.2 StartZ=0 EndX=0 EndY=3.2 EndZ=0
    g1: LineSegment StartX=0 StartY=3.2 StartZ=0 EndX=82.8 EndY=3.2 EndZ=0
    g2: LineSegment StartX=82.8 StartY=3.2 StartZ=0 EndX=82.8 EndY=6.2 EndZ=0
    g3: LineSegment StartX=82.8 StartY=6.2 StartZ=0 EndX=91.752 EndY=6.2 EndZ=0
    g4: LineSegment StartX=0 StartY=39.2 StartZ=0 EndX=195.887 EndY=39.2 EndZ=0
    g5: LineSegment StartX=195.887 StartY=39.2 StartZ=0 EndX=202.765 EndY=20.303 EndZ=0
    g6: LineSegment StartX=192.333 StartY=24.9893 StartZ=0 EndX=196.467 EndY=26.4942 EndZ=0
    g7: LineSegment StartX=196.467 StartY=26.4942 StartZ=0 EndX=194.073 EndY=33.0721 EndZ=0
    g8: LineSegment StartX=194.073 StartY=33.0721 StartZ=0 EndX=189.939 EndY=31.5672 EndZ=0
    g9: LineSegment StartX=189.939 StartY=31.5672 StartZ=0 EndX=192.333 EndY=24.9893 EndZ=0
    g10: ArcOfCircle CenterX=107.6 CenterY=4 CenterZ=0 NormalX=0 NormalY=0 NormalZ=1 AngleXU=0 Radius=16 StartAngle=1.5708 EndAngle=3.00366
    g11: LineSegment StartX=107.6 StartY=20 StartZ=0 EndX=132.428 EndY=20 EndZ=0
    g12: ArcOfCircle [constr] CenterX=132.428 CenterY=4 CenterZ=0 NormalX=0 NormalY=0 NormalZ=1 AngleXU=0 Radius=16 StartAngle=0.314159 EndAngle=1.5708
    g13: LineSegment StartX=147.645 StartY=8.94427 StartZ=0 EndX=176.685 EndY=-80.4316 EndZ=0
    g14: LineSegment StartX=176.685 StartY=-80.4316 StartZ=0 EndX=215.932 EndY=-80.4316 EndZ=0
    g15: ArcOfCircle CenterX=207.583 CenterY=4 CenterZ=0 NormalX=0 NormalY=0 NormalZ=1 AngleXU=0 Radius=17 StartAngle=1.85815 EndAngle=3.57792
    g16: ArcOfCircle CenterX=184.801 CenterY=-67.3089 CenterZ=0 NormalX=0 NormalY=0 NormalZ=1 AngleXU=0 Radius=33.7833 StartAngle=5.88425 EndAngle=6.71952
    g17: LineSegment StartX=192.176 StartY=-3.18451 StartZ=0 EndX=215.42 EndY=-53.0314 EndZ=0
    g18: Circle CenterX=5.6 CenterY=34.8 CenterZ=0 NormalX=0 NormalY=0 NormalZ=1 AngleXU=0 Radius=1.8
    g19: Circle CenterX=5.6 CenterY=7.6 CenterZ=0 NormalX=0 NormalY=0 NormalZ=1 AngleXU=0 Radius=1.8
    g20: Circle CenterX=78.51 CenterY=34.8 CenterZ=0 NormalX=0 NormalY=0 NormalZ=1 AngleXU=0 Radius=1.8
    g21: Circle CenterX=78.51 CenterY=7.6 CenterZ=0 NormalX=0 NormalY=0 NormalZ=1 AngleXU=0 Radius=1.8
    g22: Circle CenterX=184.08 CenterY=34.8 CenterZ=0 NormalX=0 NormalY=0 NormalZ=1 AngleXU=0 Radius=1.8
    g23: Circle CenterX=179.305 CenterY=-76.8316 CenterZ=0 NormalX=0 NormalY=0 NormalZ=1 AngleXU=0 Radius=1.8
    g24: Circle CenterX=213.443 CenterY=-76.8316 CenterZ=0 NormalX=0 NormalY=0 NormalZ=1 AngleXU=0 Radius=1.8
    g25: Circle CenterX=19 CenterY=21.2 CenterZ=0 NormalX=0 NormalY=0 NormalZ=1 AngleXU=0 Radius=6.3
    g26: Circle CenterX=42 CenterY=21.2 CenterZ=0 NormalX=0 NormalY=0 NormalZ=1 AngleXU=0 Radius=6.3
    g27: Circle CenterX=65 CenterY=21.2 CenterZ=0 NormalX=0 NormalY=0 NormalZ=1 AngleXU=0 Radius=6.3
    g28: LineSegment StartX=132.428 StartY=20 StartZ=0 EndX=144.053 EndY=20 EndZ=0
    g29: LineSegment StartX=147.645 StartY=8.94427 StartZ=0 EndX=144.053 EndY=20 EndZ=0
  constraints (65):
    c: Coincident(g0,g-4)
    c: Coincident(g0,g-5)
    c: Coincident(g1,g0)
    c: Coincident(g1,g-6)
    c: Coincident(g2,g1)
    c: Coincident(g2,g-7)
    c: Coincident(g3,g2)
    c: Coincident(g3,g-8)
    c: Coincident(g4,g0)
    c: Coincident(g4,g-16)
    c: Coincident(g5,g4)
    c: Coincident(g5,g-16)
    c: Coincident(g6,g-20)
    c: Coincident(g6,g-21)
    c: Coincident(g7,g6)
    c: Coincident(g7,g-23)
    c: Coincident(g8,g7)
    c: Coincident(g8,g-22)
    c: Coincident(g9,g8)
    c: Coincident(g9,g6)
    c: Equal(g10,g-8)
    c: Coincident(g10,g3)
    c: Coincident(g10,g-9)
    c: Coincident(g11,g10)
    c: Coincident(g11,g-10)
    c: Equal(g12,g-10)
    c: Coincident(g12,g11)
    c: Coincident(g12,g-11)
    c: Coincident(g13,g12)
    c: Coincident(g13,g-12)
    c: Coincident(g14,g13)
    c: Coincident(g14,g-13)
    c: Equal(g15,g-15)
    c: Coincident(g15,g5)
    c: Coincident(g15,g-15)
    c: Equal(g16,g-13)
    c: Coincident(g16,g14)
    c: Coincident(g16,g-14)
    c: Coincident(g17,g15)
    c: Coincident(g17,g16)
    c: Equal(g18,g-28)
    c: Equal(g19,g-29)
    c: Equal(g20,g-26)
    c: Equal(g21,g-27)
    c: Equal(g22,g-17)
    c: Equal(g24,g-25)
    c: Equal(g23,g-24)
    c: Coincident(g23,g-24)
    c: Coincident(g24,g-25)
    c: Coincident(g22,g-17)
    c: Coincident(g20,g-26)
    c: Coincident(g21,g-27)
    c: Coincident(g18,g-28)
    c: Coincident(g19,g-29)
    c: Equal(g25,g-30)
    c: Equal(g26,g-31)
    c: Equal(g27,g-32)
    c: Coincident(g25,g-30)
    c: Coincident(g26,g-31)
    c: Coincident(g27,g-32)
    c: Parallel(g28,g11)
    c: Parallel(g29,g13)
    c: Coincident(g28,g11)
    c: Coincident(g29,g12)
    c: Coincident(g29,g28)
FEATURE [PartDesign::Pad] Pad019
  Direction = (0,1,-2e-16)
  Length = 2
  Length2 = 10
  Profile = -> Sketch133
  ReferenceAxis = -> Sketch133 [N_Axis]
  Refine = true
  Suppressed = false
  Type = 0
FEATURE [Sketcher::SketchObject] Sketch091  label="Sketch091 - forma anteriore"
  ArcFitTolerance = 1e-06
  AttachmentSupport = -> [Pad019]
  ExternalGeometry = -> [Binder]
  FullyConstrained = true
  MakeInternals = false
  MapMode = 5
  Placement = pos=(0,2,0) rot=(0,0.707107,0.707107;3.14159rad)
  sketch-geometry (12):
    g0: Circle CenterX=5.6 CenterY=34.8 CenterZ=0 NormalX=0 NormalY=0 NormalZ=1 AngleXU=0 Radius=1.8
    g1: Circle CenterX=5.6 CenterY=7.6 CenterZ=0 NormalX=0 NormalY=0 NormalZ=1 AngleXU=0 Radius=1.8
    g2: Circle CenterX=78.51 CenterY=34.8 CenterZ=0 NormalX=0 NormalY=0 NormalZ=1 AngleXU=0 Radius=1.8
    g3: Circle CenterX=78.51 CenterY=7.6 CenterZ=0 NormalX=0 NormalY=0 NormalZ=1 AngleXU=0 Radius=1.8
    g4: LineSegment StartX=0 StartY=39.2 StartZ=0 EndX=0 EndY=3.2 EndZ=0
    g5: LineSegment StartX=0 StartY=3.2 StartZ=0 EndX=82.8 EndY=3.2 EndZ=0
    g6: LineSegment StartX=82.8 StartY=3.2 StartZ=0 EndX=82.8 EndY=39.2 EndZ=0
    g7: LineSegment StartX=82.8 StartY=39.2 StartZ=0 EndX=0 EndY=39.2 EndZ=0
    g8: ArcOfCircle CenterX=19 CenterY=21.2 CenterZ=0 NormalX=0 NormalY=0 NormalZ=1 AngleXU=0 Radius=10 StartAngle=1.5708 EndAngle=4.71239
    g9: ArcOfCircle CenterX=65 CenterY=21.2 CenterZ=0 NormalX=0 NormalY=0 NormalZ=1 AngleXU=0 Radius=10 StartAngle=4.71239 EndAngle=7.85398
    g10: LineSegment StartX=19 StartY=31.2 StartZ=0 EndX=65 EndY=31.2 EndZ=0
    g11: LineSegment StartX=19 StartY=11.2 StartZ=0 EndX=65 EndY=11.2 EndZ=0
  constraints (25):
    c: Equal(g2,g-7)
    c: Equal(g3,g-8)
    c: Equal(g1,g-13)
    c: Equal(g0,g-12)
    c: Coincident(g0,g-12)
    c: Coincident(g1,g-13)
    c: Coincident(g3,g-8)
    c: Coincident(g2,g-7)
    c: Coincident(g4,g-4)
    c: Coincident(g4,g-5)
    c: Coincident(g5,g4)
    c: Coincident(g5,g-6)
    c: Coincident(g6,g5)
    c: PointOnObject(g6,g-3)
    c: Vertical(g6)
    c: Coincident(g7,g6)
    c: Coincident(g7,g4)
    c: Tangent(g8,g10) = 1.5708
    c: Tangent(g8,g11) = -1.5708
    c: Tangent(g9,g10) = 1.5708
    c: Tangent(g9,g11) = -1.5708
    c: Equal(g8,g9)
    c: Radius(g8) = 10
    c: Coincident(g8,g-11)
    c: Coincident(g9,g-9)
FEATURE [Sketcher::SketchObject] Sketch093  label="Sketch093 - scavi interni pulsanti"
  ArcFitTolerance = 1e-06
  AttachmentSupport = -> [Pad019]
  ExternalGeometry = -> [Binder]
  FullyConstrained = true
  MakeInternals = false
  MapMode = 5
  Placement = pos=(0,1.8e-15,0) rot=(1,0,0;1.5708rad)
  sketch-geometry (3):
    g0: Circle CenterX=-65 CenterY=21.2 CenterZ=0 NormalX=0 NormalY=0 NormalZ=1 AngleXU=0 Radius=7.3
    g1: Circle CenterX=-42 CenterY=21.2 CenterZ=0 NormalX=0 NormalY=0 NormalZ=1 AngleXU=0 Radius=7.3
    g2: Circle CenterX=-19 CenterY=21.2 CenterZ=0 NormalX=0 NormalY=0 NormalZ=1 AngleXU=0 Radius=7.3
  constraints (6):
    c: Coincident(g0,g-3)
    c: Coincident(g1,g-4)
    c: Coincident(g2,g-5)
    c: Diameter(g0) = 14.6
    c: Diameter(g1) = 14.6
    c: Diameter(g2) = 14.6
FEATURE [Sketcher::SketchObject] Sketch094  label="Sketch094 - forma centrale"
  ArcFitTolerance = 1e-06
  AttachmentSupport = -> [Pad019]
  ExternalGeometry = -> [Binder]
  FullyConstrained = true
  MakeInternals = false
  MapMode = 5
  Placement = pos=(0,2,0) rot=(0,0.707107,0.707107;3.14159rad)
  sketch-geometry (4):
    g0: LineSegment StartX=137.815 StartY=39.2 StartZ=0 EndX=142.655 EndY=24.303 EndZ=0
    g1: LineSegment StartX=110.815 StartY=24.303 StartZ=0 EndX=142.655 EndY=24.303 EndZ=0
    g2: LineSegment StartX=137.815 StartY=39.2 StartZ=0 EndX=110.815 EndY=39.2 EndZ=0
    g3: ArcOfCircle CenterX=92.2534 CenterY=31.7515 CenterZ=0 NormalX=0 NormalY=0 NormalZ=1 AngleXU=0 Radius=20 StartAngle=5.90156 EndAngle=6.66481
  constraints (12):
    c: PointOnObject(g0,g-3)
    c: Tangent(g0,g-5)
    c: Horizontal(g1)
    c: Coincident(g1,g0)
    c: Coincident(g2,g0)
    c: PointOnObject(g2,g-3)
    c: DistanceX(g2,g2) = 27
    c: Vertical(g1,g2)
    c: Coincident(g3,g2)
    c: Radius(g3) = 20
    c: Coincident(g3,g1)
    c: DistanceY(g-6,g0) = 4
FEATURE [Sketcher::SketchObject] Sketch095  label="Sketch095 - forma posteriore"
  ArcFitTolerance = 1e-06
  AttachmentSupport = -> [Pad019]
  ExternalGeometry = -> [Binder]
  FullyConstrained = true
  MakeInternals = false
  MapMode = 5
  Placement = pos=(0,2,0) rot=(0,0.707107,0.707107;3.14159rad)
  sketch-geometry (15):
    g0: LineSegment StartX=137.815 StartY=39.2 StartZ=0 EndX=143.955 EndY=20.303 EndZ=0
    g1: LineSegment StartX=143.955 StartY=20.303 StartZ=0 EndX=190.141 EndY=20.303 EndZ=0
    g2: ArcOfCircle CenterX=184.08 CenterY=34.8 CenterZ=0 NormalX=0 NormalY=0 NormalZ=1 AngleXU=0 Radius=3.5 StartAngle=3.49066 EndAngle=4.71239
    g3: LineSegment StartX=180.791 StartY=33.6029 StartZ=0 EndX=178.754 EndY=39.2 EndZ=0
    g4: LineSegment StartX=184.08 StartY=31.3 StartZ=0 EndX=186.139 EndY=31.3 EndZ=0
    g5: LineSegment StartX=190.141 StartY=20.303 StartZ=0 EndX=186.139 EndY=31.3 EndZ=0
    g6: LineSegment StartX=137.815 StartY=39.2 StartZ=0 EndX=156.815 EndY=39.2 EndZ=0
    g7: LineSegment StartX=178.754 StartY=39.2 StartZ=0 EndX=168.815 EndY=39.2 EndZ=0
    g8: LineSegment StartX=156.815 StartY=31.2 StartZ=0 EndX=168.815 EndY=31.2 EndZ=0
    g9: ArcOfCircle CenterX=176.411 CenterY=35.2 CenterZ=0 NormalX=0 NormalY=0 NormalZ=1 AngleXU=0 Radius=20 StartAngle=2.94023 EndAngle=3.34295
    g10: ArcOfCircle CenterX=188.411 CenterY=35.2 CenterZ=0 NormalX=0 NormalY=0 NormalZ=1 AngleXU=0 Radius=20 StartAngle=2.94023 EndAngle=3.34295
    g11: LineSegment StartX=157.815 StartY=39.2 StartZ=0 EndX=167.815 EndY=39.2 EndZ=0
    g12: LineSegment StartX=157.436 StartY=36.2 StartZ=0 EndX=167.436 EndY=36.2 EndZ=0
    g13: ArcOfCircle CenterX=177.411 CenterY=35.2 CenterZ=0 NormalX=0 NormalY=0 NormalZ=1 AngleXU=0 Radius=20 StartAngle=2.94023 EndAngle=3.09157
    g14: ArcOfCircle CenterX=187.411 CenterY=35.2 CenterZ=0 NormalX=0 NormalY=0 NormalZ=1 AngleXU=0 Radius=20 StartAngle=2.94023 EndAngle=3.09157
  constraints (46):
    c: PointOnObject(g0,g-3)
    c: Tangent(g0,g-6)
    c: Coincident(g1,g0)
    c: Horizontal(g1)
    c: Radius(g2) = 3.5
    c: Coincident(g2,g-5)
    c: PointOnObject(g3,g-3)
    c: Parallel(g3,g-4)
    c: Tangent(g3,g2) = 1.5708
    c: Horizontal(g4)
    c: Tangent(g4,g2) = -1.5708
    c: Coincident(g5,g1)
    c: Parallel(g5,g-4)
    c: Coincident(g5,g4)
    c: DistanceX(g4,g-8) = 3.8
    c: Coincident(g6,g0)
    c: PointOnObject(g6,g-3)
    c: Coincident(g7,g3)
    c: PointOnObject(g7,g-3)
    c: Horizontal(g8)
    c: DistanceX(g6,g7) = 12
    c: Vertical(g8,g6)
    c: Vertical(g7,g8)
    c: DistanceY(g8,g6) = 8
    c: Coincident(g9,g8)
    c: Coincident(g9,g6)
    c: Coincident(g10,g7)
    c: Coincident(g10,g8)
    c: Radius(g9) = 20
    c: Radius(g10) = 20
    c: PointOnObject(g11,g-3)
    c: PointOnObject(g11,g-3)
    c: DistanceX(g11,g11) = 10
    c: DistanceX(g6,g11) = 1
    c: Horizontal(g12)
    c: Equal(g12,g11)
    c: DistanceY(g12,g11) = 3
    c: Coincident(g13,g11)
    c: Coincident(g13,g12)
    c: Radius(g13) = 20
    c: Coincident(g14,g11)
    c: Coincident(g14,g12)
    c: Radius(g14) = 20
    c: DistanceX(g0,g6) = 19
    c: Horizontal(g9,g13)
    c: Horizontal(g0,g-4)
FEATURE [Sketcher::SketchObject] Sketch096  label="Sketch096 - forma impugnatura"
  ArcFitTolerance = 1e-06
  AttachmentSupport = -> [Pad019]
  ExternalGeometry = -> [Binder]
  FullyConstrained = true
  MakeInternals = false
  MapMode = 5
  Placement = pos=(0,2,0) rot=(0,0.707107,0.707107;3.14159rad)
  sketch-geometry (8):
    g0: LineSegment StartX=176.685 StartY=-80.4316 StartZ=0 EndX=143.955 EndY=20.303 EndZ=0
    g1: LineSegment StartX=176.685 StartY=-80.4316 StartZ=0 EndX=215.932 EndY=-80.4316 EndZ=0
    g2: Circle CenterX=179.305 CenterY=-76.8316 CenterZ=0 NormalX=0 NormalY=0 NormalZ=1 AngleXU=0 Radius=3
    g3: Circle CenterX=213.443 CenterY=-76.8316 CenterZ=0 NormalX=0 NormalY=0 NormalZ=1 AngleXU=0 Radius=3
    g4: LineSegment StartX=143.955 StartY=20.303 StartZ=0 EndX=202.765 EndY=20.303 EndZ=0
    g5: LineSegment StartX=215.42 StartY=-53.0314 StartZ=0 EndX=192.176 EndY=-3.18451 EndZ=0
    g6: ArcOfCircle CenterX=184.801 CenterY=-67.3089 CenterZ=0 NormalX=0 NormalY=0 NormalZ=1 AngleXU=0 Radius=33.7833 StartAngle=5.88425 EndAngle=6.71952
    g7: ArcOfCircle CenterX=207.583 CenterY=4 CenterZ=0 NormalX=0 NormalY=0 NormalZ=1 AngleXU=0 Radius=17 StartAngle=1.85815 EndAngle=3.57792
  constraints (19):
    c: Coincident(g0,g-4)
    c: PointOnObject(g0,g-3)
    c: Horizontal(g0,g-7)
    c: Coincident(g1,g0)
    c: Coincident(g1,g-5)
    c: Diameter(g2) = 6
    c: Diameter(g3) = 6
    c: Coincident(g2,g-9)
    c: Coincident(g3,g-10)
    c: Coincident(g4,g0)
    c: Coincident(g5,g-6)
    c: Coincident(g6,g1)
    c: Coincident(g6,g5)
    c: Equal(g-5,g6)
    c: Coincident(g5,g-7)
    c: Coincident(g4,g-7)
    c: Tangent(g7,g-7)
    c: Coincident(g7,g4)
    c: Coincident(g7,g5)
FEATURE [Sketcher::SketchObject] Sketch097
  ArcFitTolerance = 1e-06
  AttachmentSupport = -> [Pad019]
  ExternalGeometry = -> [Binder]
  FullyConstrained = true
  MakeInternals = false
  MapMode = 5
  Placement = pos=(0,2,0) rot=(0,0.707107,0.707107;3.14159rad)
  sketch-geometry (4):
    g0: LineSegment StartX=90 StartY=36.8 StartZ=0 EndX=108 EndY=36.8 EndZ=0
    g1: LineSegment StartX=108 StartY=36.8 StartZ=0 EndX=108 EndY=26.8 EndZ=0
    g2: LineSegment StartX=108 StartY=26.8 StartZ=0 EndX=90 EndY=26.8 EndZ=0
    g3: ArcOfCircle CenterX=94 CenterY=31.8 CenterZ=0 NormalX=0 NormalY=0 NormalZ=1 AngleXU=0 Radius=6.40312 StartAngle=2.24554 EndAngle=4.03765
  constraints (13):
    c: Horizontal(g0)
    c: Coincident(g1,g0)
    c: Vertical(g1)
    c: DistanceX(g0,g0) = 18
    c: DistanceY(g1,g1) = 10
    c: Coincident(g2,g1)
    c: Horizontal(g2)
    c: Equal(g2,g0)
    c: DistanceY(g0,g-3) = 2.4
    c: Coincident(g3,g0)
    c: Coincident(g3,g2)
    c: DistanceX(g2,g3) = 4
    c: DistanceX(g-3,g0) = 90
FEATURE [PartDesign::Chamfer] Chamfer015
  Angle = 45
  Base = -> Pad019 [Edge19,Edge22,Edge79]
  BaseFeature = -> Pad019
  ChamferType = 0
  FlipDirection = false
  Refine = true
  Size = 1.9
  Size2 = 1
  SupportTransform = false
  Suppressed = false
  UseAllEdges = false
FEATURE [PartDesign::Pocket] Pocket002
  BaseFeature = -> Chamfer015
  Direction = (0,1,-2e-16)
  Length = 1.2
  Length2 = 5
  Profile = -> Sketch093
  ReferenceAxis = -> Sketch093 [N_Axis]
  Refine = true
  Suppressed = false
  Type = 0
FEATURE [PartDesign::Pad] Pad005
  BaseFeature = -> Pocket002
  Direction = (0,1,-2e-16)
  Length = 1.6
  Length2 = 10
  Profile = -> Sketch091
  ReferenceAxis = -> Sketch091 [N_Axis]
  Refine = true
  Suppressed = false
  Type = 0
FEATURE [Sketcher::SketchObject] Sketch092  label="Sketch092 - scavi per viti anteriori"
  ArcFitTolerance = 1e-06
  AttachmentSupport = -> [Pad005]
  ExternalGeometry = -> [Binder]
  FullyConstrained = true
  MakeInternals = false
  MapMode = 5
  Placement = pos=(0,3.6,0) rot=(0,0.707107,0.707107;3.14159rad)
  sketch-geometry (20):
    g0: ArcOfCircle CenterX=5.6 CenterY=7.6 CenterZ=0 NormalX=0 NormalY=0 NormalZ=1 AngleXU=0 Radius=3.5 StartAngle=0 EndAngle=1.5708
    g1: ArcOfCircle CenterX=5.6 CenterY=34.8 CenterZ=0 NormalX=0 NormalY=0 NormalZ=1 AngleXU=0 Radius=3.5 StartAngle=4.71239 EndAngle=6.28319
    g2: ArcOfCircle CenterX=78.51 CenterY=34.8 CenterZ=0 NormalX=0 NormalY=0 NormalZ=1 AngleXU=0 Radius=3.5 StartAngle=3.14159 EndAngle=4.71239
    g3: ArcOfCircle CenterX=78.51 CenterY=7.6 CenterZ=0 NormalX=0 NormalY=0 NormalZ=1 AngleXU=0 Radius=3.5 StartAngle=1.5708 EndAngle=3.14159
    g4: LineSegment StartX=0 StartY=3.2 StartZ=0 EndX=0 EndY=11.1 EndZ=0
    g5: LineSegment StartX=0 StartY=11.1 StartZ=0 EndX=5.6 EndY=11.1 EndZ=0
    g6: LineSegment StartX=0 StartY=3.2 StartZ=0 EndX=9.1 EndY=3.2 EndZ=0
    g7: LineSegment StartX=9.1 StartY=3.2 StartZ=0 EndX=9.1 EndY=7.6 EndZ=0
    g8: LineSegment StartX=0 StartY=39.2 StartZ=0 EndX=0 EndY=31.3 EndZ=0
    g9: LineSegment StartX=0 StartY=31.3 StartZ=0 EndX=5.6 EndY=31.3 EndZ=0
    g10: LineSegment StartX=0 StartY=39.2 StartZ=0 EndX=9.1 EndY=39.2 EndZ=0
    g11: LineSegment StartX=9.1 StartY=39.2 StartZ=0 EndX=9.1 EndY=34.8 EndZ=0
    g12: LineSegment StartX=82.8 StartY=39.2 StartZ=0 EndX=75.01 EndY=39.2 EndZ=0
    g13: LineSegment StartX=82.8 StartY=39.2 StartZ=0 EndX=82.8 EndY=31.3 EndZ=0
    g14: LineSegment StartX=82.8 StartY=31.3 StartZ=0 EndX=78.51 EndY=31.3 EndZ=0
    g15: LineSegment StartX=82.8 StartY=3.2 StartZ=0 EndX=75.01 EndY=3.2 EndZ=0
    g16: LineSegment StartX=75.01 StartY=3.2 StartZ=0 EndX=75.01 EndY=7.6 EndZ=0
    g17: LineSegment StartX=82.8 StartY=3.2 StartZ=0 EndX=82.8 EndY=11.1 EndZ=0
    g18: LineSegment StartX=82.8 StartY=11.1 StartZ=0 EndX=78.51 EndY=11.1 EndZ=0
    g19: LineSegment StartX=75.01 StartY=39.2 StartZ=0 EndX=75.01 EndY=34.8 EndZ=0
  constraints (48):
    c: Radius(g0) = 3.5
    c: Coincident(g0,g-10)
    c: Radius(g1) = 3.5
    c: Coincident(g1,g-9)
    c: Radius(g2) = 3.5
    c: Coincident(g2,g-8)
    c: Radius(g3) = 3.5
    c: Coincident(g3,g-7)
    c: Coincident(g4,g-5)
    c: PointOnObject(g4,g-4)
    c: Coincident(g5,g4)
    c: Horizontal(g5)
    c: Coincident(g6,g4)
    c: PointOnObject(g6,g-5)
    c: Coincident(g7,g6)
    c: Vertical(g7)
    c: Coincident(g8,g-4)
    c: PointOnObject(g8,g-4)
    c: Coincident(g9,g8)
    c: Horizontal(g9)
    c: Coincident(g10,g8)
    c: PointOnObject(g10,g-3)
    c: Coincident(g11,g10)
    c: Vertical(g11)
    c: PointOnObject(g12,g-3)
    c: PointOnObject(g12,g-3)
    c: Coincident(g13,g12)
    c: Vertical(g13)
    c: Coincident(g14,g13)
    c: Horizontal(g14)
    c: Coincident(g15,g-6)
    c: PointOnObject(g15,g-5)
    c: Coincident(g16,g15)
    c: Vertical(g16)
    c: Coincident(g17,g15)
    c: Coincident(g18,g17)
    c: Horizontal(g18)
    c: Tangent(g3,g18) = -1.5708
    c: Tangent(g16,g3) = 1.5708
    c: Coincident(g19,g12)
    c: Vertical(g19)
    c: Tangent(g2,g19) = -1.5708
    c: Tangent(g2,g14) = 1.5708
    c: Tangent(g0,g7) = -1.5708
    c: Tangent(g0,g5) = 1.5708
    c: Tangent(g9,g1) = -1.5708
    c: Tangent(g1,g11) = 1.5708
    c: Tangent(g17,g13)
FEATURE [PartDesign::Pocket] Pocket001
  BaseFeature = -> Pad005
  Direction = (0,-1,2e-16)
  Length = 1.6
  Length2 = 5
  Profile = -> Sketch092
  ReferenceAxis = -> Sketch092 [N_Axis]
  Refine = true
  Suppressed = false
  Type = 0
FEATURE [PartDesign::Pad] Pad006
  BaseFeature = -> Pocket001
  Direction = (0,1,-2e-16)
  Length = 0.8
  Length2 = 10
  Profile = -> Sketch094
  ReferenceAxis = -> Sketch094 [N_Axis]
  Refine = true
  Suppressed = false
  Type = 0
FEATURE [PartDesign::Pad] Pad007
  BaseFeature = -> Pad006
  Direction = (0,1,-2e-16)
  Length = 2
  Length2 = 10
  Profile = -> Sketch095
  ReferenceAxis = -> Sketch095 [N_Axis]
  Refine = true
  Suppressed = false
  Type = 0
FEATURE [PartDesign::Pad] Pad008  label="Pad008 - forma impugnatura"
  BaseFeature = -> Pad007
  Direction = (0,1,-2e-16)
  Length = 1.6
  Length2 = 10
  Profile = -> Sketch096
  ReferenceAxis = -> Sketch096 [N_Axis]
  Refine = true
  Suppressed = false
  Type = 0
FEATURE [PartDesign::Pad] Pad009
  BaseFeature = -> Pad008
  Direction = (0,1,-2e-16)
  Length = 1.6
  Length2 = 10
  Profile = -> Sketch097
  ReferenceAxis = -> Sketch097 [N_Axis]
  Refine = true
  Suppressed = false
  Type = 0
FEATURE [Sketcher::SketchObject] Sketch098
  ArcFitTolerance = 1e-06
  AttachmentSupport = -> [Pad006]
  ExternalGeometry = -> [Binder]
  FullyConstrained = true
  MakeInternals = false
  MapMode = 5
  Placement = pos=(0,2.8,-7e-16) rot=(0,0.707107,0.707107;3.14159rad)
  sketch-geometry (4):
    g0: LineSegment StartX=118 StartY=39.2 StartZ=0 EndX=129 EndY=39.2 EndZ=0
    g1: LineSegment StartX=120.599 StartY=31.2 StartZ=0 EndX=131.599 EndY=31.2 EndZ=0
    g2: LineSegment StartX=129 StartY=39.2 StartZ=0 EndX=131.599 EndY=31.2 EndZ=0
    g3: LineSegment StartX=118 StartY=39.2 StartZ=0 EndX=120.599 EndY=31.2 EndZ=0
  constraints (12):
    c: PointOnObject(g0,g-3)
    c: PointOnObject(g0,g-3)
    c: DistanceX(g0,g0) = 11
    c: Horizontal(g1)
    c: Equal(g1,g0)
    c: Coincident(g2,g0)
    c: Coincident(g3,g0)
    c: Parallel(g-4,g2)
    c: Coincident(g1,g2)
    c: Coincident(g1,g3)
    c: DistanceY(g1,g0) = 8
    c: DistanceX(g-3,g0) = 118
FEATURE [Sketcher::SketchObject] Sketch099
  ArcFitTolerance = 1e-06
  AttachmentSupport = -> [Pad008]
  ExternalGeometry = -> [Binder]
  FullyConstrained = true
  MakeInternals = false
  MapMode = 5
  Placement = pos=(0,3.6,0) rot=(0,0.707107,0.707107;3.14159rad)
  sketch-geometry (13):
    g0: LineSegment StartX=192.176 StartY=-3.18451 StartZ=0 EndX=196.804 EndY=-13.1108 EndZ=0
    g1: LineSegment [constr] StartX=202.765 StartY=20.303 StartZ=0 EndX=181.223 EndY=20.303 EndZ=0
    g2: LineSegment [constr] StartX=181.223 StartY=20.303 StartZ=0 EndX=181.223 EndY=-3.18451 EndZ=0
    g3: ArcOfCircle CenterX=181.223 CenterY=-20.3764 CenterZ=0 NormalX=0 NormalY=0 NormalZ=1 AngleXU=0 Radius=17.1918 StartAngle=0.436332 EndAngle=1.57079
    g4: ArcOfEllipse CenterX=181.223 CenterY=8.55923 CenterZ=0 NormalX=0 NormalY=0 NormalZ=1 MajorRadius=23.4779 MinorRadius=11.7437 AngleXU=0 StartAngle=1.5708 EndAngle=4.71239
    g5: LineSegment [constr] StartX=204.701 StartY=8.55923 StartZ=0 EndX=157.745 EndY=8.55923 EndZ=0
    g6: LineSegment [constr] StartX=181.223 StartY=20.303 StartZ=0 EndX=181.223 EndY=-3.18451 EndZ=0
    g7: GeomPoint [constr] X=201.553 Y=8.55923 Z=0
    g8: GeomPoint [constr] X=160.894 Y=8.55923 Z=0
    g9: GeomPoint [constr] X=181.223 Y=-3.18451 Z=0
    g10: LineSegment StartX=181.223 StartY=20.303 StartZ=0 EndX=202.765 EndY=20.303 EndZ=0
    g11: ArcOfCircle CenterX=207.583 CenterY=4 CenterZ=0 NormalX=0 NormalY=0 NormalZ=1 AngleXU=0 Radius=17 StartAngle=1.85815 EndAngle=3.57792
    g12: LineSegment [constr] StartX=172.411 StartY=39.2 StartZ=0 EndX=192.176 EndY=-3.18451 EndZ=0
  constraints (27):
    c: Coincident(g1,g-7)
    c: Horizontal(g1)
    c: Coincident(g2,g1)
    c: Vertical(g2)
    c: Horizontal(g2,g0)
    c: Coincident(g3,g0)
    c: Coincident(g3,g2)
    c: InternalAlignment(g5-g8 -> g4) x4
    c: Horizontal(g5)
    c: PointOnObject(g4,g2)
    c: Coincident(g4,g1)
    c: DistanceX(g-3,g5) = 10.1
    c: Coincident(g4,g2)
    c: Tangent(g3,g-5)
    c: PointOnObject(g9,g4)
    c: PointOnObject(g9,g3)
    c: Tangent(g4,g3,g9) = 1.5708
    c: Coincident(g10,g1)
    c: Coincident(g10,g1)
    c: Equal(g11,g-4)
    c: Coincident(g11,g1)
    c: Coincident(g11,g0)
    c: PointOnObject(g12,g-6)
    c: PointOnObject(g1,g12)
    c: Tangent(g12,g-5) = -1.5708
    c: Tangent(g0,g-5) = -1.5708
    c: Horizontal(g9,g12)
FEATURE [Sketcher::SketchObject] Sketch106  label="Sketch106 - smusso impuniatura interno"
  ArcFitTolerance = 1e-06
  AttachmentSupport = -> [Pad008]
  ExternalGeometry = -> [Pad008]
  FullyConstrained = true
  MakeInternals = false
  MapMode = 5
  Placement = pos=(0,-1.586e-13,-80.4316) rot=(1,0,0;3.14159rad)
  sketch-geometry (9):
    g0: LineSegment StartX=-176.685 StartY=-3.6 StartZ=0 EndX=-176.685 EndY=-5.8e-15 EndZ=0
    g1: LineSegment [constr] StartX=-176.685 StartY=-7.37e-14 StartZ=0 EndX=-176.685 EndY=-5.8e-15 EndZ=0
    g2: LineSegment [constr] StartX=-186.685 StartY=-3.6 StartZ=0 EndX=-186.685 EndY=-5.8e-15 EndZ=0
    g3: ArcOfEllipse CenterX=-186.685 CenterY=-5.8e-15 CenterZ=0 NormalX=0 NormalY=0 NormalZ=1 MajorRadius=10 MinorRadius=3.6 AngleXU=-3.14159 StartAngle=1.5708 EndAngle=3.14159
    g4: LineSegment [constr] StartX=-196.685 StartY=-5.9e-15 StartZ=0 EndX=-176.685 EndY=-5.9e-15 EndZ=0
    g5: LineSegment [constr] StartX=-186.685 StartY=-3.6 StartZ=0 EndX=-186.685 EndY=3.6 EndZ=0
    g6: GeomPoint [constr] X=-196.015 Y=-7.9e-15 Z=0
    g7: GeomPoint [constr] X=-177.356 Y=-4.9e-15 Z=0
    g8: LineSegment StartX=-176.685 StartY=-3.6 StartZ=0 EndX=-186.685 EndY=-3.6 EndZ=0
  constraints (15):
    c: PointOnObject(g2,g-3)
    c: Coincident(g1,g-5)
    c: DistanceY(g1,g1) = 0
    c: Coincident(g0,g1)
    c: DistanceX(g2,g-5) = 10
    c: Vertical(g2)
    c: Horizontal(g2,g0)
    c: InternalAlignment(g4-g7 -> g3) x4
    c: Coincident(g3,g2)
    c: Horizontal(g4)
    c: Coincident(g3,g0)
    c: Tangent(g0,g-5) = 1.5708
    c: Coincident(g3,g2)
    c: Coincident(g8,g0)
    c: Coincident(g8,g2)
FEATURE [Sketcher::SketchObject] Sketch107  label="Sketch107 - smusso impugnatura esterno"
  ArcFitTolerance = 1e-06
  AttachmentSupport = -> [Pad008]
  ExternalGeometry = -> [Pad008]
  FullyConstrained = true
  MakeInternals = false
  MapMode = 5
  Placement = pos=(0,-1.586e-13,-80.4316) rot=(1,0,0;3.14159rad)
  sketch-geometry (9):
    g0: LineSegment [constr] StartX=-215.932 StartY=-1.416e-13 StartZ=0 EndX=-215.932 EndY=-1.417e-13 EndZ=0
    g1: LineSegment StartX=-215.932 StartY=-3.6 StartZ=0 EndX=-215.932 EndY=-1.417e-13 EndZ=0
    g2: LineSegment StartX=-215.932 StartY=-3.6 StartZ=0 EndX=-205.932 EndY=-3.6 EndZ=0
    g3: LineSegment [constr] StartX=-205.932 StartY=-3.6 StartZ=0 EndX=-205.932 EndY=-1.417e-13 EndZ=0
    g4: ArcOfEllipse CenterX=-205.932 CenterY=-1.417e-13 CenterZ=0 NormalX=0 NormalY=0 NormalZ=1 MajorRadius=10 MinorRadius=3.6 AngleXU=3.14159 StartAngle=-2.66e-14 EndAngle=1.5708
    g5: LineSegment [constr] StartX=-215.932 StartY=-1.416e-13 StartZ=0 EndX=-195.932 EndY=-1.416e-13 EndZ=0
    g6: LineSegment [constr] StartX=-205.932 StartY=-3.6 StartZ=0 EndX=-205.932 EndY=3.6 EndZ=0
    g7: GeomPoint [constr] X=-215.262 Y=-1.28e-13 Z=0
    g8: GeomPoint [constr] X=-196.602 Y=-1.551e-13 Z=0
  constraints (16):
    c: Coincident(g0,g-6)
    c: PointOnObject(g0,g-6)
    c: DistanceY(g0,g0) = 0
    c: Coincident(g1,g-6)
    c: Coincident(g1,g0)
    c: Tangent(g2,g-3)
    c: DistanceX(g2,g2) = 10
    c: Coincident(g3,g2)
    c: Vertical(g3)
    c: Horizontal(g3,g0)
    c: InternalAlignment(g5-g8 -> g4) x4
    c: Coincident(g4,g3)
    c: Horizontal(g5)
    c: Coincident(g4,g0)
    c: Coincident(g4,g2)
    c: PointOnObject(g2,g1)
FEATURE [Sketcher::SketchObject] Sketch108
  ArcFitTolerance = 1e-06
  AttachmentOffset = pos=(0,0,-1.6) rot=(0,0,1;0rad)
  AttachmentSupport = -> [Pad008]
  ExternalGeometry = -> [Binder]
  FullyConstrained = true
  MakeInternals = false
  MapMode = 5
  Placement = pos=(0,2,4e-16) rot=(0,0.707107,0.707107;3.14159rad)
  sketch-geometry (14):
    g0: LineSegment StartX=192.176 StartY=-3.18451 StartZ=0 EndX=193.827 EndY=-6.72678 EndZ=0
    g1: LineSegment [constr] StartX=202.765 StartY=20.303 StartZ=0 EndX=181.223 EndY=20.303 EndZ=0
    g2: LineSegment [constr] StartX=181.223 StartY=20.303 StartZ=0 EndX=181.223 EndY=1.30297 EndZ=0
    g3: ArcOfCircle CenterX=181.223 CenterY=-12.6042 CenterZ=0 NormalX=0 NormalY=0 NormalZ=1 AngleXU=0 Radius=13.9072 StartAngle=0.436332 EndAngle=1.5708
    g4: ArcOfEllipse CenterX=181.223 CenterY=10.803 CenterZ=0 NormalX=0 NormalY=0 NormalZ=1 MajorRadius=14.4779 MinorRadius=9.5 AngleXU=0 StartAngle=1.5708 EndAngle=4.71239
    g5: LineSegment [constr] StartX=195.701 StartY=10.803 StartZ=0 EndX=166.745 EndY=10.803 EndZ=0
    g6: LineSegment [constr] StartX=181.223 StartY=20.303 StartZ=0 EndX=181.223 EndY=1.30297 EndZ=0
    g7: GeomPoint [constr] X=192.148 Y=10.803 Z=0
    g8: GeomPoint [constr] X=170.298 Y=10.803 Z=0
    g9: LineSegment StartX=181.223 StartY=20.303 StartZ=0 EndX=202.765 EndY=20.303 EndZ=0
    g10: ArcOfCircle CenterX=207.583 CenterY=4 CenterZ=0 NormalX=0 NormalY=0 NormalZ=1 AngleXU=0 Radius=17 StartAngle=1.85815 EndAngle=3.57792
    g11: LineSegment [constr] StartX=172.411 StartY=39.2 StartZ=0 EndX=192.176 EndY=-3.18451 EndZ=0
    g12: GeomPoint [constr] X=181.223 Y=1.30297 Z=0
    g13: GeomPoint [constr] X=181.223 Y=1.30297 Z=0
  constraints (28):
    c: Coincident(g1,g-7)
    c: Horizontal(g1)
    c: Coincident(g2,g1)
    c: Vertical(g2)
    c: Coincident(g3,g2)
    c: InternalAlignment(g5-g8 -> g4) x4
    c: Horizontal(g5)
    c: PointOnObject(g4,g2)
    c: Coincident(g4,g1)
    c: DistanceX(g-3,g5) = 19.1
    c: Coincident(g4,g2)
    c: Coincident(g9,g1)
    c: Coincident(g9,g1)
    c: Coincident(g10,g1)
    c: Coincident(g10,g0)
    c: PointOnObject(g11,g-6)
    c: PointOnObject(g1,g11)
    c: DistanceY(g2,g1) = 19
    c: Coincident(g10,g-4)
    c: PointOnObject(g12,g4)
    c: PointOnObject(g12,g3)
    c: Tangent(g11,g-5) = -1.5708
    c: Tangent(g0,g-5) = -1.5708
    c: Tangent(g3,g0) = 1.5708
    c: PointOnObject(g13,g4)
    c: PointOnObject(g13,g3)
    c: Tangent(g4,g3,g13) = 1.5708
    c: Horizontal(g11,g0)
FEATURE [Part::Part2DObjectPython] Clone2D  label="Sketch108 (2D)"  # Draft 2D object (typed FeaturePython)
  Fuse = false
  Objects = -> [Sketch108]
  Placement = pos=(0,2,4e-16) rot=(0,0.707107,0.707107;3.14159rad)
  Scale = (1,1,1)
FEATURE [Sketcher::SketchObject] Sketch109
  ArcFitTolerance = 1e-06
  AttachmentOffset = pos=(0,0,-3.5) rot=(0,0,1;0rad)
  AttachmentSupport = -> [Pad008]
  ExternalGeometry = -> [Binder]
  FullyConstrained = true
  MakeInternals = false
  MapMode = 5
  Placement = pos=(0,0.1,8e-16) rot=(0,0.707107,0.707107;3.14159rad)
  sketch-geometry (1):
    g0: GeomPoint X=197.47 Y=8.55923 Z=0
  constraints (1):
    c: Symmetric(g-7,g-5,g0)
FEATURE [PartDesign::Chamfer] Chamfer005
  Angle = 45
  Base = -> Pad009 [Edge215,Edge212]
  BaseFeature = -> Pad009
  ChamferType = 1
  FlipDirection = false
  Refine = true
  Size = 1.5
  Size2 = 2.8
  SupportTransform = false
  Suppressed = false
  UseAllEdges = false
FEATURE [Sketcher::SketchObject] Sketch111
  ArcFitTolerance = 1e-06
  AttachmentSupport = -> [Pad009]
  ExternalGeometry = -> [Pad009]
  FullyConstrained = true
  MakeInternals = false
  MapMode = 5
  Placement = pos=(0,3.6,-8e-16) rot=(0,0.707107,0.707107;3.14159rad)
  sketch-geometry (21):
    g0: LineSegment [constr] StartX=97 StartY=36.8 StartZ=0 EndX=97 EndY=26.8 EndZ=0
    g1: LineSegment StartX=97 StartY=28.6 StartZ=0 EndX=97 EndY=27.8 EndZ=0
    g2: LineSegment StartX=97 StartY=27.8 StartZ=0 EndX=108 EndY=27.8 EndZ=0
    g3: LineSegment StartX=108 StartY=27.8 StartZ=0 EndX=108 EndY=28.6 EndZ=0
    g4: LineSegment StartX=108 StartY=28.6 StartZ=0 EndX=97 EndY=28.6 EndZ=0
    g5: LineSegment StartX=97 StartY=35.8 StartZ=0 EndX=97 EndY=35 EndZ=0
    g6: LineSegment StartX=97 StartY=35 StartZ=0 EndX=108 EndY=35 EndZ=0
    g7: LineSegment StartX=108 StartY=35 StartZ=0 EndX=108 EndY=35.8 EndZ=0
    g8: LineSegment StartX=108 StartY=35.8 StartZ=0 EndX=97 EndY=35.8 EndZ=0
    g9: LineSegment StartX=97 StartY=30.4 StartZ=0 EndX=97 EndY=29.6 EndZ=0
    g10: LineSegment StartX=97 StartY=29.6 StartZ=0 EndX=108 EndY=29.6 EndZ=0
    g11: LineSegment StartX=108 StartY=29.6 StartZ=0 EndX=108 EndY=30.4 EndZ=0
    g12: LineSegment StartX=108 StartY=30.4 StartZ=0 EndX=97 EndY=30.4 EndZ=0
    g13: LineSegment StartX=97 StartY=34 StartZ=0 EndX=97 EndY=33.2 EndZ=0
    g14: LineSegment StartX=97 StartY=33.2 StartZ=0 EndX=108 EndY=33.2 EndZ=0
    g15: LineSegment StartX=108 StartY=33.2 StartZ=0 EndX=108 EndY=34 EndZ=0
    g16: LineSegment StartX=108 StartY=34 StartZ=0 EndX=97 EndY=34 EndZ=0
    g17: LineSegment StartX=97 StartY=32.2 StartZ=0 EndX=97 EndY=31.4 EndZ=0
    g18: LineSegment StartX=97 StartY=31.4 StartZ=0 EndX=108 EndY=31.4 EndZ=0
    g19: LineSegment StartX=108 StartY=31.4 StartZ=0 EndX=108 EndY=32.2 EndZ=0
    g20: LineSegment StartX=108 StartY=32.2 StartZ=0 EndX=97 EndY=32.2 EndZ=0
  constraints (54):
    c: Vertical(g0)
    c: PointOnObject(g0,g-3)
    c: PointOnObject(g0,g-4)
    c: DistanceX(g0,g-5) = 11
    c: Coincident(g1,g2)
    c: Coincident(g2,g3)
    c: Coincident(g3,g4)
    c: Coincident(g4,g1)
    c: Horizontal(g2)
    c: Horizontal(g4)
    c: Tangent(g1,g0)
    c: Tangent(g3,g-5)
    c: DistanceY(g2,g3) = 0.8
    c: Coincident(g5,g6)
    c: Coincident(g6,g7)
    c: Coincident(g7,g8)
    c: Coincident(g8,g5)
    c: Horizontal(g6)
    c: Horizontal(g8)
    c: DistanceY(g6,g7) = 0.8
    c: Coincident(g9,g10)
    c: Coincident(g10,g11)
    c: Coincident(g11,g12)
    c: Coincident(g12,g9)
    c: Horizontal(g10)
    c: Horizontal(g12)
    c: DistanceY(g10,g11) = 0.8
    c: Tangent(g5,g0)
    c: Tangent(g7,g-5)
    c: Tangent(g9,g0)
    c: Tangent(g11,g-5)
    c: Coincident(g13,g14)
    c: Coincident(g14,g15)
    c: Coincident(g15,g16)
    c: Coincident(g16,g13)
    c: Horizontal(g14)
    c: Horizontal(g16)
    c: DistanceY(g14,g15) = 0.8
    c: Tangent(g13,g0)
    c: Tangent(g15,g-5)
    c: Coincident(g17,g18)
    c: Coincident(g18,g19)
    c: Coincident(g19,g20)
    c: Coincident(g20,g17)
    c: Horizontal(g18)
    c: Horizontal(g20)
    c: DistanceY(g18,g19) = 0.8
    c: Tangent(g17,g0)
    c: Tangent(g19,g-5)
    c: DistanceY(g1,g9) = 1
    c: DistanceY(g9,g17) = 1
    c: DistanceY(g17,g13) = 1
    c: DistanceY(g13,g5) = 1
    c: DistanceY(g0,g1) = 1
FEATURE [PartDesign::Pocket] Pocket004
  BaseFeature = -> Chamfer005
  Direction = (0,-1,2e-16)
  Length = 1
  Length2 = 5
  Profile = -> Sketch111
  ReferenceAxis = -> Sketch111 [N_Axis]
  Refine = true
  Suppressed = false
  Type = 0
FEATURE [PartDesign::Pad] Pad010
  BaseFeature = -> Pocket004
  Direction = (0,1,-2e-16)
  Length = 1.2
  Length2 = 10
  Profile = -> Sketch098
  ReferenceAxis = -> Sketch098 [N_Axis]
  Refine = true
  Suppressed = false
  Type = 0
FEATURE [PartDesign::Chamfer] Chamfer006
  Angle = 45
  Base = -> Pad010 [Edge291]
  BaseFeature = -> Pad010
  ChamferType = 1
  FlipDirection = false
  Refine = true
  Size = 1
  Size2 = 6
  SupportTransform = false
  Suppressed = false
  UseAllEdges = false
FEATURE [Sketcher::SketchObject] Sketch110
  ArcFitTolerance = 1e-06
  AttachmentSupport = -> [Pad010]
  ExternalGeometry = -> [Sketch098]
  FullyConstrained = true
  MakeInternals = false
  MapMode = 5
  Placement = pos=(0,4,-9e-16) rot=(0,0.707107,0.707107;3.14159rad)
  sketch-geometry (8):
    g0: LineSegment StartX=119.69 StartY=34 StartZ=0 EndX=130.69 EndY=34 EndZ=0
    g1: LineSegment StartX=119.95 StartY=33.2 StartZ=0 EndX=130.95 EndY=33.2 EndZ=0
    g2: LineSegment StartX=119.137 StartY=35.7 StartZ=0 EndX=130.137 EndY=35.7 EndZ=0
    g3: LineSegment StartX=118.877 StartY=36.5 StartZ=0 EndX=129.877 EndY=36.5 EndZ=0
    g4: LineSegment StartX=118.877 StartY=36.5 StartZ=0 EndX=119.137 EndY=35.7 EndZ=0
    g5: LineSegment StartX=129.877 StartY=36.5 StartZ=0 EndX=130.137 EndY=35.7 EndZ=0
    g6: LineSegment StartX=119.69 StartY=34 StartZ=0 EndX=119.95 EndY=33.2 EndZ=0
    g7: LineSegment StartX=130.69 StartY=34 StartZ=0 EndX=130.95 EndY=33.2 EndZ=0
  constraints (24):
    c: Horizontal(g0)
    c: Horizontal(g1)
    c: Horizontal(g2)
    c: Horizontal(g3)
    c: Equal(g1,g-5)
    c: Equal(g0,g-5)
    c: Equal(g2,g-5)
    c: Equal(g3,g-5)
    c: PointOnObject(g0,g-3)
    c: PointOnObject(g1,g-3)
    c: PointOnObject(g2,g-3)
    c: PointOnObject(g3,g-3)
    c: Coincident(g4,g3)
    c: Coincident(g4,g2)
    c: Coincident(g5,g3)
    c: Coincident(g5,g2)
    c: Coincident(g6,g0)
    c: Coincident(g6,g1)
    c: Coincident(g7,g0)
    c: Coincident(g7,g1)
    c: DistanceY(g1,g0) = 0.8
    c: DistanceY(g2,g3) = 0.8
    c: DistanceY(g-5,g1) = 2
    c: DistanceY(g-5,g2) = 4.5
FEATURE [PartDesign::Pocket] Pocket003
  BaseFeature = -> Chamfer006
  Direction = (0,-1,2e-16)
  Length = 1
  Length2 = 5
  Profile = -> Sketch110
  ReferenceAxis = -> Sketch110 [N_Axis]
  Refine = true
  Suppressed = false
  Type = 0
FEATURE [PartDesign::SubtractivePipe] SubtractivePipe
  AuxilleryCurvelinear = true
  AuxillerySpineTangent = false
  BaseFeature = -> Pocket003
  Binormal = (0,0,0)
  Mode = 0
  Profile = -> Sketch106
  Refine = true
  Spine = -> Pad008 [Edge215]
  SpineTangent = false
  Suppressed = false
  Transformation = 0
  Transition = 0
FEATURE [PartDesign::SubtractivePipe] SubtractivePipe001
  AuxilleryCurvelinear = true
  AuxillerySpineTangent = false
  BaseFeature = -> SubtractivePipe
  Binormal = (0,0,0)
  Mode = 0
  Profile = -> Sketch107
  Refine = true
  Spine = -> Pad008 [Edge213,Edge216,Edge210]
  SpineTangent = false
  Suppressed = false
  Transformation = 0
  Transition = 0
FEATURE [PartDesign::SubtractiveLoft] SubtractiveLoft
  BaseFeature = -> SubtractivePipe001
  Closed = false
  Profile = -> Sketch099
  Refine = true
  Ruled = false
  Sections = -> [Sketch108]
  Suppressed = false
FEATURE [PartDesign::SubtractiveLoft] SubtractiveLoft001
  BaseFeature = -> SubtractiveLoft
  Closed = false
  Profile = -> Clone2D
  Refine = true
  Ruled = false
  Sections = -> [Sketch109]
  Suppressed = false
FEATURE [Sketcher::SketchObject] Sketch112
  ArcFitTolerance = 1e-06
  AttachmentSupport = -> [Pad008]
  ExternalGeometry = -> [Binder]
  FullyConstrained = true
  MakeInternals = false
  MapMode = 5
  Placement = pos=(0,3.6,0) rot=(0,0.707107,0.707107;3.14159rad)
  sketch-geometry (4):
    g0: LineSegment [constr] StartX=167.782 StartY=-53.0314 StartZ=0 EndX=215.42 EndY=-53.0314 EndZ=0
    g1: GeomPoint [constr] X=191.282 Y=-53.0314 Z=0
    g2: Circle CenterX=191.282 CenterY=-53.0314 CenterZ=0 NormalX=0 NormalY=0 NormalZ=1 AngleXU=0 Radius=11.5
    g3: Circle CenterX=191.282 CenterY=-53.0314 CenterZ=0 NormalX=0 NormalY=0 NormalZ=1 AngleXU=0 Radius=10.7
  constraints (9):
    c: Horizontal(g0)
    c: PointOnObject(g0,g-3)
    c: Diameter(g2) = 23
    c: Coincident(g2,g1)
    c: Diameter(g3) = 21.4
    c: Coincident(g3,g1)
    c: DistanceX(g0,g1) = 23.5
    c: PointOnObject(g1,g0)
    c: Coincident(g0,g-4)
FEATURE [PartDesign::Chamfer] Chamfer016
  Angle = 45
  Base = -> SubtractiveLoft001 [Edge118,Edge117,Edge119,Edge120,Edge109]
  BaseFeature = -> SubtractiveLoft001
  ChamferType = 0
  FlipDirection = false
  Refine = true
  Size = 1.5
  Size2 = 1
  SupportTransform = false
  Suppressed = false
  UseAllEdges = false
FEATURE [PartDesign::Chamfer] Chamfer017
  Angle = 45
  Base = -> Chamfer016 [Edge15]
  BaseFeature = -> Chamfer016
  ChamferType = 0
  FlipDirection = false
  Refine = true
  Size = 1.6
  Size2 = 1
  SupportTransform = false
  Suppressed = false
  UseAllEdges = false
FEATURE [PartDesign::Chamfer] Chamfer018
  Angle = 45
  Base = -> Chamfer017 [Edge10]
  BaseFeature = -> Chamfer017
  ChamferType = 0
  FlipDirection = false
  Refine = true
  Size = 3.5
  Size2 = 1
  SupportTransform = false
  Suppressed = false
  UseAllEdges = false
FEATURE [PartDesign::Chamfer] Chamfer019
  Angle = 45
  Base = -> Chamfer018 [Edge94]
  BaseFeature = -> Chamfer018
  ChamferType = 0
  FlipDirection = false
  Refine = true
  Size = 1.9
  Size2 = 1
  SupportTransform = false
  Suppressed = false
  UseAllEdges = false
FEATURE [PartDesign::Fillet] Fillet009
  Base = -> Chamfer019 [Edge83]
  BaseFeature = -> Chamfer019
  Radius = 1.1
  Refine = true
  SupportTransform = false
  Suppressed = false
  UseAllEdges = false
FEATURE [PartDesign::Fillet] Fillet010
  Base = -> Fillet009 [Edge76]
  BaseFeature = -> Fillet009
  Radius = 1.9
  Refine = true
  SupportTransform = false
  Suppressed = false
  UseAllEdges = false
FEATURE [PartDesign::Pocket] Pocket005
  BaseFeature = -> Fillet010
  Direction = (0,-1,2e-16)
  Length = 0.8
  Length2 = 5
  Profile = -> Sketch112
  ReferenceAxis = -> Sketch112 [N_Axis]
  Refine = true
  Suppressed = false
  Type = 0
FEATURE [Part::Part2DObjectPython] ShapeString001  # Draft 2D object (typed FeaturePython)
  FontFile = <path>
  Fuse = false
  Justification = 6
  JustificationReference = 0
  KeepLeftMargin = false
  MakeFace = true
  ObliqueAngle = 0
  Placement = pos=(-183.5,3.6,-57.5) rot=(0,0.707107,0.707107;3.14159rad)
  ScaleToSize = true
  Size = 10
  String = AS
  Tracking = 0
FEATURE [PartDesign::Pocket] Pocket013
  BaseFeature = -> Pocket005
  Direction = (-1e-16,-1,2e-16)
  Length = 1
  Length2 = 5
  Profile = -> ShapeString001
  ReferenceAxis = -> ShapeString001 [N_Axis]
  Refine = true
  Suppressed = false
  Type = 0
FEATURE [PartDesign::Body] Body006  label="lato SX"
  AllowCompound = false
  Group = -> [Binder,Pad019,Chamfer015,Pocket002,Sketch133,Sketch091,Pad005,Sketch092,Pocket001,Sketch093,Sketch094,Pad006,Sketch095,Pad007,Sketch096,Pad008,Sketch097,Pad009,Chamfer005,Pocket004,Sketch098,Pad010,Chamfer006,Pocket003,SubtractivePipe,SubtractivePipe001,Sketch099,Sketch106,Sketch107,Sketch108,Clone2D,Sketch109,SubtractiveLoft,SubtractiveLoft001,Sketch110,Sketch111,Sketch112,Chamfer016,Chamfer017,+7 more]
  Origin = -> Origin006
  Tip = -> Pocket013
FEATURE [PartDesign::Pad] Pad020
  Direction = (0,-1,2e-16)
  Length = 25.2
  Length2 = 10
  Midplane = true
  Placement = pos=(0,0,0) rot=(1,0,0;1.5708rad)
  Profile = -> Sketch021
  ReferenceAxis = -> Sketch021 [N_Axis]
  Refine = true
  Suppressed = false
  Type = 0
FEATURE [PartDesign::Body] Body001  label="perno fermo rumble e driver solenoide"
  AllowCompound = false
  Group = -> [Sketch021,Pad020]
  Origin = -> Origin001
  Tip = -> Pad020
FEATURE [PartDesign::Pad] Pad021
  Direction = (0,-1,2e-16)
  Length = 16.8
  Length2 = 10
  Midplane = true
  Placement = pos=(0,0,0) rot=(1,0,0;1.5708rad)
  Profile = -> Sketch061
  ReferenceAxis = -> Sketch061 [N_Axis]
  Refine = true
  Suppressed = false
  Type = 0
FEATURE [PartDesign::Pocket] Pocket014
  BaseFeature = -> Pad021
  Direction = (0,1,-2e-16)
  Length = 12.8
  Length2 = 5
  Midplane = true
  Placement = pos=(0,0,0) rot=(1,0,0;1.5708rad)
  Profile = -> Sketch062
  ReferenceAxis = -> Sketch062 [N_Axis]
  Refine = true
  Suppressed = false
  Type = 0
FEATURE [PartDesign::Pad] Pad022
  BaseFeature = -> Pocket014
  Direction = (0,-1,2e-16)
  Length = 7.6
  Length2 = 10
  Midplane = true
  Placement = pos=(0,0,0) rot=(1,0,0;1.5708rad)
  Profile = -> Sketch063
  ReferenceAxis = -> Sketch063 [N_Axis]
  Refine = true
  Suppressed = false
  Type = 0
FEATURE [PartDesign::Body] Body003  label="blocco switch"
  AllowCompound = false
  Group = -> [Sketch061,Sketch062,Sketch063,Pad021,Pocket014,Pad022]
  Origin = -> Origin003
  Tip = -> Pad022
FEATURE [PartDesign::Pad] Pad024
  Direction = (0,-1,2e-16)
  Length = 17
  Length2 = 10
  Midplane = true
  Placement = pos=(0,0,0) rot=(1,0,0;1.5708rad)
  Profile = -> Sketch045
  ReferenceAxis = -> Sketch045 [N_Axis]
  Refine = true
  Suppressed = false
  Type = 0
FEATURE [PartDesign::Pocket] Pocket015
  BaseFeature = -> Pad024
  Direction = (-1,0,0)
  Length = 8
  Length2 = 5
  Placement = pos=(0,0,0) rot=(1,0,0;1.5708rad)
  Profile = -> Sketch047
  ReferenceAxis = -> Sketch047 [N_Axis]
  Refine = true
  Reversed = true
  Suppressed = false
  Type = 0
FEATURE [PartDesign::Pocket] Pocket016
  BaseFeature = -> Pocket015
  Direction = (-1,0,0)
  Length = 1
  Length2 = 5
  Placement = pos=(0,0,0) rot=(1,0,0;1.5708rad)
  Profile = -> Sketch046
  ReferenceAxis = -> Sketch046 [N_Axis]
  Refine = true
  Reversed = true
  Suppressed = false
  Type = 0
FEATURE [PartDesign::Pocket] Pocket017
  BaseFeature = -> Pocket016
  Direction = (0,1,-2e-16)
  Length = 17
  Length2 = 5
  Midplane = true
  Placement = pos=(0,0,0) rot=(1,0,0;1.5708rad)
  Profile = -> Sketch048
  ReferenceAxis = -> Sketch048 [N_Axis]
  Refine = true
  Suppressed = false
  Type = 0
FEATURE [PartDesign::Pad] Pad025
  BaseFeature = -> Pocket017
  Direction = (0,-1,2e-16)
  Length = 17
  Length2 = 10
  Midplane = true
  Placement = pos=(0,0,0) rot=(1,0,0;1.5708rad)
  Profile = -> Sketch049
  ReferenceAxis = -> Sketch049 [N_Axis]
  Refine = true
  Suppressed = false
  Type = 0
FEATURE [PartDesign::Pad] Pad026
  BaseFeature = -> Pad025
  Direction = (0,-1,2e-16)
  Length = 17
  Length2 = 10
  Midplane = true
  Placement = pos=(0,0,0) rot=(1,0,0;1.5708rad)
  Profile = -> Sketch066
  ReferenceAxis = -> Sketch066 [N_Axis]
  Refine = true
  Suppressed = false
  Type = 0
FEATURE [PartDesign::Pad] Pad027
  BaseFeature = -> Pad026
  Direction = (0,-1,2e-16)
  Length = 5
  Length2 = 10
  Midplane = true
  Placement = pos=(0,0,0) rot=(1,0,0;1.5708rad)
  Profile = -> Sketch064
  ReferenceAxis = -> Sketch064 [N_Axis]
  Refine = true
  Suppressed = false
  Type = 0
FEATURE [PartDesign::Pad] Pad028
  BaseFeature = -> Pad027
  Direction = (1,0,0)
  Length = 1
  Length2 = 10
  Placement = pos=(0,0,0) rot=(1,0,0;1.5708rad)
  Profile = -> Sketch068
  ReferenceAxis = -> Sketch068 [N_Axis]
  Refine = true
  Reversed = true
  Suppressed = false
  Type = 0
FEATURE [PartDesign::Chamfer] Chamfer020
  Angle = 45
  Base = -> Pad028 [Edge73,Edge75,Edge78,Edge77]
  BaseFeature = -> Pad028
  ChamferType = 0
  FlipDirection = false
  Placement = pos=(0,0,0) rot=(1,0,0;1.5708rad)
  Refine = true
  Size = 0.5
  Size2 = 1
  SupportTransform = false
  Suppressed = false
  UseAllEdges = false
FEATURE [PartDesign::Body] Body002  label="supporto per neopixel"
  AllowCompound = false
  Group = -> [Sketch045,Sketch047,Sketch046,Sketch048,Sketch049,Sketch066,Sketch064,Sketch068,Pad024,Pocket015,Pocket016,Pocket017,Pad025,Pad026,Pad027,Pad028,Chamfer020]
  Origin = -> Origin002
  Tip = -> Chamfer020
FEATURE [Sketcher::SketchObject] Sketch134  label="perno fermo rumble002"
  ArcFitTolerance = 1e-06
  AttachmentSupport = -> [XZ_Plane008]
  FullyConstrained = true
  MakeInternals = false
  MapMode = 5
  Placement = pos=(0,0,0) rot=(1,0,0;1.5708rad)
  sketch-geometry (16):
    g0: LineSegment StartX=0 StartY=0.45 StartZ=0 EndX=0 EndY=1.55 EndZ=0
    g1: LineSegment StartX=0.45 StartY=2 StartZ=0 EndX=1.55 EndY=2 EndZ=0
    g2: LineSegment StartX=2 StartY=1.55 StartZ=0 EndX=2 EndY=0.45 EndZ=0
    g3: LineSegment StartX=1.55 StartY=0 StartZ=0 EndX=0.45 EndY=0 EndZ=0
    g4: ArcOfCircle [constr] CenterX=0.45 CenterY=1.55 CenterZ=0 NormalX=0 NormalY=0 NormalZ=1 AngleXU=0 Radius=0.45 StartAngle=1.5708 EndAngle=3.14159
    g5: GeomPoint [constr] X=0 Y=2 Z=0
    g6: LineSegment StartX=0.45 StartY=2 StartZ=0 EndX=0 EndY=1.55 EndZ=0
    g7: ArcOfCircle [constr] CenterX=1.55 CenterY=1.55 CenterZ=0 NormalX=0 NormalY=0 NormalZ=1 AngleXU=0 Radius=0.45 StartAngle=0 EndAngle=1.5708
    g8: GeomPoint [constr] X=2 Y=2 Z=0
    g9: LineSegment StartX=2 StartY=1.55 StartZ=0 EndX=1.55 EndY=2 EndZ=0
    g10: ArcOfCircle [constr] CenterX=1.55 CenterY=0.45 CenterZ=0 NormalX=0 NormalY=0 NormalZ=1 AngleXU=0 Radius=0.45 StartAngle=4.71239 EndAngle=6.28319
    g11: GeomPoint [constr] X=2 Y=0 Z=0
    g12: LineSegment StartX=1.55 StartY=0 StartZ=0 EndX=2 EndY=0.45 EndZ=0
    g13: ArcOfCircle [constr] CenterX=0.45 CenterY=0.45 CenterZ=0 NormalX=0 NormalY=0 NormalZ=1 AngleXU=0 Radius=0.45 StartAngle=3.14159 EndAngle=4.71239
    g14: GeomPoint [constr] X=0 Y=0 Z=0
    g15: LineSegment StartX=0 StartY=0.45 StartZ=0 EndX=0.45 EndY=0 EndZ=0
  constraints (35):
    c: Coincident(g14,g-1)
    c: PointOnObject(g5,g-2)
    c: Horizontal(g1)
    c: Vertical(g2)
    c: Horizontal(g3)
    c: DistanceX(g5,g8) = 2
    c: DistanceY(g11,g8) = 2
    c: PointOnObject(g5,g0)
    c: PointOnObject(g5,g1)
    c: Tangent(g0,g4) = 1.5708
    c: Tangent(g1,g4) = 1.5708
    c: Coincident(g6,g0)
    c: Coincident(g6,g1)
    c: PointOnObject(g8,g2)
    c: PointOnObject(g8,g1)
    c: Tangent(g2,g7) = 1.5708
    c: Tangent(g1,g7) = 1.5708
    c: Coincident(g9,g2)
    c: Coincident(g9,g1)
    c: PointOnObject(g11,g2)
    c: PointOnObject(g11,g3)
    c: Tangent(g2,g10) = 1.5708
    c: Tangent(g3,g10) = 1.5708
    c: Coincident(g12,g2)
    c: Coincident(g12,g3)
    c: PointOnObject(g14,g0)
    c: PointOnObject(g14,g3)
    c: Tangent(g0,g13) = 1.5708
    c: Tangent(g3,g13) = 1.5708
    c: Coincident(g15,g0)
    c: Coincident(g15,g3)
    c: Equal(g6,g9)
    c: Equal(g9,g12)
    c: Equal(g12,g15)
    c: DistanceX(g14,g3) = 0.45
FEATURE [PartDesign::Pad] Pad029
  Direction = (0,-1,2e-16)
  Length = 17
  Length2 = 10
  Midplane = true
  Placement = pos=(0,0,0) rot=(1,0,0;1.5708rad)
  Profile = -> Sketch134
  ReferenceAxis = -> Sketch134 [N_Axis]
  Refine = true
  Suppressed = false
  Type = 0
FEATURE [PartDesign::Body] Body008  label="perno fermo neopixel"
  AllowCompound = false
  Group = -> [Sketch134,Pad029]
  Origin = -> Origin008
  Tip = -> Pad029
FEATURE [Sketcher::SketchObject] Sketch135  label="perno fermo rumble003"
  ArcFitTolerance = 1e-06
  AttachmentSupport = -> [XZ_Plane009]
  FullyConstrained = true
  MakeInternals = false
  MapMode = 5
  Placement = pos=(0,0,0) rot=(1,0,0;1.5708rad)
  sketch-geometry (16):
    g0: LineSegment StartX=4.69e-14 StartY=0.8 StartZ=0 EndX=-3.04e-14 EndY=3.1 EndZ=0
    g1: LineSegment StartX=0.8 StartY=3.9 StartZ=0 EndX=3.1 EndY=3.9 EndZ=0
    g2: LineSegment StartX=3.9 StartY=3.1 StartZ=0 EndX=3.9 EndY=0.8 EndZ=0
    g3: LineSegment StartX=3.1 StartY=0 StartZ=0 EndX=0.8 EndY=0 EndZ=0
    g4: ArcOfCircle [constr] CenterX=0.8 CenterY=3.1 CenterZ=0 NormalX=0 NormalY=0 NormalZ=1 AngleXU=0 Radius=0.8 StartAngle=1.5708 EndAngle=3.14159
    g5: GeomPoint [constr] X=0 Y=3.9 Z=0
    g6: LineSegment StartX=0.8 StartY=3.9 StartZ=0 EndX=-3.04e-14 EndY=3.1 EndZ=0
    g7: ArcOfCircle [constr] CenterX=3.1 CenterY=3.1 CenterZ=0 NormalX=0 NormalY=0 NormalZ=1 AngleXU=0 Radius=0.8 StartAngle=-2.4e-14 EndAngle=1.5708
    g8: GeomPoint [constr] X=3.9 Y=3.9 Z=0
    g9: LineSegment StartX=3.9 StartY=3.1 StartZ=0 EndX=3.1 EndY=3.9 EndZ=0
    g10: ArcOfCircle [constr] CenterX=3.1 CenterY=0.8 CenterZ=0 NormalX=0 NormalY=0 NormalZ=1 AngleXU=0 Radius=0.8 StartAngle=4.71239 EndAngle=6.28319
    g11: GeomPoint [constr] X=3.9 Y=0 Z=0
    g12: LineSegment StartX=3.1 StartY=0 StartZ=0 EndX=3.9 EndY=0.8 EndZ=0
    g13: ArcOfCircle [constr] CenterX=0.8 CenterY=0.8 CenterZ=0 NormalX=0 NormalY=0 NormalZ=1 AngleXU=0 Radius=0.8 StartAngle=3.14159 EndAngle=4.71239
    g14: GeomPoint [constr] X=0 Y=0 Z=0
    g15: LineSegment StartX=4.69e-14 StartY=0.8 StartZ=0 EndX=0.8 EndY=0 EndZ=0
  constraints (35):
    c: Coincident(g14,g-1)
    c: PointOnObject(g5,g-2)
    c: Horizontal(g1)
    c: Vertical(g2)
    c: Horizontal(g3)
    c: DistanceX(g5,g8) = 3.9
    c: DistanceY(g11,g8) = 3.9
    c: PointOnObject(g5,g0)
    c: PointOnObject(g5,g1)
    c: Tangent(g0,g4) = 1.5708
    c: Tangent(g1,g4) = 1.5708
    c: Coincident(g6,g0)
    c: Coincident(g6,g1)
    c: PointOnObject(g8,g2)
    c: PointOnObject(g8,g1)
    c: Tangent(g2,g7) = 1.5708
    c: Tangent(g1,g7) = 1.5708
    c: Coincident(g9,g2)
    c: Coincident(g9,g1)
    c: PointOnObject(g11,g2)
    c: PointOnObject(g11,g3)
    c: Tangent(g2,g10) = 1.5708
    c: Tangent(g3,g10) = 1.5708
    c: Coincident(g12,g2)
    c: Coincident(g12,g3)
    c: PointOnObject(g14,g0)
    c: PointOnObject(g14,g3)
    c: Tangent(g0,g13) = 1.5708
    c: Tangent(g3,g13) = 1.5708
    c: Coincident(g15,g0)
    c: Coincident(g15,g3)
    c: Equal(g6,g9)
    c: Equal(g9,g12)
    c: Equal(g12,g15)
    c: DistanceX(g14,g3) = 0.8
FEATURE [PartDesign::Pad] Pad030
  Direction = (0,-1,2e-16)
  Length = 25.2
  Length2 = 10
  Midplane = true
  Placement = pos=(0,0,0) rot=(1,0,0;1.5708rad)
  Profile = -> Sketch135
  ReferenceAxis = -> Sketch135 [N_Axis]
  Refine = true
  Suppressed = false
  Type = 0
FEATURE [PartDesign::Body] Body009  label="perno fermo switch - caricabatterie - grilletto"
  AllowCompound = false
  Group = -> [Sketch135,Pad030]
  Origin = -> Origin009
  Tip = -> Pad030
FEATURE [Sketcher::SketchObject] Sketch136  label="scavo_rele"
  ArcFitTolerance = 1e-06
  AttachmentSupport = -> [XZ_Plane]
  ExternalGeometry = -> [Sketch]
  FullyConstrained = true
  MakeInternals = false
  MapMode = 5
  Placement = pos=(0,0,0) rot=(1,0,0;1.5708rad)
  sketch-geometry (7):
    g0: LineSegment [constr] StartX=-173.013 StartY=-62.644 StartZ=0 EndX=-176.535 EndY=-73.4861 EndZ=0
    g1: LineSegment [constr] StartX=-173.013 StartY=-62.644 StartZ=0 EndX=-170.35 EndY=-63.5093 EndZ=0
    g2: LineSegment [constr] StartX=-173.013 StartY=-62.644 StartZ=0 EndX=-176.627 EndY=-61.4698 EndZ=0
    g3: LineSegment StartX=-176.627 StartY=-61.4698 StartZ=0 EndX=-170.35 EndY=-63.5093 EndZ=0
    g4: LineSegment StartX=-176.627 StartY=-61.4698 StartZ=0 EndX=-180.149 EndY=-72.3118 EndZ=0
    g5: LineSegment StartX=-170.35 StartY=-63.5093 StartZ=0 EndX=-173.872 EndY=-74.3513 EndZ=0
    g6: LineSegment StartX=-180.149 StartY=-72.3118 StartZ=0 EndX=-173.872 EndY=-74.3513 EndZ=0
  constraints (19):
    c: Tangent(g0,g-3)
    c: Distance(g0,g-3) = 89
    c: Distance(g0,g0) = 11.4
    c: Coincident(g1,g0)
    c: Coincident(g2,g0)
    c: Distance(g2) = 3.8
    c: Distance(g1) = 2.8
    c: Perpendicular(g0,g1)
    c: Perpendicular(g0,g2)
    c: Coincident(g3,g2)
    c: Coincident(g3,g1)
    c: Equal(g4,g0)
    c: Equal(g5,g0)
    c: Parallel(g4,g0)
    c: Parallel(g5,g0)
    c: Coincident(g4,g2)
    c: Coincident(g5,g1)
    c: Coincident(g6,g4)
    c: Coincident(g6,g5)
FEATURE [Part::Extrusion] Extrude076  label="Extrude076 - scavo_rele"
  Base = -> Sketch136
  Dir = (0,-1,2e-16)
  DirMode = 2
  FaceMakerClass = Part::FaceMakerBullseye
  FaceMakerMode = 3
  LengthFwd = 17.8
  LengthRev = 0
  Solid = true
  Symmetric = true
FEATURE [Sketcher::SketchObject] Sketch137  label="scavo_nuovo_driver"
  ArcFitTolerance = 1e-06
  AttachmentSupport = -> [XZ_Plane]
  ExternalGeometry = -> [Sketch]
  FullyConstrained = true
  MakeInternals = false
  MapMode = 5
  Placement = pos=(0,0,0) rot=(1,0,0;1.5708rad)
  sketch-geometry (7):
    g0: LineSegment [constr] StartX=-167.759 StartY=-46.4761 StartZ=0 EndX=-172.58 EndY=-61.3126 EndZ=0
    g1: LineSegment [constr] StartX=-167.759 StartY=-46.4761 StartZ=0 EndX=-165.477 EndY=-47.2177 EndZ=0
    g2: LineSegment [constr] StartX=-167.759 StartY=-46.4761 StartZ=0 EndX=-171.373 EndY=-45.3018 EndZ=0
    g3: LineSegment StartX=-171.373 StartY=-45.3018 StartZ=0 EndX=-165.477 EndY=-47.2177 EndZ=0
    g4: LineSegment StartX=-171.373 StartY=-45.3018 StartZ=0 EndX=-176.194 EndY=-60.1383 EndZ=0
    g5: LineSegment StartX=-165.477 StartY=-47.2177 StartZ=0 EndX=-170.297 EndY=-62.0542 EndZ=0
    g6: LineSegment StartX=-176.194 StartY=-60.1383 StartZ=0 EndX=-170.297 EndY=-62.0542 EndZ=0
  constraints (19):
    c: Distance(g0,g-3) = 72
    c: Distance(g0) = 15.6
    c: Tangent(g0,g-3)
    c: Coincident(g1,g0)
    c: Coincident(g2,g0)
    c: Distance(g1) = 2.4
    c: Distance(g2) = 3.8
    c: Perpendicular(g0,g1)
    c: Perpendicular(g0,g2)
    c: Coincident(g3,g2)
    c: Coincident(g3,g1)
    c: Equal(g4,g0)
    c: Equal(g5,g0)
    c: Parallel(g4,g0)
    c: Parallel(g5,g0)
    c: Coincident(g4,g2)
    c: Coincident(g5,g1)
    c: Coincident(g6,g4)
    c: Coincident(g6,g5)
FEATURE [Part::Extrusion] Extrude077  label="Extrude077 - scavo_nuovo_driver"
  Base = -> Sketch137
  Dir = (0,-1,2e-16)
  DirMode = 2
  FaceMakerClass = Part::FaceMakerBullseye
  FaceMakerMode = 3
  LengthFwd = 20.8
  LengthRev = 0
  Solid = true
  Symmetric = true
FEATURE [Sketcher::SketchObject] Sketch138  label="scavo_nuovo_driver_alto"
  ArcFitTolerance = 1e-06
  AttachmentSupport = -> [XZ_Plane]
  ExternalGeometry = -> [Sketch]
  FullyConstrained = true
  MakeInternals = false
  MapMode = 5
  Placement = pos=(0,0,0) rot=(1,0,0;1.5708rad)
  sketch-geometry (7):
    g0: LineSegment [constr] StartX=-188.796 StartY=17.7274 StartZ=0 EndX=-187.75 EndY=4.97025 EndZ=0
    g1: LineSegment StartX=-187.75 StartY=4.97025 StartZ=0 EndX=-189.743 EndY=4.8067 EndZ=0
    g2: LineSegment StartX=-187.75 StartY=4.97025 StartZ=0 EndX=-182.766 EndY=5.37913 EndZ=0
    g3: LineSegment StartX=-190.79 StartY=17.5638 StartZ=0 EndX=-189.743 EndY=4.8067 EndZ=0
    g4: LineSegment StartX=-183.813 StartY=18.1363 StartZ=0 EndX=-182.766 EndY=5.37913 EndZ=0
    g5: LineSegment StartX=-190.79 StartY=17.5638 StartZ=0 EndX=-188.796 EndY=17.7274 EndZ=0
    g6: LineSegment StartX=-188.796 StartY=17.7274 StartZ=0 EndX=-183.813 EndY=18.1363 EndZ=0
  constraints (20):
    c: Distance(g0) = 12.8
    c: DistanceY(g-3,g0) = 9
    c: PointOnObject(g0,g-4)
    c: PointOnObject(g0,g-4)
    c: Coincident(g1,g0)
    c: Coincident(g2,g0)
    c: Distance(g1) = 2
    c: Distance(g2) = 5
    c: Perpendicular(g0,g1)
    c: Perpendicular(g0,g2)
    c: Equal(g3,g0)
    c: Parallel(g3,g0)
    c: Coincident(g3,g1)
    c: Equal(g4,g0)
    c: Parallel(g4,g0)
    c: Coincident(g4,g2)
    c: Coincident(g5,g3)
    c: Coincident(g5,g0)
    c: Coincident(g6,g0)
    c: Coincident(g6,g4)
FEATURE [Part::Extrusion] Extrude078  label="Extrude078 - scavo_nuovo_driver_alto"
  Base = -> Sketch138
  Dir = (0,-1,2e-16)
  DirMode = 2
  FaceMakerClass = Part::FaceMakerBullseye
  FaceMakerMode = 3
  LengthFwd = 16.6
  LengthRev = 0
  Solid = true
  Symmetric = true
FEATURE [Sketcher::SketchObject] Sketch139  label="fermi_nuovo_driver_alto"
  ArcFitTolerance = 1e-06
  AttachmentSupport = -> [XZ_Plane]
  ExternalGeometry = -> [Sketch138,Sketch]
  FullyConstrained = true
  MakeInternals = false
  MapMode = 5
  Placement = pos=(0,0,0) rot=(1,0,0;1.5708rad)
  sketch-geometry (17):
    g0: LineSegment [constr] StartX=-188.314 StartY=16.4295 StartZ=0 EndX=-187.885 EndY=13.7638 EndZ=0
    g1: LineSegment [constr] StartX=-187.885 StartY=13.7638 StartZ=0 EndX=-187.456 EndY=11.0981 EndZ=0
    g2: LineSegment StartX=-187.885 StartY=13.7638 StartZ=0 EndX=-187.71 EndY=12.6778 EndZ=0
    g3: LineSegment StartX=-187.885 StartY=13.7638 StartZ=0 EndX=-188.06 EndY=14.8499 EndZ=0
    g4: LineSegment StartX=-187.71 StartY=12.6778 StartZ=0 EndX=-185.538 EndY=13.0274 EndZ=0
    g5: LineSegment StartX=-188.06 StartY=14.8499 StartZ=0 EndX=-185.888 EndY=15.1994 EndZ=0
    g6: LineSegment StartX=-185.888 StartY=15.1994 StartZ=0 EndX=-185.538 EndY=13.0274 EndZ=0
    g7: LineSegment StartX=-187.456 StartY=11.0981 StartZ=0 EndX=-189.035 EndY=10.8439 EndZ=0
    g8: LineSegment StartX=-188.314 StartY=16.4295 StartZ=0 EndX=-189.893 EndY=16.1753 EndZ=0
    g9: LineSegment StartX=-189.893 StartY=16.1753 StartZ=0 EndX=-189.035 EndY=10.8439 EndZ=0
    g10: LineSegment StartX=-187.456 StartY=11.0981 StartZ=0 EndX=-185.284 EndY=11.4477 EndZ=0
    g11: LineSegment StartX=-188.314 StartY=16.4295 StartZ=0 EndX=-186.142 EndY=16.7791 EndZ=0
    g12: LineSegment StartX=-184.308 StartY=15.4537 StartZ=0 EndX=-183.958 EndY=13.2816 EndZ=0
    g13: ArcOfCircle CenterX=-185.888 CenterY=15.1994 CenterZ=0 NormalX=0 NormalY=0 NormalZ=1 AngleXU=0 Radius=1.6 StartAngle=0.15957 EndAngle=1.73037
    g14: GeomPoint [constr] X=-184.562 Y=17.0333 Z=0
    g15: ArcOfCircle CenterX=-185.538 CenterY=13.0274 CenterZ=0 NormalX=0 NormalY=0 NormalZ=1 AngleXU=0 Radius=1.6 StartAngle=4.87196 EndAngle=6.44276
    g16: GeomPoint [constr] X=-183.704 Y=11.7019 Z=0
  constraints (43):
    c: Tangent(g1,g0) = -1.5708
    c: Distance(g0) = 2.7
    c: Equal(g1,g0)
    c: Tangent(g1,g-5)
    c: Coincident(g2,g0)
    c: Coincident(g3,g0)
    c: Distance(g2) = 1.1
    c: Equal(g3,g2)
    c: PointOnObject(g3,g2)
    c: Coincident(g4,g2)
    c: Coincident(g5,g3)
    c: Distance(g4) = 2.2
    c: Equal(g4,g5)
    c: Perpendicular(g1,g4)
    c: Perpendicular(g0,g5)
    c: Coincident(g6,g5)
    c: Coincident(g6,g4)
    c: Coincident(g7,g1)
    c: Coincident(g8,g0)
    c: Distance(g7) = 1.6
    c: Equal(g7,g8)
    c: Perpendicular(g1,g7)
    c: Perpendicular(g8,g0)
    c: Coincident(g9,g8)
    c: Coincident(g9,g7)
    c: Coincident(g10,g1)
    c: Coincident(g11,g0)
    c: Distance(g10,g16) = 3.8
    c: Perpendicular(g1,g10)
    c: Perpendicular(g1,g11)
    c: DistanceY(g0,g-4) = 3.8
    c: PointOnObject(g14,g12)
    c: PointOnObject(g14,g11)
    c: Tangent(g12,g13) = 1.5708
    c: Tangent(g11,g13) = 1.5708
    c: PointOnObject(g16,g12)
    c: PointOnObject(g16,g10)
    c: Tangent(g12,g15) = 1.5708
    c: Tangent(g10,g15) = -1.5708
    c: Equal(g13,g15)
    c: Coincident(g13,g5)
    c: Parallel(g2,g0)
    c: PointOnObject(g0,g-5)
FEATURE [Part::Extrusion] Extrude079  label="Extrude079 - fermi_nuovo_driver_alto"
  Base = -> Sketch139
  Dir = (0,-1,2e-16)
  DirMode = 2
  FaceMakerClass = Part::FaceMakerBullseye
  FaceMakerMode = 3
  LengthFwd = 25.2
  LengthRev = 0
  Solid = true
  Symmetric = true
FEATURE [Sketcher::SketchObject] Sketch140  label="scavo_diodo_nuovo_driver_alto"
  ArcFitTolerance = 1e-06
  AttachmentSupport = -> [XZ_Plane]
  ExternalGeometry = -> [Sketch138]
  FullyConstrained = true
  MakeInternals = false
  MapMode = 5
  Placement = pos=(0,0,0) rot=(1,0,0;1.5708rad)
  sketch-geometry (4):
    g0: LineSegment StartX=-190.79 StartY=17.5638 StartZ=0 EndX=-189.743 EndY=4.8067 EndZ=0
    g1: LineSegment StartX=-193.78 StartY=17.3185 StartZ=0 EndX=-192.733 EndY=4.56137 EndZ=0
    g2: LineSegment StartX=-190.79 StartY=17.5638 StartZ=0 EndX=-193.78 EndY=17.3185 EndZ=0
    g3: LineSegment StartX=-192.733 StartY=4.56137 StartZ=0 EndX=-189.743 EndY=4.8067 EndZ=0
  constraints (11):
    c: Equal(g0,g-3)
    c: Parallel(g0,g-3)
    c: Equal(g1,g-3)
    c: Parallel(g1,g-3)
    c: Coincident(g2,g0)
    c: Distance(g2) = 3
    c: Perpendicular(g0,g2)
    c: Coincident(g1,g2)
    c: Coincident(g3,g1)
    c: Coincident(g3,g0)
    c: Coincident(g0,g-3)
FEATURE [Part::Extrusion] Extrude080  label="Extrude080 - scavo_diodo_nuovo_driver_alto"
  Base = -> Sketch140
  Dir = (0,-1,2e-16)
  DirMode = 2
  FaceMakerClass = Part::FaceMakerBullseye
  FaceMakerMode = 3
  LengthFwd = 4
  LengthRev = 0
  Placement = pos=(0,7.8,0) rot=(0,0,1;0rad)
  Solid = true
  Symmetric = false
FEATURE [Part::MultiFuse] Fusion001
  Refine = true
  Shapes = -> [Cut043,Extrude079]
FEATURE [Part::Cut] Cut044
  Base = -> Fusion001
  Refine = true
  Tool = -> Extrude078
FEATURE [Part::Cut] Cut045
  Base = -> Cut044
  Refine = true
  Tool = -> Extrude080
FEATURE [Sketcher::SketchObject] Sketch141  label="fermi_nuovo_driver"
  ArcFitTolerance = 1e-06
  AttachmentSupport = -> [XZ_Plane]
  ExternalGeometry = -> [Sketch,Sketch137]
  FullyConstrained = true
  MakeInternals = false
  MapMode = 5
  Placement = pos=(0,0,0) rot=(1,0,0;1.5708rad)
  sketch-geometry (16):
    g0: LineSegment [constr] StartX=-165.477 StartY=-47.2177 StartZ=0 EndX=-167.759 EndY=-46.4761 EndZ=0
    g1: LineSegment [constr] StartX=-167.759 StartY=-46.4761 StartZ=0 EndX=-168.006 EndY=-47.2369 EndZ=0
    g2: LineSegment [constr] StartX=-168.006 StartY=-47.2369 StartZ=0 EndX=-169.675 EndY=-52.3726 EndZ=0
    g3: LineSegment StartX=-169.675 StartY=-52.3726 StartZ=0 EndX=-171.767 EndY=-51.6928 EndZ=0
    g4: LineSegment StartX=-172.795 StartY=-49.6767 StartZ=0 EndX=-172.115 EndY=-47.5843 EndZ=0
    g5: LineSegment StartX=-170.099 StartY=-46.5571 StartZ=0 EndX=-166.485 EndY=-47.7313 EndZ=0
    g6: LineSegment StartX=-166.485 StartY=-47.7313 StartZ=0 EndX=-168.153 EndY=-52.867 EndZ=0
    g7: LineSegment StartX=-169.675 StartY=-52.3726 StartZ=0 EndX=-168.153 EndY=-52.867 EndZ=0
    g8: LineSegment StartX=-170.593 StartY=-48.0788 StartZ=0 EndX=-171.273 EndY=-50.1711 EndZ=0
    g9: LineSegment StartX=-171.273 StartY=-50.1711 StartZ=0 EndX=-169.181 EndY=-50.8509 EndZ=0
    g10: LineSegment StartX=-169.181 StartY=-50.8509 StartZ=0 EndX=-168.501 EndY=-48.7586 EndZ=0
    g11: LineSegment StartX=-168.501 StartY=-48.7586 StartZ=0 EndX=-170.593 EndY=-48.0788 EndZ=0
    g12: ArcOfCircle CenterX=-170.593 CenterY=-48.0788 CenterZ=0 NormalX=0 NormalY=0 NormalZ=1 AngleXU=0 Radius=1.6 StartAngle=1.25664 EndAngle=2.82743
    g13: GeomPoint [constr] X=-171.62 Y=-46.0626 Z=0
    g14: ArcOfCircle CenterX=-171.273 CenterY=-50.1711 CenterZ=0 NormalX=0 NormalY=0 NormalZ=1 AngleXU=0 Radius=1.6 StartAngle=2.82743 EndAngle=4.39823
    g15: GeomPoint [constr] X=-173.289 Y=-51.1984 Z=0
  constraints (41):
    c: Coincident(g0,g-4)
    c: PointOnObject(g0,g-3)
    c: Parallel(g0,g-4)
    c: Coincident(g1,g0)
    c: Parallel(g1,g-3)
    c: Distance(g1) = 0.8
    c: Coincident(g2,g1)
    c: Distance(g2) = 5.4
    c: Coincident(g3,g2)
    c: Parallel(g2,g-3)
    c: Distance(g15,g13) = 5.4
    c: Perpendicular(g3,g2)
    c: Parallel(g4,g2)
    c: Distance(g5,g13) = 5.4
    c: Distance(g3,g15) = 3.8
    c: Perpendicular(g4,g5)
    c: Coincident(g6,g5)
    c: Distance(g6) = 5.4
    c: Parallel(g6,g4)
    c: Coincident(g7,g2)
    c: Coincident(g7,g6)
    c: Coincident(g8,g9)
    c: Coincident(g9,g10)
    c: Coincident(g10,g11)
    c: Coincident(g11,g8)
    c: Distance(g8,g10) = 2.2
    c: Distance(g9,g11) = 2.2
    c: Perpendicular(g11,g8)
    c: Equal(g8,g10)
    c: Equal(g11,g9)
    c: Tangent(g10,g2)
    c: Distance(g10,g1) = 1.6
    c: PointOnObject(g13,g4)
    c: PointOnObject(g13,g5)
    c: Tangent(g4,g12) = 1.5708
    c: Tangent(g5,g12) = 1.5708
    c: PointOnObject(g15,g4)
    c: Tangent(g4,g14) = 1.5708
    c: Tangent(g3,g14) = 1.5708
    c: Equal(g14,g12)
    c: Coincident(g12,g8)
FEATURE [Part::Extrusion] Extrude081  label="Extrude081 - fermi_nuovo_driver"
  Base = -> Sketch141
  Dir = (0,-1,2e-16)
  DirMode = 2
  FaceMakerClass = Part::FaceMakerBullseye
  FaceMakerMode = 3
  LengthFwd = 25.2
  LengthRev = 0
  Solid = true
  Symmetric = true
FEATURE [Part::MultiFuse] Fusion002
  Refine = true
  Shapes = -> [Cut045,Extrude081]
FEATURE [Part::Cut] Cut046
  Base = -> Fusion002
  Refine = true
  Tool = -> Extrude077
FEATURE [Sketcher::SketchObject] Sketch142  label="fermi_rele"
  ArcFitTolerance = 1e-06
  AttachmentSupport = -> [XZ_Plane]
  ExternalGeometry = -> [Sketch,Sketch136]
  FullyConstrained = true
  MakeInternals = false
  MapMode = 5
  Placement = pos=(0,0,0) rot=(1,0,0;1.5708rad)
  sketch-geometry (15):
    g0: LineSegment StartX=-177.245 StartY=-63.3719 StartZ=0 EndX=-177.924 EndY=-65.4642 EndZ=0
    g1: LineSegment StartX=-175.228 StartY=-62.3446 StartZ=0 EndX=-171.614 EndY=-63.5189 EndZ=0
    g2: LineSegment StartX=-171.614 StartY=-63.5189 StartZ=0 EndX=-173.283 EndY=-68.6546 EndZ=0
    g3: LineSegment StartX=-176.897 StartY=-67.4803 StartZ=0 EndX=-173.283 EndY=-68.6546 EndZ=0
    g4: LineSegment StartX=-175.723 StartY=-63.8663 StartZ=0 EndX=-173.631 EndY=-64.5461 EndZ=0
    g5: LineSegment StartX=-175.723 StartY=-63.8663 StartZ=0 EndX=-176.403 EndY=-65.9586 EndZ=0
    g6: LineSegment StartX=-173.631 StartY=-64.5461 StartZ=0 EndX=-174.31 EndY=-66.6385 EndZ=0
    g7: LineSegment StartX=-176.403 StartY=-65.9586 StartZ=0 EndX=-174.31 EndY=-66.6385 EndZ=0
    g8: LineSegment [constr] StartX=-173.631 StartY=-64.5461 StartZ=0 EndX=-173.136 EndY=-63.0245 EndZ=0
    g9: LineSegment [constr] StartX=-173.631 StartY=-64.5461 StartZ=0 EndX=-172.109 EndY=-65.0406 EndZ=0
    g10: LineSegment [constr] StartX=-170.35 StartY=-63.5093 StartZ=0 EndX=-173.013 EndY=-62.644 EndZ=0
    g11: ArcOfCircle CenterX=-175.723 CenterY=-63.8663 CenterZ=0 NormalX=0 NormalY=0 NormalZ=1 AngleXU=0 Radius=1.6 StartAngle=1.25664 EndAngle=2.82743
    g12: GeomPoint [constr] X=-176.75 Y=-61.8502 Z=0
    g13: ArcOfCircle CenterX=-176.403 CenterY=-65.9586 CenterZ=0 NormalX=0 NormalY=0 NormalZ=1 AngleXU=0 Radius=1.6 StartAngle=2.82743 EndAngle=4.39823
    g14: GeomPoint [constr] X=-178.419 Y=-66.9859 Z=0
  constraints (39):
    c: Distance(g14,g12) = 5.4
    c: Distance(g1,g12) = 5.4
    c: Perpendicular(g1,g0)
    c: Coincident(g2,g1)
    c: Parallel(g2,g0)
    c: Coincident(g3,g2)
    c: Parallel(g2,g-3)
    c: Coincident(g5,g4)
    c: Distance(g5) = 2.2
    c: Distance(g4) = 2.2
    c: Perpendicular(g4,g5)
    c: Coincident(g6,g4)
    c: Equal(g6,g5)
    c: Parallel(g6,g5)
    c: Coincident(g7,g5)
    c: Coincident(g7,g6)
    c: Coincident(g8,g4)
    c: Coincident(g9,g4)
    c: Distance(g8) = 1.6
    c: Distance(g9) = 1.6
    c: Parallel(g8,g6)
    c: Parallel(g9,g4)
    c: PointOnObject(g8,g1)
    c: PointOnObject(g9,g2)
    c: Coincident(g10,g-4)
    c: Parallel(g10,g-4)
    c: PointOnObject(g10,g-3)
    c: Tangent(g6,g-3) = 1.5708
    c: Distance(g4,g10) = 2
    c: PointOnObject(g12,g1)
    c: Tangent(g1,g11) = 1.5708
    c: Tangent(g0,g11) = -1.5708
    c: PointOnObject(g14,g3)
    c: PointOnObject(g14,g0)
    c: Tangent(g3,g13) = -1.5708
    c: Tangent(g0,g13) = -1.5708
    c: Equal(g11,g13)
    c: Coincident(g11,g4)
    c: Parallel(g3,g1)
FEATURE [Part::Extrusion] Extrude082  label="Extrude082 - fermi_rele"
  Base = -> Sketch142
  Dir = (0,-1,2e-16)
  DirMode = 2
  FaceMakerClass = Part::FaceMakerBullseye
  FaceMakerMode = 3
  LengthFwd = 25.2
  LengthRev = 0
  Solid = true
  Symmetric = true
FEATURE [Part::MultiFuse] Fusion003
  Refine = true
  Shapes = -> [Cut046,Extrude082]
FEATURE [Part::Cut] Cut047
  Base = -> Fusion003
  Refine = true
  Tool = -> Extrude076
FEATURE [Sketcher::SketchObject] Sketch143  label="foro_passaggio_cavi_led_batteria"
  ArcFitTolerance = 1e-06
  AttachmentSupport = -> [XZ_Plane]
  ExternalGeometry = -> [Sketch,Sketch042,Sketch036]
  FullyConstrained = true
  MakeInternals = false
  MapMode = 5
  Placement = pos=(0,0,0) rot=(1,0,0;1.5708rad)
  sketch-geometry (4):
    g0: LineSegment StartX=-207.775 StartY=-41.3701 StartZ=0 EndX=-213.607 EndY=-53.8767 EndZ=0
    g1: LineSegment StartX=-213.607 StartY=-53.8767 StartZ=0 EndX=-211.843 EndY=-59.5559 EndZ=0
    g2: LineSegment StartX=-207.775 StartY=-41.3701 StartZ=0 EndX=-207.775 EndY=-50.8316 EndZ=0
    g3: LineSegment StartX=-207.775 StartY=-50.8316 StartZ=0 EndX=-211.843 EndY=-59.5559 EndZ=0
  constraints (9):
    c: Coincident(g0,g-3)
    c: PointOnObject(g1,g-6)
    c: Coincident(g1,g0)
    c: Coincident(g2,g0)
    c: Coincident(g2,g-7)
    c: Coincident(g3,g2)
    c: Parallel(g3,g0)
    c: Coincident(g3,g1)
    c: Coincident(g0,g-5)
FEATURE [Part::Extrusion] Extrude083  label="Extrude083 - foro_passaggio_cavi_led_batteria"
  Base = -> Sketch143
  Dir = (0,-1,2e-16)
  DirMode = 2
  FaceMakerClass = Part::FaceMakerBullseye
  FaceMakerMode = 3
  LengthFwd = 6
  LengthRev = 0
  Solid = true
  Symmetric = true
FEATURE [Part::Cut] Cut048
  Base = -> Cut047
  Refine = true
  Tool = -> Extrude083
FEATURE [Sketcher::SketchObject] Sketch144  label="foro_areazione_alimentatore"
  ArcFitTolerance = 1e-06
  AttachmentSupport = -> [XZ_Plane]
  ExternalGeometry = -> [Sketch036]
  FullyConstrained = true
  MakeInternals = false
  MapMode = 5
  Placement = pos=(0,0,0) rot=(1,0,0;1.5708rad)
  sketch-geometry (4):
    g0: LineSegment StartX=-211.843 StartY=-60.3701 StartZ=0 EndX=-207.775 EndY=-60.3701 EndZ=0
    g1: LineSegment StartX=-207.775 StartY=-60.3701 StartZ=0 EndX=-207.775 EndY=-70.3701 EndZ=0
    g2: LineSegment StartX=-211.843 StartY=-60.3701 StartZ=0 EndX=-211.843 EndY=-70.3701 EndZ=0
    g3: LineSegment StartX=-207.775 StartY=-70.3701 StartZ=0 EndX=-211.843 EndY=-70.3701 EndZ=0
  constraints (11):
    c: Horizontal(g0)
    c: Distance(g1) = 10
    c: Coincident(g1,g0)
    c: Tangent(g1,g-3)
    c: PointOnObject(g0,g-4)
    c: Coincident(g2,g0)
    c: PointOnObject(g2,g-4)
    c: Coincident(g3,g1)
    c: Horizontal(g3)
    c: Coincident(g3,g2)
    c: DistanceY(g0,g-3) = 19
FEATURE [Part::Extrusion] Extrude084  label="Extrude084 - foro_areazione_alimentatore"
  Base = -> Sketch144
  Dir = (0,-1,2e-16)
  DirMode = 2
  FaceMakerClass = Part::FaceMakerBullseye
  FaceMakerMode = 3
  LengthFwd = 10
  LengthRev = 0
  Solid = true
  Symmetric = true
FEATURE [Part::Cut] Cut049
  Base = -> Cut048
  Refine = true
  Tool = -> Extrude084
FEATURE [Sketcher::SketchObject] Sketch145  label="foro_per_condesatore"
  ArcFitTolerance = 1e-06
  AttachmentSupport = -> [XZ_Plane]
  ExternalGeometry = -> [Sketch,Sketch139]
  FullyConstrained = true
  MakeInternals = false
  MapMode = 5
  Placement = pos=(0,0,0) rot=(1,0,0;1.5708rad)
  sketch-geometry (1):
    g0: Circle CenterX=-182.345 CenterY=7.02342 CenterZ=0 NormalX=0 NormalY=0 NormalZ=1 AngleXU=0 Radius=5.2
  constraints (3):
    c: Diameter(g0) = 10.4
    c: Tangent(g0,g-3)
    c: Tangent(g0,g-4)
FEATURE [Part::Extrusion] Extrude085  label="Extrude085 - foro_per_condesatore"
  Base = -> Sketch145
  Dir = (0,-1,2e-16)
  DirMode = 2
  FaceMakerClass = Part::FaceMakerBullseye
  FaceMakerMode = 3
  LengthFwd = 25.2
  LengthRev = 0
  Solid = true
  Symmetric = true
FEATURE [Part::Cut] Cut050
  Base = -> Cut049
  Refine = true
  Tool = -> Extrude085
FEATURE [Sketcher::SketchObject] Sketch146  label="scavo_pulsante_6x6_per_led_batteria"
  ArcFitTolerance = 1e-06
  AttachmentSupport = -> [XZ_Plane]
  ExternalGeometry = -> [Sketch036,Sketch016]
  FullyConstrained = true
  MakeInternals = false
  MapMode = 5
  Placement = pos=(0,0,0) rot=(1,0,0;1.5708rad)
  sketch-geometry (4):
    g0: LineSegment StartX=-217.243 StartY=-66.0316 StartZ=0 EndX=-217.243 EndY=-72.8316 EndZ=0
    g1: LineSegment StartX=-217.243 StartY=-72.8316 StartZ=0 EndX=-211.043 EndY=-72.8316 EndZ=0
    g2: LineSegment StartX=-211.043 StartY=-72.8316 StartZ=0 EndX=-211.043 EndY=-66.0316 EndZ=0
    g3: LineSegment StartX=-211.043 StartY=-66.0316 StartZ=0 EndX=-217.243 EndY=-66.0316 EndZ=0
  constraints (12):
    c: Coincident(g0,g1)
    c: Coincident(g1,g2)
    c: Coincident(g2,g3)
    c: Coincident(g3,g0)
    c: Vertical(g0)
    c: Vertical(g2)
    c: Horizontal(g1)
    c: Horizontal(g3)
    c: Distance(g0,g2) = 6.2
    c: Distance(g1,g3) = 6.8
    c: Tangent(g1,g-4)
    c: DistanceX(g-3,g1) = 0.8
FEATURE [Part::Extrusion] Extrude086  label="Extrude086 - scavo_pulsante_6x6_per_led_batteria"
  Base = -> Sketch146
  Dir = (0,-1,2e-16)
  DirMode = 2
  FaceMakerClass = Part::FaceMakerBullseye
  FaceMakerMode = 3
  LengthFwd = 4.2
  LengthRev = 0
  Placement = pos=(0,12.6,0) rot=(0,0,1;0rad)
  Solid = true
  Symmetric = false
FEATURE [Sketcher::SketchObject] Sketch147  label="scavo_led_stato_batteria"
  ArcFitTolerance = 1e-06
  AttachmentSupport = -> [XZ_Plane]
  ExternalGeometry = -> [Sketch036,Sketch]
  FullyConstrained = true
  MakeInternals = false
  MapMode = 5
  Placement = pos=(0,0,0) rot=(1,0,0;1.5708rad)
  sketch-geometry (4):
    g0: LineSegment StartX=-215.943 StartY=-56.0944 StartZ=0 EndX=-215.943 EndY=-65.2944 EndZ=0
    g1: LineSegment StartX=-215.943 StartY=-65.2944 StartZ=0 EndX=-211.343 EndY=-65.2944 EndZ=0
    g2: LineSegment StartX=-211.343 StartY=-65.2944 StartZ=0 EndX=-211.343 EndY=-56.0944 EndZ=0
    g3: LineSegment StartX=-211.343 StartY=-56.0944 StartZ=0 EndX=-215.943 EndY=-56.0944 EndZ=0
  constraints (12):
    c: Coincident(g0,g1)
    c: Coincident(g1,g2)
    c: Coincident(g2,g3)
    c: Coincident(g3,g0)
    c: Distance(g0,g2) = 4.6
    c: Distance(g1,g3) = 9.2
    c: DistanceY(g2,g-3) = 6
    c: Equal(g0,g2)
    c: Equal(g1,g3)
    c: Perpendicular(g3,g0)
    c: Parallel(g2,g-3)
    c: DistanceX(g-3,g2) = 0.5
FEATURE [PartDesign::Body] Body  label="Struttura pistola"
  AllowCompound = false
  Group = -> [Sketch,Sketch002,Sketch004,DatumPlane,Sketch005,DatumPlane001,CopyCut,Sketch008,Sketch009,Sketch010,Sketch011,Sketch012,Sketch013,Sketch014,Sketch015,Sketch016,Sketch017,Sketch018,Sketch019,Sketch020,Sketch022,Sketch023,Sketch024,Sketch025,Sketch026,Sketch027,Sketch029,Sketch030,Sketch031,Sketch032,Sketch033,Sketch034,Sketch035,Sketch036,Sketch037,Sketch038,Sketch039,Sketch040,Sketch041,Sketch042,+27 more]
  Origin = -> Origin
FEATURE [Part::Extrusion] Extrude087  label="Extrude087 - scavo_led_stato_batteria"
  Base = -> Sketch147
  Dir = (0,-1,2e-16)
  DirMode = 2
  FaceMakerClass = Part::FaceMakerBullseye
  FaceMakerMode = 3
  LengthFwd = 2
  LengthRev = 0
  Placement = pos=(0,12.6,0) rot=(0,0,1;0rad)
  Solid = true
  Symmetric = false
FEATURE [Part::Cut] Cut051
  Base = -> Cut050
  Refine = true
  Tool = -> Extrude086
FEATURE [Part::Cut] Cut052
  Base = -> Cut051
  Refine = true
  Tool = -> Extrude087
FEATURE [Sketcher::SketchObject] Sketch148
  ArcFitTolerance = 1e-06
  AttachmentSupport = -> [Pad016]
  ExternalGeometry = -> [Pad016]
  FullyConstrained = true
  MakeInternals = false
  MapMode = 5
  Placement = pos=(0,0,-80.4316) rot=(1,0,0;3.14159rad)
  sketch-geometry (8):
    g0: LineSegment StartX=-176.685 StartY=3.6 StartZ=0 EndX=-186.685 EndY=3.6 EndZ=0
    g1: LineSegment StartX=-176.685 StartY=3.6 StartZ=0 EndX=-176.685 EndY=1.69e-14 EndZ=0
    g2: LineSegment [constr] StartX=-186.685 StartY=3.6 StartZ=0 EndX=-186.685 EndY=1.69e-14 EndZ=0
    g3: ArcOfEllipse CenterX=-186.685 CenterY=1.68e-14 CenterZ=0 NormalX=0 NormalY=0 NormalZ=1 MajorRadius=10 MinorRadius=3.6 AngleXU=0 StartAngle=0 EndAngle=1.5708
    g4: LineSegment [constr] StartX=-176.685 StartY=1.68e-14 StartZ=0 EndX=-196.685 EndY=1.68e-14 EndZ=0
    g5: LineSegment [constr] StartX=-186.685 StartY=3.6 StartZ=0 EndX=-186.685 EndY=-3.6 EndZ=0
    g6: GeomPoint [constr] X=-177.356 Y=1.68e-14 Z=0
    g7: GeomPoint [constr] X=-196.015 Y=1.68e-14 Z=0
  constraints (13):
    c: Distance(g0) = 10
    c: Coincident(g0,g-5)
    c: PointOnObject(g0,g-3)
    c: Coincident(g1,g0)
    c: Coincident(g1,g-5)
    c: Coincident(g2,g0)
    c: Vertical(g2)
    c: PointOnObject(g2,g-4)
    c: InternalAlignment(g4-g7 -> g3) x4
    c: Coincident(g3,g2)
    c: Coincident(g3,g0)
    c: Coincident(g3,g1)
    c: Horizontal(g4)
FEATURE [PartDesign::SubtractivePipe] SubtractivePipe004
  AuxilleryCurvelinear = true
  AuxillerySpineTangent = false
  BaseFeature = -> Pad016
  Binormal = (0,0,0)
  Mode = 0
  Profile = -> Sketch148
  Refine = true
  Spine = -> Pad016 [Edge254]
  SpineTangent = false
  Suppressed = false
  Transformation = 0
  Transition = 0
FEATURE [Sketcher::SketchObject] Sketch149
  ArcFitTolerance = 1e-06
  AttachmentSupport = -> [Pad016]
  ExternalGeometry = -> [Pad016]
  FullyConstrained = true
  MakeInternals = false
  MapMode = 5
  Placement = pos=(0,0,-80.4316) rot=(1,0,0;3.14159rad)
  sketch-geometry (8):
    g0: LineSegment StartX=-215.932 StartY=3.6 StartZ=0 EndX=-205.932 EndY=3.6 EndZ=0
    g1: LineSegment StartX=-215.932 StartY=3.6 StartZ=0 EndX=-215.932 EndY=1.64e-14 EndZ=0
    g2: LineSegment [constr] StartX=-205.932 StartY=3.6 StartZ=0 EndX=-205.932 EndY=1.69e-14 EndZ=0
    g3: ArcOfEllipse CenterX=-205.932 CenterY=1.69e-14 CenterZ=0 NormalX=0 NormalY=0 NormalZ=1 MajorRadius=10 MinorRadius=3.6 AngleXU=-3.14159 StartAngle=4.71239 EndAngle=6.28319
    g4: LineSegment [constr] StartX=-215.932 StartY=1.68e-14 StartZ=0 EndX=-195.932 EndY=1.68e-14 EndZ=0
    g5: LineSegment [constr] StartX=-205.932 StartY=-3.6 StartZ=0 EndX=-205.932 EndY=3.6 EndZ=0
    g6: GeomPoint [constr] X=-215.262 Y=1.57e-14 Z=0
    g7: GeomPoint [constr] X=-196.602 Y=1.68e-14 Z=0
  constraints (13):
    c: Distance(g0) = 10
    c: Coincident(g0,g-5)
    c: PointOnObject(g0,g-5)
    c: Coincident(g1,g0)
    c: Coincident(g1,g-4)
    c: Coincident(g2,g0)
    c: Vertical(g2)
    c: PointOnObject(g2,g-3)
    c: InternalAlignment(g4-g7 -> g3) x4
    c: Coincident(g3,g2)
    c: Coincident(g3,g0)
    c: Coincident(g3,g1)
    c: Horizontal(g4)
FEATURE [PartDesign::SubtractivePipe] SubtractivePipe005
  AuxilleryCurvelinear = true
  AuxillerySpineTangent = false
  BaseFeature = -> SubtractivePipe004
  Binormal = (0,0,0)
  Mode = 0
  Profile = -> Sketch149
  Refine = true
  Spine = -> Pad016 [Edge256,Edge251,Edge252]
  SpineTangent = false
  Suppressed = false
  Transformation = 0
  Transition = 0
FEATURE [PartDesign::SubtractiveLoft] SubtractiveLoft002
  BaseFeature = -> SubtractivePipe005
  Closed = false
  Profile = -> Sketch129
  Refine = true
  Ruled = false
  Sections = -> [Sketch130]
  Suppressed = false
FEATURE [PartDesign::SubtractiveLoft] SubtractiveLoft003
  BaseFeature = -> SubtractiveLoft002
  Closed = false
  Profile = -> Clone2D001
  Refine = true
  Ruled = false
  Sections = -> [Sketch131]
  Suppressed = false
FEATURE [PartDesign::Chamfer] Chamfer010
  Angle = 45
  Base = -> SubtractiveLoft003 [Edge203,Edge204,Edge202,Edge201,Edge195]
  BaseFeature = -> SubtractiveLoft003
  ChamferType = 0
  FlipDirection = false
  Refine = true
  Size = 1.5
  Size2 = 1
  SupportTransform = false
  Suppressed = false
  UseAllEdges = false
FEATURE [PartDesign::Chamfer] Chamfer011
  Angle = 45
  Base = -> Chamfer010 [Edge15]
  BaseFeature = -> Chamfer010
  ChamferType = 0
  FlipDirection = false
  Refine = true
  Size = 1.6
  Size2 = 1
  SupportTransform = false
  Suppressed = false
  UseAllEdges = false
FEATURE [PartDesign::Chamfer] Chamfer012
  Angle = 45
  Base = -> Chamfer011 [Edge10]
  BaseFeature = -> Chamfer011
  ChamferType = 0
  FlipDirection = false
  Refine = true
  Size = 3.5
  Size2 = 1
  SupportTransform = false
  Suppressed = false
  UseAllEdges = false
FEATURE [PartDesign::Chamfer] Chamfer013
  Angle = 45
  Base = -> Chamfer012 [Edge94]
  BaseFeature = -> Chamfer012
  ChamferType = 0
  FlipDirection = false
  Refine = true
  Size = 1.9
  Size2 = 1
  SupportTransform = false
  Suppressed = false
  UseAllEdges = false
FEATURE [PartDesign::Fillet] Fillet007
  Base = -> Chamfer013 [Edge83]
  BaseFeature = -> Chamfer013
  Radius = 1.1
  Refine = true
  SupportTransform = false
  Suppressed = false
  UseAllEdges = false
FEATURE [PartDesign::Fillet] Fillet008
  Base = -> Fillet007 [Edge75]
  BaseFeature = -> Fillet007
  Radius = 1.9
  Refine = true
  SupportTransform = false
  Suppressed = false
  UseAllEdges = false
FEATURE [PartDesign::Pocket] Pocket011
  BaseFeature = -> Fillet008
  Direction = (0,1,-2e-16)
  Length = 0.8
  Length2 = 5
  Profile = -> Sketch132
  ReferenceAxis = -> Sketch132 [N_Axis]
  Refine = true
  Suppressed = false
  Type = 0
FEATURE [PartDesign::Pocket] Pocket012
  BaseFeature = -> Pocket011
  Direction = (0,1,0)
  Length = 1
  Length2 = 5
  Profile = -> ShapeString
  ReferenceAxis = -> ShapeString [N_Axis]
  Refine = true
  Suppressed = false
  Type = 0
FEATURE [PartDesign::Body] Body007  label="lato DX"
  AllowCompound = false
  Group = -> [Binder001,Sketch114,Pad011,Chamfer014,Sketch115,Pocket006,Sketch116,Pad012,Sketch117,Pocket007,Sketch118,Pad013,Sketch119,Pocket008,Pad017,Chamfer009,Pocket009,Sketch123,Sketch120,Pad014,Pad018,Chamfer008,Pocket010,Sketch121,Pad015,Sketch122,Pad016,SubtractivePipe004,SubtractivePipe005,Sketch149,Sketch148,Sketch124,Sketch125,Sketch126,Sketch129,Sketch130,Clone2D001,Sketch131,SubtractiveLoft002,+11 more]
  Origin = -> Origin007
  Tip = -> Pocket012
note: 2 file-system paths scrubbed to <path> (originals preserved in the JSON sidecar)
